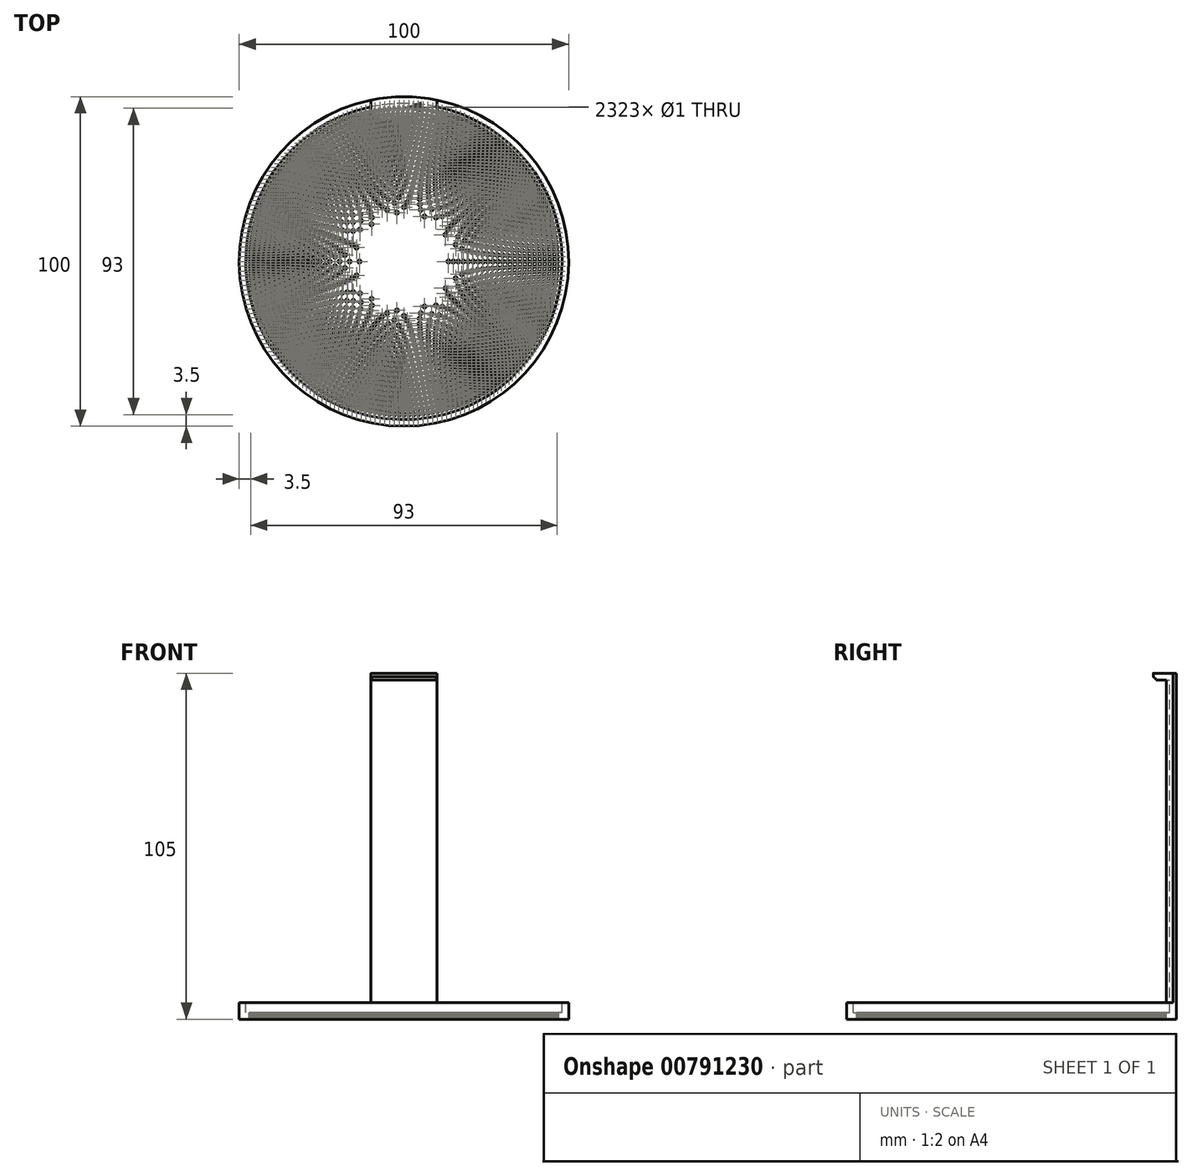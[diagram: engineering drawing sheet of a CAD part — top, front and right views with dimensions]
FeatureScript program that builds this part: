
annotation { "Feature Type Name" : "Feature", "Feature Type Description" : "" }
export const myFeature = defineFeature(function(context is Context, id is Id, definition is map)
    precondition{}
    {
        {
            var Q0;
            Q0=qCreatedBy(makeId("Top.planeOp"),FACE);
            var sketch = newSketch(context, id + "F0", { "sketchPlane" : qUnion([Q0])});
            skCircle(sketch, "E0", {"center": v(0, 0) * mm, "radius": 50 * mm});
            skSolve(sketch);
        }
        {
            var Q0;
            Q0 = qSketchRegion(id + "F0", true);
            extrude(context, id + "F1", {"entities" : qUnion([Q0]), "depth" : 5 * mm, "offsetDistance" : 25 * mm});
        }
        {
            var Q0;
            Q0=makeQuery(id+"F1.opExtrude","CAP_FACE",FACE,{"disambiguationData":[OSD([sQuery(id+"F0.wireOp",EDGE,"E0")])],"isStart":false});
            var sketch = newSketch(context, id + "F2", { "sketchPlane" : qUnion([Q0])});
            skCircle(sketch, "E1", {"center": v(0, 0) * mm, "radius": 48 * mm});
            skSolve(sketch);
        }
        {
            var Q0;
            Q0 = qSketchRegion(id + "F2", true);
            extrude(context, id + "F3", {"entities" : qUnion([Q0]), "operationType" : NewBodyOperationType.REMOVE, "oppositeDirection" : true, "depth" : 3 * mm, "offsetDistance" : 25 * mm});
        }
        {
            var Q0;
            Q0=makeQuery(id+"F3.boolean.opBoolean","COPY",FACE,{"derivedFrom":makeQuery(id+"F3.opExtrude","CAP_FACE",FACE,{"disambiguationData":[OSD([sQuery(id+"F2.wireOp",EDGE,"E1")])],"isStart":false})});
            var sketch = newSketch(context, id + "F4", { "sketchPlane" : qUnion([Q0])});
            skLineSegment(sketch, "E2", {"start": v(0, 0) * mm, "end": v(52.93, 0) * mm, "construction": true});
            skCircle(sketch, "E3", {"center": v(0, 0) * mm, "radius": 0.5 * mm, "construction": true});
            skCircle(sketch, "E4.1.0.0", {"center": v(1.5, 0) * mm, "radius": 0.5 * mm, "construction": true});
            skCircle(sketch, "E4.2.0.0", {"center": v(3, 0) * mm, "radius": 0.5 * mm, "construction": true});
            skCircle(sketch, "E4.3.0.0", {"center": v(4.5, 0) * mm, "radius": 0.5 * mm, "construction": true});
            skCircle(sketch, "E4.4.0.0", {"center": v(6, 0) * mm, "radius": 0.5 * mm, "construction": true});
            skCircle(sketch, "E4.5.0.0", {"center": v(7.5, 0) * mm, "radius": 0.5 * mm, "construction": true});
            skCircle(sketch, "E4.6.0.0", {"center": v(9, 0) * mm, "radius": 0.5 * mm, "construction": true});
            skCircle(sketch, "E4.7.0.0", {"center": v(10.5, 0) * mm, "radius": 0.5 * mm, "construction": true});
            skCircle(sketch, "E4.8.0.0", {"center": v(12, 0) * mm, "radius": 0.5 * mm, "construction": true});
            skCircle(sketch, "E4.9.0.0", {"center": v(13.5, 0) * mm, "radius": 0.5 * mm});
            skCircle(sketch, "E4.10.0.0", {"center": v(15, 0) * mm, "radius": 0.5 * mm});
            skCircle(sketch, "E4.11.0.0", {"center": v(16.5, 0) * mm, "radius": 0.5 * mm});
            skCircle(sketch, "E4.12.0.0", {"center": v(18, 0) * mm, "radius": 0.5 * mm});
            skCircle(sketch, "E4.13.0.0", {"center": v(19.5, 0) * mm, "radius": 0.5 * mm});
            skCircle(sketch, "E4.14.0.0", {"center": v(21, 0) * mm, "radius": 0.5 * mm});
            skCircle(sketch, "E4.15.0.0", {"center": v(22.5, 0) * mm, "radius": 0.5 * mm});
            skCircle(sketch, "E4.16.0.0", {"center": v(24, 0) * mm, "radius": 0.5 * mm});
            skCircle(sketch, "E4.17.0.0", {"center": v(25.5, 0) * mm, "radius": 0.5 * mm});
            skCircle(sketch, "E4.18.0.0", {"center": v(27, 0) * mm, "radius": 0.5 * mm});
            skCircle(sketch, "E4.19.0.0", {"center": v(28.5, 0) * mm, "radius": 0.5 * mm});
            skCircle(sketch, "E4.20.0.0", {"center": v(30, 0) * mm, "radius": 0.5 * mm});
            skCircle(sketch, "E4.21.0.0", {"center": v(31.5, 0) * mm, "radius": 0.5 * mm});
            skCircle(sketch, "E4.22.0.0", {"center": v(33, 0) * mm, "radius": 0.5 * mm});
            skCircle(sketch, "E4.23.0.0", {"center": v(34.5, 0) * mm, "radius": 0.5 * mm});
            skCircle(sketch, "E4.24.0.0", {"center": v(36, 0) * mm, "radius": 0.5 * mm});
            skCircle(sketch, "E4.25.0.0", {"center": v(37.5, 0) * mm, "radius": 0.5 * mm});
            skCircle(sketch, "E4.26.0.0", {"center": v(39, 0) * mm, "radius": 0.5 * mm});
            skCircle(sketch, "E4.27.0.0", {"center": v(40.5, 0) * mm, "radius": 0.5 * mm});
            skCircle(sketch, "E4.28.0.0", {"center": v(42, 0) * mm, "radius": 0.5 * mm});
            skCircle(sketch, "E4.29.0.0", {"center": v(43.5, 0) * mm, "radius": 0.5 * mm});
            skCircle(sketch, "E4.30.0.0", {"center": v(45, 0) * mm, "radius": 0.5 * mm});
            skCircle(sketch, "E4.31.0.0", {"center": v(46.5, 0) * mm, "radius": 0.5 * mm});
            skLineSegment(sketch, "E4.direction1", {"start": v(0, 0) * mm, "end": v(1.5, 0) * mm, "construction": true});
            skCircle(sketch, "E5.1.0", {"center": v(46.48, 1.46) * mm, "radius": 0.5 * mm});
            skCircle(sketch, "E5.2.0", {"center": v(46.4, 2.92) * mm, "radius": 0.5 * mm});
            skCircle(sketch, "E5.3.0", {"center": v(46.3, 4.38) * mm, "radius": 0.5 * mm});
            skCircle(sketch, "E5.4.0", {"center": v(46.13, 5.83) * mm, "radius": 0.5 * mm});
            skCircle(sketch, "E5.5.0", {"center": v(45.93, 7.27) * mm, "radius": 0.5 * mm});
            skCircle(sketch, "E5.6.0", {"center": v(45.68, 8.71) * mm, "radius": 0.5 * mm});
            skCircle(sketch, "E5.7.0", {"center": v(45.38, 10.14) * mm, "radius": 0.5 * mm});
            skCircle(sketch, "E5.8.0", {"center": v(45.04, 11.56) * mm, "radius": 0.5 * mm});
            skCircle(sketch, "E5.9.0", {"center": v(44.65, 12.97) * mm, "radius": 0.5 * mm});
            skCircle(sketch, "E5.10.0", {"center": v(44.22, 14.37) * mm, "radius": 0.5 * mm});
            skCircle(sketch, "E5.11.0", {"center": v(43.75, 15.75) * mm, "radius": 0.5 * mm});
            skCircle(sketch, "E5.12.0", {"center": v(43.23, 17.12) * mm, "radius": 0.5 * mm});
            skCircle(sketch, "E5.13.0", {"center": v(42.68, 18.47) * mm, "radius": 0.5 * mm});
            skCircle(sketch, "E5.14.0", {"center": v(42.07, 19.8) * mm, "radius": 0.5 * mm});
            skCircle(sketch, "E5.15.0", {"center": v(41.43, 21.11) * mm, "radius": 0.5 * mm});
            skCircle(sketch, "E5.16.0", {"center": v(40.75, 22.4) * mm, "radius": 0.5 * mm});
            skCircle(sketch, "E5.17.0", {"center": v(40.02, 23.67) * mm, "radius": 0.5 * mm});
            skCircle(sketch, "E5.18.0", {"center": v(39.26, 24.92) * mm, "radius": 0.5 * mm});
            skCircle(sketch, "E5.19.0", {"center": v(38.46, 26.14) * mm, "radius": 0.5 * mm});
            skCircle(sketch, "E5.20.0", {"center": v(37.62, 27.33) * mm, "radius": 0.5 * mm});
            skCircle(sketch, "E5.21.0", {"center": v(36.74, 28.5) * mm, "radius": 0.5 * mm});
            skCircle(sketch, "E5.22.0", {"center": v(35.83, 29.64) * mm, "radius": 0.5 * mm});
            skCircle(sketch, "E5.23.0", {"center": v(34.88, 30.75) * mm, "radius": 0.5 * mm});
            skCircle(sketch, "E5.24.0", {"center": v(33.9, 31.83) * mm, "radius": 0.5 * mm});
            skCircle(sketch, "E5.25.0", {"center": v(32.88, 32.88) * mm, "radius": 0.5 * mm});
            skCircle(sketch, "E5.26.0", {"center": v(31.83, 33.9) * mm, "radius": 0.5 * mm});
            skCircle(sketch, "E5.27.0", {"center": v(30.75, 34.88) * mm, "radius": 0.5 * mm});
            skCircle(sketch, "E5.28.0", {"center": v(29.64, 35.83) * mm, "radius": 0.5 * mm});
            skCircle(sketch, "E5.29.0", {"center": v(28.5, 36.74) * mm, "radius": 0.5 * mm});
            skCircle(sketch, "E5.30.0", {"center": v(27.33, 37.62) * mm, "radius": 0.5 * mm});
            skCircle(sketch, "E5.31.0", {"center": v(26.14, 38.46) * mm, "radius": 0.5 * mm});
            skCircle(sketch, "E5.32.0", {"center": v(24.92, 39.26) * mm, "radius": 0.5 * mm});
            skCircle(sketch, "E5.33.0", {"center": v(23.67, 40.02) * mm, "radius": 0.5 * mm});
            skCircle(sketch, "E5.34.0", {"center": v(22.4, 40.75) * mm, "radius": 0.5 * mm});
            skCircle(sketch, "E5.35.0", {"center": v(21.11, 41.43) * mm, "radius": 0.5 * mm});
            skCircle(sketch, "E5.36.0", {"center": v(19.8, 42.07) * mm, "radius": 0.5 * mm});
            skCircle(sketch, "E5.37.0", {"center": v(18.47, 42.68) * mm, "radius": 0.5 * mm});
            skCircle(sketch, "E5.38.0", {"center": v(17.12, 43.23) * mm, "radius": 0.5 * mm});
            skCircle(sketch, "E5.39.0", {"center": v(15.75, 43.75) * mm, "radius": 0.5 * mm});
            skCircle(sketch, "E5.40.0", {"center": v(14.37, 44.22) * mm, "radius": 0.5 * mm});
            skCircle(sketch, "E5.41.0", {"center": v(12.97, 44.65) * mm, "radius": 0.5 * mm});
            skCircle(sketch, "E5.42.0", {"center": v(11.56, 45.04) * mm, "radius": 0.5 * mm});
            skCircle(sketch, "E5.43.0", {"center": v(10.14, 45.38) * mm, "radius": 0.5 * mm});
            skCircle(sketch, "E5.44.0", {"center": v(8.71, 45.68) * mm, "radius": 0.5 * mm});
            skCircle(sketch, "E5.45.0", {"center": v(7.27, 45.93) * mm, "radius": 0.5 * mm});
            skCircle(sketch, "E5.46.0", {"center": v(5.83, 46.13) * mm, "radius": 0.5 * mm});
            skCircle(sketch, "E5.47.0", {"center": v(4.38, 46.3) * mm, "radius": 0.5 * mm});
            skCircle(sketch, "E5.48.0", {"center": v(2.92, 46.4) * mm, "radius": 0.5 * mm});
            skCircle(sketch, "E5.49.0", {"center": v(1.46, 46.48) * mm, "radius": 0.5 * mm});
            skCircle(sketch, "E5.50.0", {"center": v(0, 46.5) * mm, "radius": 0.5 * mm});
            skCircle(sketch, "E5.51.0", {"center": v(-1.46, 46.48) * mm, "radius": 0.5 * mm});
            skCircle(sketch, "E5.52.0", {"center": v(-2.92, 46.4) * mm, "radius": 0.5 * mm});
            skCircle(sketch, "E5.53.0", {"center": v(-4.38, 46.3) * mm, "radius": 0.5 * mm});
            skCircle(sketch, "E5.54.0", {"center": v(-5.83, 46.13) * mm, "radius": 0.5 * mm});
            skCircle(sketch, "E5.55.0", {"center": v(-7.27, 45.93) * mm, "radius": 0.5 * mm});
            skCircle(sketch, "E5.56.0", {"center": v(-8.71, 45.68) * mm, "radius": 0.5 * mm});
            skCircle(sketch, "E5.57.0", {"center": v(-10.14, 45.38) * mm, "radius": 0.5 * mm});
            skCircle(sketch, "E5.58.0", {"center": v(-11.56, 45.04) * mm, "radius": 0.5 * mm});
            skCircle(sketch, "E5.59.0", {"center": v(-12.97, 44.65) * mm, "radius": 0.5 * mm});
            skCircle(sketch, "E5.60.0", {"center": v(-14.37, 44.22) * mm, "radius": 0.5 * mm});
            skCircle(sketch, "E5.61.0", {"center": v(-15.75, 43.75) * mm, "radius": 0.5 * mm});
            skCircle(sketch, "E5.62.0", {"center": v(-17.12, 43.23) * mm, "radius": 0.5 * mm});
            skCircle(sketch, "E5.63.0", {"center": v(-18.47, 42.68) * mm, "radius": 0.5 * mm});
            skCircle(sketch, "E5.64.0", {"center": v(-19.8, 42.07) * mm, "radius": 0.5 * mm});
            skCircle(sketch, "E5.65.0", {"center": v(-21.11, 41.43) * mm, "radius": 0.5 * mm});
            skCircle(sketch, "E5.66.0", {"center": v(-22.4, 40.75) * mm, "radius": 0.5 * mm});
            skCircle(sketch, "E5.67.0", {"center": v(-23.67, 40.02) * mm, "radius": 0.5 * mm});
            skCircle(sketch, "E5.68.0", {"center": v(-24.92, 39.26) * mm, "radius": 0.5 * mm});
            skCircle(sketch, "E5.69.0", {"center": v(-26.14, 38.46) * mm, "radius": 0.5 * mm});
            skCircle(sketch, "E5.70.0", {"center": v(-27.33, 37.62) * mm, "radius": 0.5 * mm});
            skCircle(sketch, "E5.71.0", {"center": v(-28.5, 36.74) * mm, "radius": 0.5 * mm});
            skCircle(sketch, "E5.72.0", {"center": v(-29.64, 35.83) * mm, "radius": 0.5 * mm});
            skCircle(sketch, "E5.73.0", {"center": v(-30.75, 34.88) * mm, "radius": 0.5 * mm});
            skCircle(sketch, "E5.74.0", {"center": v(-31.83, 33.9) * mm, "radius": 0.5 * mm});
            skCircle(sketch, "E5.75.0", {"center": v(-32.88, 32.88) * mm, "radius": 0.5 * mm});
            skCircle(sketch, "E5.76.0", {"center": v(-33.9, 31.83) * mm, "radius": 0.5 * mm});
            skCircle(sketch, "E5.77.0", {"center": v(-34.88, 30.75) * mm, "radius": 0.5 * mm});
            skCircle(sketch, "E5.78.0", {"center": v(-35.83, 29.64) * mm, "radius": 0.5 * mm});
            skCircle(sketch, "E5.79.0", {"center": v(-36.74, 28.5) * mm, "radius": 0.5 * mm});
            skCircle(sketch, "E5.80.0", {"center": v(-37.62, 27.33) * mm, "radius": 0.5 * mm});
            skCircle(sketch, "E5.81.0", {"center": v(-38.46, 26.14) * mm, "radius": 0.5 * mm});
            skCircle(sketch, "E5.82.0", {"center": v(-39.26, 24.92) * mm, "radius": 0.5 * mm});
            skCircle(sketch, "E5.83.0", {"center": v(-40.02, 23.67) * mm, "radius": 0.5 * mm});
            skCircle(sketch, "E5.84.0", {"center": v(-40.75, 22.4) * mm, "radius": 0.5 * mm});
            skCircle(sketch, "E5.85.0", {"center": v(-41.43, 21.11) * mm, "radius": 0.5 * mm});
            skCircle(sketch, "E5.86.0", {"center": v(-42.07, 19.8) * mm, "radius": 0.5 * mm});
            skCircle(sketch, "E5.87.0", {"center": v(-42.68, 18.47) * mm, "radius": 0.5 * mm});
            skCircle(sketch, "E5.88.0", {"center": v(-43.23, 17.12) * mm, "radius": 0.5 * mm});
            skCircle(sketch, "E5.89.0", {"center": v(-43.75, 15.75) * mm, "radius": 0.5 * mm});
            skCircle(sketch, "E5.90.0", {"center": v(-44.22, 14.37) * mm, "radius": 0.5 * mm});
            skCircle(sketch, "E5.91.0", {"center": v(-44.65, 12.97) * mm, "radius": 0.5 * mm});
            skCircle(sketch, "E5.92.0", {"center": v(-45.04, 11.56) * mm, "radius": 0.5 * mm});
            skCircle(sketch, "E5.93.0", {"center": v(-45.38, 10.14) * mm, "radius": 0.5 * mm});
            skCircle(sketch, "E5.94.0", {"center": v(-45.68, 8.71) * mm, "radius": 0.5 * mm});
            skCircle(sketch, "E5.95.0", {"center": v(-45.93, 7.27) * mm, "radius": 0.5 * mm});
            skCircle(sketch, "E5.96.0", {"center": v(-46.13, 5.83) * mm, "radius": 0.5 * mm});
            skCircle(sketch, "E5.97.0", {"center": v(-46.3, 4.38) * mm, "radius": 0.5 * mm});
            skCircle(sketch, "E5.98.0", {"center": v(-46.4, 2.92) * mm, "radius": 0.5 * mm});
            skCircle(sketch, "E5.99.0", {"center": v(-46.48, 1.46) * mm, "radius": 0.5 * mm});
            skCircle(sketch, "E5.100.0", {"center": v(-46.5, 0) * mm, "radius": 0.5 * mm});
            skCircle(sketch, "E5.101.0", {"center": v(-46.48, -1.46) * mm, "radius": 0.5 * mm});
            skCircle(sketch, "E5.102.0", {"center": v(-46.4, -2.92) * mm, "radius": 0.5 * mm});
            skCircle(sketch, "E5.103.0", {"center": v(-46.3, -4.38) * mm, "radius": 0.5 * mm});
            skCircle(sketch, "E5.104.0", {"center": v(-46.13, -5.83) * mm, "radius": 0.5 * mm});
            skCircle(sketch, "E5.105.0", {"center": v(-45.93, -7.27) * mm, "radius": 0.5 * mm});
            skCircle(sketch, "E5.106.0", {"center": v(-45.68, -8.71) * mm, "radius": 0.5 * mm});
            skCircle(sketch, "E5.107.0", {"center": v(-45.38, -10.14) * mm, "radius": 0.5 * mm});
            skCircle(sketch, "E5.108.0", {"center": v(-45.04, -11.56) * mm, "radius": 0.5 * mm});
            skCircle(sketch, "E5.109.0", {"center": v(-44.65, -12.97) * mm, "radius": 0.5 * mm});
            skCircle(sketch, "E5.110.0", {"center": v(-44.22, -14.37) * mm, "radius": 0.5 * mm});
            skCircle(sketch, "E5.111.0", {"center": v(-43.75, -15.75) * mm, "radius": 0.5 * mm});
            skCircle(sketch, "E5.112.0", {"center": v(-43.23, -17.12) * mm, "radius": 0.5 * mm});
            skCircle(sketch, "E5.113.0", {"center": v(-42.68, -18.47) * mm, "radius": 0.5 * mm});
            skCircle(sketch, "E5.114.0", {"center": v(-42.07, -19.8) * mm, "radius": 0.5 * mm});
            skCircle(sketch, "E5.115.0", {"center": v(-41.43, -21.11) * mm, "radius": 0.5 * mm});
            skCircle(sketch, "E5.116.0", {"center": v(-40.75, -22.4) * mm, "radius": 0.5 * mm});
            skCircle(sketch, "E5.117.0", {"center": v(-40.02, -23.67) * mm, "radius": 0.5 * mm});
            skCircle(sketch, "E5.118.0", {"center": v(-39.26, -24.92) * mm, "radius": 0.5 * mm});
            skCircle(sketch, "E5.119.0", {"center": v(-38.46, -26.14) * mm, "radius": 0.5 * mm});
            skCircle(sketch, "E5.120.0", {"center": v(-37.62, -27.33) * mm, "radius": 0.5 * mm});
            skCircle(sketch, "E5.121.0", {"center": v(-36.74, -28.5) * mm, "radius": 0.5 * mm});
            skCircle(sketch, "E5.122.0", {"center": v(-35.83, -29.64) * mm, "radius": 0.5 * mm});
            skCircle(sketch, "E5.123.0", {"center": v(-34.88, -30.75) * mm, "radius": 0.5 * mm});
            skCircle(sketch, "E5.124.0", {"center": v(-33.9, -31.83) * mm, "radius": 0.5 * mm});
            skCircle(sketch, "E5.125.0", {"center": v(-32.88, -32.88) * mm, "radius": 0.5 * mm});
            skCircle(sketch, "E5.126.0", {"center": v(-31.83, -33.9) * mm, "radius": 0.5 * mm});
            skCircle(sketch, "E5.127.0", {"center": v(-30.75, -34.88) * mm, "radius": 0.5 * mm});
            skCircle(sketch, "E5.128.0", {"center": v(-29.64, -35.83) * mm, "radius": 0.5 * mm});
            skCircle(sketch, "E5.129.0", {"center": v(-28.5, -36.74) * mm, "radius": 0.5 * mm});
            skCircle(sketch, "E5.130.0", {"center": v(-27.33, -37.62) * mm, "radius": 0.5 * mm});
            skCircle(sketch, "E5.131.0", {"center": v(-26.14, -38.46) * mm, "radius": 0.5 * mm});
            skCircle(sketch, "E5.132.0", {"center": v(-24.92, -39.26) * mm, "radius": 0.5 * mm});
            skCircle(sketch, "E5.133.0", {"center": v(-23.67, -40.02) * mm, "radius": 0.5 * mm});
            skCircle(sketch, "E5.134.0", {"center": v(-22.4, -40.75) * mm, "radius": 0.5 * mm});
            skCircle(sketch, "E5.135.0", {"center": v(-21.11, -41.43) * mm, "radius": 0.5 * mm});
            skCircle(sketch, "E5.136.0", {"center": v(-19.8, -42.07) * mm, "radius": 0.5 * mm});
            skCircle(sketch, "E5.137.0", {"center": v(-18.47, -42.68) * mm, "radius": 0.5 * mm});
            skCircle(sketch, "E5.138.0", {"center": v(-17.12, -43.23) * mm, "radius": 0.5 * mm});
            skCircle(sketch, "E5.139.0", {"center": v(-15.75, -43.75) * mm, "radius": 0.5 * mm});
            skCircle(sketch, "E5.140.0", {"center": v(-14.37, -44.22) * mm, "radius": 0.5 * mm});
            skCircle(sketch, "E5.141.0", {"center": v(-12.97, -44.65) * mm, "radius": 0.5 * mm});
            skCircle(sketch, "E5.142.0", {"center": v(-11.56, -45.04) * mm, "radius": 0.5 * mm});
            skCircle(sketch, "E5.143.0", {"center": v(-10.14, -45.38) * mm, "radius": 0.5 * mm});
            skCircle(sketch, "E5.144.0", {"center": v(-8.71, -45.68) * mm, "radius": 0.5 * mm});
            skCircle(sketch, "E5.145.0", {"center": v(-7.27, -45.93) * mm, "radius": 0.5 * mm});
            skCircle(sketch, "E5.146.0", {"center": v(-5.83, -46.13) * mm, "radius": 0.5 * mm});
            skCircle(sketch, "E5.147.0", {"center": v(-4.38, -46.3) * mm, "radius": 0.5 * mm});
            skCircle(sketch, "E5.148.0", {"center": v(-2.92, -46.4) * mm, "radius": 0.5 * mm});
            skCircle(sketch, "E5.149.0", {"center": v(-1.46, -46.48) * mm, "radius": 0.5 * mm});
            skCircle(sketch, "E5.150.0", {"center": v(0, -46.5) * mm, "radius": 0.5 * mm});
            skCircle(sketch, "E5.151.0", {"center": v(1.46, -46.48) * mm, "radius": 0.5 * mm});
            skCircle(sketch, "E5.152.0", {"center": v(2.92, -46.4) * mm, "radius": 0.5 * mm});
            skCircle(sketch, "E5.153.0", {"center": v(4.38, -46.3) * mm, "radius": 0.5 * mm});
            skCircle(sketch, "E5.154.0", {"center": v(5.83, -46.13) * mm, "radius": 0.5 * mm});
            skCircle(sketch, "E5.155.0", {"center": v(7.27, -45.93) * mm, "radius": 0.5 * mm});
            skCircle(sketch, "E5.156.0", {"center": v(8.71, -45.68) * mm, "radius": 0.5 * mm});
            skCircle(sketch, "E5.157.0", {"center": v(10.14, -45.38) * mm, "radius": 0.5 * mm});
            skCircle(sketch, "E5.158.0", {"center": v(11.56, -45.04) * mm, "radius": 0.5 * mm});
            skCircle(sketch, "E5.159.0", {"center": v(12.97, -44.65) * mm, "radius": 0.5 * mm});
            skCircle(sketch, "E5.160.0", {"center": v(14.37, -44.22) * mm, "radius": 0.5 * mm});
            skCircle(sketch, "E5.161.0", {"center": v(15.75, -43.75) * mm, "radius": 0.5 * mm});
            skCircle(sketch, "E5.162.0", {"center": v(17.12, -43.23) * mm, "radius": 0.5 * mm});
            skCircle(sketch, "E5.163.0", {"center": v(18.47, -42.68) * mm, "radius": 0.5 * mm});
            skCircle(sketch, "E5.164.0", {"center": v(19.8, -42.07) * mm, "radius": 0.5 * mm});
            skCircle(sketch, "E5.165.0", {"center": v(21.11, -41.43) * mm, "radius": 0.5 * mm});
            skCircle(sketch, "E5.166.0", {"center": v(22.4, -40.75) * mm, "radius": 0.5 * mm});
            skCircle(sketch, "E5.167.0", {"center": v(23.67, -40.02) * mm, "radius": 0.5 * mm});
            skCircle(sketch, "E5.168.0", {"center": v(24.92, -39.26) * mm, "radius": 0.5 * mm});
            skCircle(sketch, "E5.169.0", {"center": v(26.14, -38.46) * mm, "radius": 0.5 * mm});
            skCircle(sketch, "E5.170.0", {"center": v(27.33, -37.62) * mm, "radius": 0.5 * mm});
            skCircle(sketch, "E5.171.0", {"center": v(28.5, -36.74) * mm, "radius": 0.5 * mm});
            skCircle(sketch, "E5.172.0", {"center": v(29.64, -35.83) * mm, "radius": 0.5 * mm});
            skCircle(sketch, "E5.173.0", {"center": v(30.75, -34.88) * mm, "radius": 0.5 * mm});
            skCircle(sketch, "E5.174.0", {"center": v(31.83, -33.9) * mm, "radius": 0.5 * mm});
            skCircle(sketch, "E5.175.0", {"center": v(32.88, -32.88) * mm, "radius": 0.5 * mm});
            skCircle(sketch, "E5.176.0", {"center": v(33.9, -31.83) * mm, "radius": 0.5 * mm});
            skCircle(sketch, "E5.177.0", {"center": v(34.88, -30.75) * mm, "radius": 0.5 * mm});
            skCircle(sketch, "E5.178.0", {"center": v(35.83, -29.64) * mm, "radius": 0.5 * mm});
            skCircle(sketch, "E5.179.0", {"center": v(36.74, -28.5) * mm, "radius": 0.5 * mm});
            skCircle(sketch, "E5.180.0", {"center": v(37.62, -27.33) * mm, "radius": 0.5 * mm});
            skCircle(sketch, "E5.181.0", {"center": v(38.46, -26.14) * mm, "radius": 0.5 * mm});
            skCircle(sketch, "E5.182.0", {"center": v(39.26, -24.92) * mm, "radius": 0.5 * mm});
            skCircle(sketch, "E5.183.0", {"center": v(40.02, -23.67) * mm, "radius": 0.5 * mm});
            skCircle(sketch, "E5.184.0", {"center": v(40.75, -22.4) * mm, "radius": 0.5 * mm});
            skCircle(sketch, "E5.185.0", {"center": v(41.43, -21.11) * mm, "radius": 0.5 * mm});
            skCircle(sketch, "E5.186.0", {"center": v(42.07, -19.8) * mm, "radius": 0.5 * mm});
            skCircle(sketch, "E5.187.0", {"center": v(42.68, -18.47) * mm, "radius": 0.5 * mm});
            skCircle(sketch, "E5.188.0", {"center": v(43.23, -17.12) * mm, "radius": 0.5 * mm});
            skCircle(sketch, "E5.189.0", {"center": v(43.75, -15.75) * mm, "radius": 0.5 * mm});
            skCircle(sketch, "E5.190.0", {"center": v(44.22, -14.37) * mm, "radius": 0.5 * mm});
            skCircle(sketch, "E5.191.0", {"center": v(44.65, -12.97) * mm, "radius": 0.5 * mm});
            skCircle(sketch, "E5.192.0", {"center": v(45.04, -11.56) * mm, "radius": 0.5 * mm});
            skCircle(sketch, "E5.193.0", {"center": v(45.38, -10.14) * mm, "radius": 0.5 * mm});
            skCircle(sketch, "E5.194.0", {"center": v(45.68, -8.71) * mm, "radius": 0.5 * mm});
            skCircle(sketch, "E5.195.0", {"center": v(45.93, -7.27) * mm, "radius": 0.5 * mm});
            skCircle(sketch, "E5.196.0", {"center": v(46.13, -5.83) * mm, "radius": 0.5 * mm});
            skCircle(sketch, "E5.197.0", {"center": v(46.3, -4.38) * mm, "radius": 0.5 * mm});
            skCircle(sketch, "E5.198.0", {"center": v(46.4, -2.92) * mm, "radius": 0.5 * mm});
            skCircle(sketch, "E5.199.0", {"center": v(46.48, -1.46) * mm, "radius": 0.5 * mm});
            skCircle(sketch, "E6.1.0", {"center": v(44.98, 1.48) * mm, "radius": 0.5 * mm});
            skCircle(sketch, "E6.2.0", {"center": v(44.9, 2.96) * mm, "radius": 0.5 * mm});
            skCircle(sketch, "E6.3.0", {"center": v(44.78, 4.43) * mm, "radius": 0.5 * mm});
            skCircle(sketch, "E6.4.0", {"center": v(44.61, 5.9) * mm, "radius": 0.5 * mm});
            skCircle(sketch, "E6.5.0", {"center": v(44.4, 7.37) * mm, "radius": 0.5 * mm});
            skCircle(sketch, "E6.6.0", {"center": v(44.13, 8.82) * mm, "radius": 0.5 * mm});
            skCircle(sketch, "E6.7.0", {"center": v(43.81, 10.27) * mm, "radius": 0.5 * mm});
            skCircle(sketch, "E6.8.0", {"center": v(43.45, 11.7) * mm, "radius": 0.5 * mm});
            skCircle(sketch, "E6.9.0", {"center": v(43.04, 13.13) * mm, "radius": 0.5 * mm});
            skCircle(sketch, "E6.10.0", {"center": v(42.59, 14.54) * mm, "radius": 0.5 * mm});
            skCircle(sketch, "E6.11.0", {"center": v(42.09, 15.93) * mm, "radius": 0.5 * mm});
            skCircle(sketch, "E6.12.0", {"center": v(41.54, 17.3) * mm, "radius": 0.5 * mm});
            skCircle(sketch, "E6.13.0", {"center": v(40.95, 18.66) * mm, "radius": 0.5 * mm});
            skCircle(sketch, "E6.14.0", {"center": v(40.31, 20) * mm, "radius": 0.5 * mm});
            skCircle(sketch, "E6.15.0", {"center": v(39.63, 21.31) * mm, "radius": 0.5 * mm});
            skCircle(sketch, "E6.16.0", {"center": v(38.9, 22.6) * mm, "radius": 0.5 * mm});
            skCircle(sketch, "E6.17.0", {"center": v(38.14, 23.87) * mm, "radius": 0.5 * mm});
            skCircle(sketch, "E6.18.0", {"center": v(37.34, 25.12) * mm, "radius": 0.5 * mm});
            skCircle(sketch, "E6.19.0", {"center": v(36.5, 26.33) * mm, "radius": 0.5 * mm});
            skCircle(sketch, "E6.20.0", {"center": v(35.6, 27.52) * mm, "radius": 0.5 * mm});
            skCircle(sketch, "E6.21.0", {"center": v(34.68, 28.67) * mm, "radius": 0.5 * mm});
            skCircle(sketch, "E6.22.0", {"center": v(33.72, 29.8) * mm, "radius": 0.5 * mm});
            skCircle(sketch, "E6.23.0", {"center": v(32.72, 30.9) * mm, "radius": 0.5 * mm});
            skCircle(sketch, "E6.24.0", {"center": v(31.69, 31.95) * mm, "radius": 0.5 * mm});
            skCircle(sketch, "E6.25.0", {"center": v(30.62, 32.98) * mm, "radius": 0.5 * mm});
            skCircle(sketch, "E6.26.0", {"center": v(29.52, 33.96) * mm, "radius": 0.5 * mm});
            skCircle(sketch, "E6.27.0", {"center": v(28.39, 34.92) * mm, "radius": 0.5 * mm});
            skCircle(sketch, "E6.28.0", {"center": v(27.22, 35.83) * mm, "radius": 0.5 * mm});
            skCircle(sketch, "E6.29.0", {"center": v(26.03, 36.7) * mm, "radius": 0.5 * mm});
            skCircle(sketch, "E6.30.0", {"center": v(24.8, 37.54) * mm, "radius": 0.5 * mm});
            skCircle(sketch, "E6.31.0", {"center": v(23.56, 38.34) * mm, "radius": 0.5 * mm});
            skCircle(sketch, "E6.32.0", {"center": v(22.29, 39.1) * mm, "radius": 0.5 * mm});
            skCircle(sketch, "E6.33.0", {"center": v(20.99, 39.8) * mm, "radius": 0.5 * mm});
            skCircle(sketch, "E6.34.0", {"center": v(19.67, 40.47) * mm, "radius": 0.5 * mm});
            skCircle(sketch, "E6.35.0", {"center": v(18.33, 41.1) * mm, "radius": 0.5 * mm});
            skCircle(sketch, "E6.36.0", {"center": v(16.96, 41.68) * mm, "radius": 0.5 * mm});
            skCircle(sketch, "E6.37.0", {"center": v(15.58, 42.22) * mm, "radius": 0.5 * mm});
            skCircle(sketch, "E6.38.0", {"center": v(14.19, 42.7) * mm, "radius": 0.5 * mm});
            skCircle(sketch, "E6.39.0", {"center": v(12.77, 43.15) * mm, "radius": 0.5 * mm});
            skCircle(sketch, "E6.40.0", {"center": v(11.35, 43.55) * mm, "radius": 0.5 * mm});
            skCircle(sketch, "E6.41.0", {"center": v(9.91, 43.9) * mm, "radius": 0.5 * mm});
            skCircle(sketch, "E6.42.0", {"center": v(8.46, 44.2) * mm, "radius": 0.5 * mm});
            skCircle(sketch, "E6.43.0", {"center": v(7, 44.45) * mm, "radius": 0.5 * mm});
            skCircle(sketch, "E6.44.0", {"center": v(5.54, 44.66) * mm, "radius": 0.5 * mm});
            skCircle(sketch, "E6.45.0", {"center": v(4.07, 44.82) * mm, "radius": 0.5 * mm});
            skCircle(sketch, "E6.46.0", {"center": v(2.59, 44.93) * mm, "radius": 0.5 * mm});
            skCircle(sketch, "E6.47.0", {"center": v(1.11, 44.99) * mm, "radius": 0.5 * mm});
            skCircle(sketch, "E6.48.0", {"center": v(-0.37, 45) * mm, "radius": 0.5 * mm});
            skCircle(sketch, "E6.49.0", {"center": v(-1.85, 44.96) * mm, "radius": 0.5 * mm});
            skCircle(sketch, "E6.50.0", {"center": v(-3.33, 44.88) * mm, "radius": 0.5 * mm});
            skCircle(sketch, "E6.51.0", {"center": v(-4.8, 44.74) * mm, "radius": 0.5 * mm});
            skCircle(sketch, "E6.52.0", {"center": v(-6.27, 44.56) * mm, "radius": 0.5 * mm});
            skCircle(sketch, "E6.53.0", {"center": v(-7.73, 44.33) * mm, "radius": 0.5 * mm});
            skCircle(sketch, "E6.54.0", {"center": v(-9.19, 44.05) * mm, "radius": 0.5 * mm});
            skCircle(sketch, "E6.55.0", {"center": v(-10.63, 43.73) * mm, "radius": 0.5 * mm});
            skCircle(sketch, "E6.56.0", {"center": v(-12.06, 43.35) * mm, "radius": 0.5 * mm});
            skCircle(sketch, "E6.57.0", {"center": v(-13.48, 42.93) * mm, "radius": 0.5 * mm});
            skCircle(sketch, "E6.58.0", {"center": v(-14.89, 42.47) * mm, "radius": 0.5 * mm});
            skCircle(sketch, "E6.59.0", {"center": v(-16.28, 41.95) * mm, "radius": 0.5 * mm});
            skCircle(sketch, "E6.60.0", {"center": v(-17.65, 41.4) * mm, "radius": 0.5 * mm});
            skCircle(sketch, "E6.61.0", {"center": v(-19, 40.8) * mm, "radius": 0.5 * mm});
            skCircle(sketch, "E6.62.0", {"center": v(-20.33, 40.15) * mm, "radius": 0.5 * mm});
            skCircle(sketch, "E6.63.0", {"center": v(-21.64, 39.46) * mm, "radius": 0.5 * mm});
            skCircle(sketch, "E6.64.0", {"center": v(-22.93, 38.72) * mm, "radius": 0.5 * mm});
            skCircle(sketch, "E6.65.0", {"center": v(-24.19, 37.95) * mm, "radius": 0.5 * mm});
            skCircle(sketch, "E6.66.0", {"center": v(-25.42, 37.13) * mm, "radius": 0.5 * mm});
            skCircle(sketch, "E6.67.0", {"center": v(-26.63, 36.27) * mm, "radius": 0.5 * mm});
            skCircle(sketch, "E6.68.0", {"center": v(-27.8, 35.38) * mm, "radius": 0.5 * mm});
            skCircle(sketch, "E6.69.0", {"center": v(-28.96, 34.45) * mm, "radius": 0.5 * mm});
            skCircle(sketch, "E6.70.0", {"center": v(-30.07, 33.47) * mm, "radius": 0.5 * mm});
            skCircle(sketch, "E6.71.0", {"center": v(-31.16, 32.47) * mm, "radius": 0.5 * mm});
            skCircle(sketch, "E6.72.0", {"center": v(-32.2, 31.42) * mm, "radius": 0.5 * mm});
            skCircle(sketch, "E6.73.0", {"center": v(-33.23, 30.35) * mm, "radius": 0.5 * mm});
            skCircle(sketch, "E6.74.0", {"center": v(-34.2, 29.24) * mm, "radius": 0.5 * mm});
            skCircle(sketch, "E6.75.0", {"center": v(-35.15, 28.1) * mm, "radius": 0.5 * mm});
            skCircle(sketch, "E6.76.0", {"center": v(-36.05, 26.93) * mm, "radius": 0.5 * mm});
            skCircle(sketch, "E6.77.0", {"center": v(-36.92, 25.73) * mm, "radius": 0.5 * mm});
            skCircle(sketch, "E6.78.0", {"center": v(-37.75, 24.5) * mm, "radius": 0.5 * mm});
            skCircle(sketch, "E6.79.0", {"center": v(-38.53, 23.24) * mm, "radius": 0.5 * mm});
            skCircle(sketch, "E6.80.0", {"center": v(-39.28, 21.96) * mm, "radius": 0.5 * mm});
            skCircle(sketch, "E6.81.0", {"center": v(-39.98, 20.66) * mm, "radius": 0.5 * mm});
            skCircle(sketch, "E6.82.0", {"center": v(-40.63, 19.33) * mm, "radius": 0.5 * mm});
            skCircle(sketch, "E6.83.0", {"center": v(-41.25, 17.99) * mm, "radius": 0.5 * mm});
            skCircle(sketch, "E6.84.0", {"center": v(-41.82, 16.62) * mm, "radius": 0.5 * mm});
            skCircle(sketch, "E6.85.0", {"center": v(-42.34, 15.24) * mm, "radius": 0.5 * mm});
            skCircle(sketch, "E6.86.0", {"center": v(-42.82, 13.84) * mm, "radius": 0.5 * mm});
            skCircle(sketch, "E6.87.0", {"center": v(-43.25, 12.42) * mm, "radius": 0.5 * mm});
            skCircle(sketch, "E6.88.0", {"center": v(-43.64, 11) * mm, "radius": 0.5 * mm});
            skCircle(sketch, "E6.89.0", {"center": v(-43.98, 9.55) * mm, "radius": 0.5 * mm});
            skCircle(sketch, "E6.90.0", {"center": v(-44.27, 8.1) * mm, "radius": 0.5 * mm});
            skCircle(sketch, "E6.91.0", {"center": v(-44.5, 6.64) * mm, "radius": 0.5 * mm});
            skCircle(sketch, "E6.92.0", {"center": v(-44.7, 5.17) * mm, "radius": 0.5 * mm});
            skCircle(sketch, "E6.93.0", {"center": v(-44.85, 3.7) * mm, "radius": 0.5 * mm});
            skCircle(sketch, "E6.94.0", {"center": v(-44.95, 2.22) * mm, "radius": 0.5 * mm});
            skCircle(sketch, "E6.95.0", {"center": v(-45, 0.74) * mm, "radius": 0.5 * mm});
            skCircle(sketch, "E6.96.0", {"center": v(-45, -0.74) * mm, "radius": 0.5 * mm});
            skCircle(sketch, "E6.97.0", {"center": v(-44.95, -2.22) * mm, "radius": 0.5 * mm});
            skCircle(sketch, "E6.98.0", {"center": v(-44.85, -3.7) * mm, "radius": 0.5 * mm});
            skCircle(sketch, "E6.99.0", {"center": v(-44.7, -5.17) * mm, "radius": 0.5 * mm});
            skCircle(sketch, "E6.100.0", {"center": v(-44.5, -6.64) * mm, "radius": 0.5 * mm});
            skCircle(sketch, "E6.101.0", {"center": v(-44.27, -8.1) * mm, "radius": 0.5 * mm});
            skCircle(sketch, "E6.102.0", {"center": v(-43.98, -9.55) * mm, "radius": 0.5 * mm});
            skCircle(sketch, "E6.103.0", {"center": v(-43.64, -11) * mm, "radius": 0.5 * mm});
            skCircle(sketch, "E6.104.0", {"center": v(-43.25, -12.42) * mm, "radius": 0.5 * mm});
            skCircle(sketch, "E6.105.0", {"center": v(-42.82, -13.84) * mm, "radius": 0.5 * mm});
            skCircle(sketch, "E6.106.0", {"center": v(-42.34, -15.24) * mm, "radius": 0.5 * mm});
            skCircle(sketch, "E6.107.0", {"center": v(-41.82, -16.62) * mm, "radius": 0.5 * mm});
            skCircle(sketch, "E6.108.0", {"center": v(-41.25, -17.99) * mm, "radius": 0.5 * mm});
            skCircle(sketch, "E6.109.0", {"center": v(-40.63, -19.33) * mm, "radius": 0.5 * mm});
            skCircle(sketch, "E6.110.0", {"center": v(-39.98, -20.66) * mm, "radius": 0.5 * mm});
            skCircle(sketch, "E6.111.0", {"center": v(-39.28, -21.96) * mm, "radius": 0.5 * mm});
            skCircle(sketch, "E6.112.0", {"center": v(-38.53, -23.24) * mm, "radius": 0.5 * mm});
            skCircle(sketch, "E6.113.0", {"center": v(-37.75, -24.5) * mm, "radius": 0.5 * mm});
            skCircle(sketch, "E6.114.0", {"center": v(-36.92, -25.73) * mm, "radius": 0.5 * mm});
            skCircle(sketch, "E6.115.0", {"center": v(-36.05, -26.93) * mm, "radius": 0.5 * mm});
            skCircle(sketch, "E6.116.0", {"center": v(-35.15, -28.1) * mm, "radius": 0.5 * mm});
            skCircle(sketch, "E6.117.0", {"center": v(-34.2, -29.24) * mm, "radius": 0.5 * mm});
            skCircle(sketch, "E6.118.0", {"center": v(-33.23, -30.35) * mm, "radius": 0.5 * mm});
            skCircle(sketch, "E6.119.0", {"center": v(-32.2, -31.42) * mm, "radius": 0.5 * mm});
            skCircle(sketch, "E6.120.0", {"center": v(-31.16, -32.47) * mm, "radius": 0.5 * mm});
            skCircle(sketch, "E6.121.0", {"center": v(-30.07, -33.47) * mm, "radius": 0.5 * mm});
            skCircle(sketch, "E6.122.0", {"center": v(-28.96, -34.45) * mm, "radius": 0.5 * mm});
            skCircle(sketch, "E6.123.0", {"center": v(-27.8, -35.38) * mm, "radius": 0.5 * mm});
            skCircle(sketch, "E6.124.0", {"center": v(-26.63, -36.27) * mm, "radius": 0.5 * mm});
            skCircle(sketch, "E6.125.0", {"center": v(-25.42, -37.13) * mm, "radius": 0.5 * mm});
            skCircle(sketch, "E6.126.0", {"center": v(-24.19, -37.95) * mm, "radius": 0.5 * mm});
            skCircle(sketch, "E6.127.0", {"center": v(-22.93, -38.72) * mm, "radius": 0.5 * mm});
            skCircle(sketch, "E6.128.0", {"center": v(-21.64, -39.46) * mm, "radius": 0.5 * mm});
            skCircle(sketch, "E6.129.0", {"center": v(-20.33, -40.15) * mm, "radius": 0.5 * mm});
            skCircle(sketch, "E6.130.0", {"center": v(-19, -40.8) * mm, "radius": 0.5 * mm});
            skCircle(sketch, "E6.131.0", {"center": v(-17.65, -41.4) * mm, "radius": 0.5 * mm});
            skCircle(sketch, "E6.132.0", {"center": v(-16.28, -41.95) * mm, "radius": 0.5 * mm});
            skCircle(sketch, "E6.133.0", {"center": v(-14.89, -42.47) * mm, "radius": 0.5 * mm});
            skCircle(sketch, "E6.134.0", {"center": v(-13.48, -42.93) * mm, "radius": 0.5 * mm});
            skCircle(sketch, "E6.135.0", {"center": v(-12.06, -43.35) * mm, "radius": 0.5 * mm});
            skCircle(sketch, "E6.136.0", {"center": v(-10.63, -43.73) * mm, "radius": 0.5 * mm});
            skCircle(sketch, "E6.137.0", {"center": v(-9.19, -44.05) * mm, "radius": 0.5 * mm});
            skCircle(sketch, "E6.138.0", {"center": v(-7.73, -44.33) * mm, "radius": 0.5 * mm});
            skCircle(sketch, "E6.139.0", {"center": v(-6.27, -44.56) * mm, "radius": 0.5 * mm});
            skCircle(sketch, "E6.140.0", {"center": v(-4.8, -44.74) * mm, "radius": 0.5 * mm});
            skCircle(sketch, "E6.141.0", {"center": v(-3.33, -44.88) * mm, "radius": 0.5 * mm});
            skCircle(sketch, "E6.142.0", {"center": v(-1.85, -44.96) * mm, "radius": 0.5 * mm});
            skCircle(sketch, "E6.143.0", {"center": v(-0.37, -45) * mm, "radius": 0.5 * mm});
            skCircle(sketch, "E6.144.0", {"center": v(1.11, -44.99) * mm, "radius": 0.5 * mm});
            skCircle(sketch, "E6.145.0", {"center": v(2.59, -44.93) * mm, "radius": 0.5 * mm});
            skCircle(sketch, "E6.146.0", {"center": v(4.07, -44.82) * mm, "radius": 0.5 * mm});
            skCircle(sketch, "E6.147.0", {"center": v(5.54, -44.66) * mm, "radius": 0.5 * mm});
            skCircle(sketch, "E6.148.0", {"center": v(7, -44.45) * mm, "radius": 0.5 * mm});
            skCircle(sketch, "E6.149.0", {"center": v(8.46, -44.2) * mm, "radius": 0.5 * mm});
            skCircle(sketch, "E6.150.0", {"center": v(9.91, -43.9) * mm, "radius": 0.5 * mm});
            skCircle(sketch, "E6.151.0", {"center": v(11.35, -43.55) * mm, "radius": 0.5 * mm});
            skCircle(sketch, "E6.152.0", {"center": v(12.77, -43.15) * mm, "radius": 0.5 * mm});
            skCircle(sketch, "E6.153.0", {"center": v(14.19, -42.7) * mm, "radius": 0.5 * mm});
            skCircle(sketch, "E6.154.0", {"center": v(15.58, -42.22) * mm, "radius": 0.5 * mm});
            skCircle(sketch, "E6.155.0", {"center": v(16.96, -41.68) * mm, "radius": 0.5 * mm});
            skCircle(sketch, "E6.156.0", {"center": v(18.33, -41.1) * mm, "radius": 0.5 * mm});
            skCircle(sketch, "E6.157.0", {"center": v(19.67, -40.47) * mm, "radius": 0.5 * mm});
            skCircle(sketch, "E6.158.0", {"center": v(20.99, -39.8) * mm, "radius": 0.5 * mm});
            skCircle(sketch, "E6.159.0", {"center": v(22.29, -39.1) * mm, "radius": 0.5 * mm});
            skCircle(sketch, "E6.160.0", {"center": v(23.56, -38.34) * mm, "radius": 0.5 * mm});
            skCircle(sketch, "E6.161.0", {"center": v(24.8, -37.54) * mm, "radius": 0.5 * mm});
            skCircle(sketch, "E6.162.0", {"center": v(26.03, -36.7) * mm, "radius": 0.5 * mm});
            skCircle(sketch, "E6.163.0", {"center": v(27.22, -35.83) * mm, "radius": 0.5 * mm});
            skCircle(sketch, "E6.164.0", {"center": v(28.39, -34.92) * mm, "radius": 0.5 * mm});
            skCircle(sketch, "E6.165.0", {"center": v(29.52, -33.96) * mm, "radius": 0.5 * mm});
            skCircle(sketch, "E6.166.0", {"center": v(30.62, -32.98) * mm, "radius": 0.5 * mm});
            skCircle(sketch, "E6.167.0", {"center": v(31.69, -31.95) * mm, "radius": 0.5 * mm});
            skCircle(sketch, "E6.168.0", {"center": v(32.72, -30.9) * mm, "radius": 0.5 * mm});
            skCircle(sketch, "E6.169.0", {"center": v(33.72, -29.8) * mm, "radius": 0.5 * mm});
            skCircle(sketch, "E6.170.0", {"center": v(34.68, -28.67) * mm, "radius": 0.5 * mm});
            skCircle(sketch, "E6.171.0", {"center": v(35.6, -27.52) * mm, "radius": 0.5 * mm});
            skCircle(sketch, "E6.172.0", {"center": v(36.5, -26.33) * mm, "radius": 0.5 * mm});
            skCircle(sketch, "E6.173.0", {"center": v(37.34, -25.12) * mm, "radius": 0.5 * mm});
            skCircle(sketch, "E6.174.0", {"center": v(38.14, -23.87) * mm, "radius": 0.5 * mm});
            skCircle(sketch, "E6.175.0", {"center": v(38.9, -22.6) * mm, "radius": 0.5 * mm});
            skCircle(sketch, "E6.176.0", {"center": v(39.63, -21.31) * mm, "radius": 0.5 * mm});
            skCircle(sketch, "E6.177.0", {"center": v(40.31, -20) * mm, "radius": 0.5 * mm});
            skCircle(sketch, "E6.178.0", {"center": v(40.95, -18.66) * mm, "radius": 0.5 * mm});
            skCircle(sketch, "E6.179.0", {"center": v(41.54, -17.3) * mm, "radius": 0.5 * mm});
            skCircle(sketch, "E6.180.0", {"center": v(42.09, -15.93) * mm, "radius": 0.5 * mm});
            skCircle(sketch, "E6.181.0", {"center": v(42.59, -14.54) * mm, "radius": 0.5 * mm});
            skCircle(sketch, "E6.182.0", {"center": v(43.04, -13.13) * mm, "radius": 0.5 * mm});
            skCircle(sketch, "E6.183.0", {"center": v(43.45, -11.7) * mm, "radius": 0.5 * mm});
            skCircle(sketch, "E6.184.0", {"center": v(43.81, -10.27) * mm, "radius": 0.5 * mm});
            skCircle(sketch, "E6.185.0", {"center": v(44.13, -8.82) * mm, "radius": 0.5 * mm});
            skCircle(sketch, "E6.186.0", {"center": v(44.4, -7.37) * mm, "radius": 0.5 * mm});
            skCircle(sketch, "E6.187.0", {"center": v(44.61, -5.9) * mm, "radius": 0.5 * mm});
            skCircle(sketch, "E6.188.0", {"center": v(44.78, -4.43) * mm, "radius": 0.5 * mm});
            skCircle(sketch, "E6.189.0", {"center": v(44.9, -2.96) * mm, "radius": 0.5 * mm});
            skCircle(sketch, "E6.190.0", {"center": v(44.98, -1.48) * mm, "radius": 0.5 * mm});
            skCircle(sketch, "E7.1.0", {"center": v(43.47, 1.5) * mm, "radius": 0.5 * mm});
            skCircle(sketch, "E7.2.0", {"center": v(43.4, 3) * mm, "radius": 0.5 * mm});
            skCircle(sketch, "E7.3.0", {"center": v(43.27, 4.5) * mm, "radius": 0.5 * mm});
            skCircle(sketch, "E7.4.0", {"center": v(43.09, 5.99) * mm, "radius": 0.5 * mm});
            skCircle(sketch, "E7.5.0", {"center": v(42.85, 7.47) * mm, "radius": 0.5 * mm});
            skCircle(sketch, "E7.6.0", {"center": v(42.57, 8.95) * mm, "radius": 0.5 * mm});
            skCircle(sketch, "E7.7.0", {"center": v(42.24, 10.41) * mm, "radius": 0.5 * mm});
            skCircle(sketch, "E7.8.0", {"center": v(41.85, 11.86) * mm, "radius": 0.5 * mm});
            skCircle(sketch, "E7.9.0", {"center": v(41.42, 13.3) * mm, "radius": 0.5 * mm});
            skCircle(sketch, "E7.10.0", {"center": v(40.93, 14.72) * mm, "radius": 0.5 * mm});
            skCircle(sketch, "E7.11.0", {"center": v(40.4, 16.13) * mm, "radius": 0.5 * mm});
            skCircle(sketch, "E7.12.0", {"center": v(39.82, 17.5) * mm, "radius": 0.5 * mm});
            skCircle(sketch, "E7.13.0", {"center": v(39.2, 18.87) * mm, "radius": 0.5 * mm});
            skCircle(sketch, "E7.14.0", {"center": v(38.52, 20.22) * mm, "radius": 0.5 * mm});
            skCircle(sketch, "E7.15.0", {"center": v(37.8, 21.53) * mm, "radius": 0.5 * mm});
            skCircle(sketch, "E7.16.0", {"center": v(37.03, 22.82) * mm, "radius": 0.5 * mm});
            skCircle(sketch, "E7.17.0", {"center": v(36.22, 24.09) * mm, "radius": 0.5 * mm});
            skCircle(sketch, "E7.18.0", {"center": v(35.37, 25.33) * mm, "radius": 0.5 * mm});
            skCircle(sketch, "E7.19.0", {"center": v(34.47, 26.53) * mm, "radius": 0.5 * mm});
            skCircle(sketch, "E7.20.0", {"center": v(33.54, 27.7) * mm, "radius": 0.5 * mm});
            skCircle(sketch, "E7.21.0", {"center": v(32.56, 28.85) * mm, "radius": 0.5 * mm});
            skCircle(sketch, "E7.22.0", {"center": v(31.55, 29.95) * mm, "radius": 0.5 * mm});
            skCircle(sketch, "E7.23.0", {"center": v(30.5, 31.02) * mm, "radius": 0.5 * mm});
            skCircle(sketch, "E7.24.0", {"center": v(29.4, 32.06) * mm, "radius": 0.5 * mm});
            skCircle(sketch, "E7.25.0", {"center": v(28.28, 33.05) * mm, "radius": 0.5 * mm});
            skCircle(sketch, "E7.26.0", {"center": v(27.12, 34) * mm, "radius": 0.5 * mm});
            skCircle(sketch, "E7.27.0", {"center": v(25.93, 34.93) * mm, "radius": 0.5 * mm});
            skCircle(sketch, "E7.28.0", {"center": v(24.71, 35.8) * mm, "radius": 0.5 * mm});
            skCircle(sketch, "E7.29.0", {"center": v(23.46, 36.63) * mm, "radius": 0.5 * mm});
            skCircle(sketch, "E7.30.0", {"center": v(22.18, 37.42) * mm, "radius": 0.5 * mm});
            skCircle(sketch, "E7.31.0", {"center": v(20.88, 38.16) * mm, "radius": 0.5 * mm});
            skCircle(sketch, "E7.32.0", {"center": v(19.55, 38.86) * mm, "radius": 0.5 * mm});
            skCircle(sketch, "E7.33.0", {"center": v(18.2, 39.51) * mm, "radius": 0.5 * mm});
            skCircle(sketch, "E7.34.0", {"center": v(16.82, 40.12) * mm, "radius": 0.5 * mm});
            skCircle(sketch, "E7.35.0", {"center": v(15.43, 40.67) * mm, "radius": 0.5 * mm});
            skCircle(sketch, "E7.36.0", {"center": v(14.01, 41.18) * mm, "radius": 0.5 * mm});
            skCircle(sketch, "E7.37.0", {"center": v(12.58, 41.64) * mm, "radius": 0.5 * mm});
            skCircle(sketch, "E7.38.0", {"center": v(11.14, 42.05) * mm, "radius": 0.5 * mm});
            skCircle(sketch, "E7.39.0", {"center": v(9.68, 42.4) * mm, "radius": 0.5 * mm});
            skCircle(sketch, "E7.40.0", {"center": v(8.21, 42.72) * mm, "radius": 0.5 * mm});
            skCircle(sketch, "E7.41.0", {"center": v(6.73, 42.98) * mm, "radius": 0.5 * mm});
            skCircle(sketch, "E7.42.0", {"center": v(5.24, 43.18) * mm, "radius": 0.5 * mm});
            skCircle(sketch, "E7.43.0", {"center": v(3.75, 43.34) * mm, "radius": 0.5 * mm});
            skCircle(sketch, "E7.44.0", {"center": v(2.25, 43.44) * mm, "radius": 0.5 * mm});
            skCircle(sketch, "E7.45.0", {"center": v(0.75, 43.5) * mm, "radius": 0.5 * mm});
            skCircle(sketch, "E7.46.0", {"center": v(-0.75, 43.5) * mm, "radius": 0.5 * mm});
            skCircle(sketch, "E7.47.0", {"center": v(-2.25, 43.44) * mm, "radius": 0.5 * mm});
            skCircle(sketch, "E7.48.0", {"center": v(-3.75, 43.34) * mm, "radius": 0.5 * mm});
            skCircle(sketch, "E7.49.0", {"center": v(-5.24, 43.18) * mm, "radius": 0.5 * mm});
            skCircle(sketch, "E7.50.0", {"center": v(-6.73, 42.98) * mm, "radius": 0.5 * mm});
            skCircle(sketch, "E7.51.0", {"center": v(-8.21, 42.72) * mm, "radius": 0.5 * mm});
            skCircle(sketch, "E7.52.0", {"center": v(-9.68, 42.4) * mm, "radius": 0.5 * mm});
            skCircle(sketch, "E7.53.0", {"center": v(-11.14, 42.05) * mm, "radius": 0.5 * mm});
            skCircle(sketch, "E7.54.0", {"center": v(-12.58, 41.64) * mm, "radius": 0.5 * mm});
            skCircle(sketch, "E7.55.0", {"center": v(-14.01, 41.18) * mm, "radius": 0.5 * mm});
            skCircle(sketch, "E7.56.0", {"center": v(-15.43, 40.67) * mm, "radius": 0.5 * mm});
            skCircle(sketch, "E7.57.0", {"center": v(-16.82, 40.12) * mm, "radius": 0.5 * mm});
            skCircle(sketch, "E7.58.0", {"center": v(-18.2, 39.51) * mm, "radius": 0.5 * mm});
            skCircle(sketch, "E7.59.0", {"center": v(-19.55, 38.86) * mm, "radius": 0.5 * mm});
            skCircle(sketch, "E7.60.0", {"center": v(-20.88, 38.16) * mm, "radius": 0.5 * mm});
            skCircle(sketch, "E7.61.0", {"center": v(-22.18, 37.42) * mm, "radius": 0.5 * mm});
            skCircle(sketch, "E7.62.0", {"center": v(-23.46, 36.63) * mm, "radius": 0.5 * mm});
            skCircle(sketch, "E7.63.0", {"center": v(-24.71, 35.8) * mm, "radius": 0.5 * mm});
            skCircle(sketch, "E7.64.0", {"center": v(-25.93, 34.93) * mm, "radius": 0.5 * mm});
            skCircle(sketch, "E7.65.0", {"center": v(-27.12, 34) * mm, "radius": 0.5 * mm});
            skCircle(sketch, "E7.66.0", {"center": v(-28.28, 33.05) * mm, "radius": 0.5 * mm});
            skCircle(sketch, "E7.67.0", {"center": v(-29.4, 32.06) * mm, "radius": 0.5 * mm});
            skCircle(sketch, "E7.68.0", {"center": v(-30.5, 31.02) * mm, "radius": 0.5 * mm});
            skCircle(sketch, "E7.69.0", {"center": v(-31.55, 29.95) * mm, "radius": 0.5 * mm});
            skCircle(sketch, "E7.70.0", {"center": v(-32.56, 28.85) * mm, "radius": 0.5 * mm});
            skCircle(sketch, "E7.71.0", {"center": v(-33.54, 27.7) * mm, "radius": 0.5 * mm});
            skCircle(sketch, "E7.72.0", {"center": v(-34.47, 26.53) * mm, "radius": 0.5 * mm});
            skCircle(sketch, "E7.73.0", {"center": v(-35.37, 25.33) * mm, "radius": 0.5 * mm});
            skCircle(sketch, "E7.74.0", {"center": v(-36.22, 24.09) * mm, "radius": 0.5 * mm});
            skCircle(sketch, "E7.75.0", {"center": v(-37.03, 22.82) * mm, "radius": 0.5 * mm});
            skCircle(sketch, "E7.76.0", {"center": v(-37.8, 21.53) * mm, "radius": 0.5 * mm});
            skCircle(sketch, "E7.77.0", {"center": v(-38.52, 20.22) * mm, "radius": 0.5 * mm});
            skCircle(sketch, "E7.78.0", {"center": v(-39.2, 18.87) * mm, "radius": 0.5 * mm});
            skCircle(sketch, "E7.79.0", {"center": v(-39.82, 17.5) * mm, "radius": 0.5 * mm});
            skCircle(sketch, "E7.80.0", {"center": v(-40.4, 16.13) * mm, "radius": 0.5 * mm});
            skCircle(sketch, "E7.81.0", {"center": v(-40.93, 14.72) * mm, "radius": 0.5 * mm});
            skCircle(sketch, "E7.82.0", {"center": v(-41.42, 13.3) * mm, "radius": 0.5 * mm});
            skCircle(sketch, "E7.83.0", {"center": v(-41.85, 11.86) * mm, "radius": 0.5 * mm});
            skCircle(sketch, "E7.84.0", {"center": v(-42.24, 10.41) * mm, "radius": 0.5 * mm});
            skCircle(sketch, "E7.85.0", {"center": v(-42.57, 8.95) * mm, "radius": 0.5 * mm});
            skCircle(sketch, "E7.86.0", {"center": v(-42.85, 7.47) * mm, "radius": 0.5 * mm});
            skCircle(sketch, "E7.87.0", {"center": v(-43.09, 5.99) * mm, "radius": 0.5 * mm});
            skCircle(sketch, "E7.88.0", {"center": v(-43.27, 4.5) * mm, "radius": 0.5 * mm});
            skCircle(sketch, "E7.89.0", {"center": v(-43.4, 3) * mm, "radius": 0.5 * mm});
            skCircle(sketch, "E7.90.0", {"center": v(-43.47, 1.5) * mm, "radius": 0.5 * mm});
            skCircle(sketch, "E7.91.0", {"center": v(-43.5, 0) * mm, "radius": 0.5 * mm});
            skCircle(sketch, "E7.92.0", {"center": v(-43.47, -1.5) * mm, "radius": 0.5 * mm});
            skCircle(sketch, "E7.93.0", {"center": v(-43.4, -3) * mm, "radius": 0.5 * mm});
            skCircle(sketch, "E7.94.0", {"center": v(-43.27, -4.5) * mm, "radius": 0.5 * mm});
            skCircle(sketch, "E7.95.0", {"center": v(-43.09, -5.99) * mm, "radius": 0.5 * mm});
            skCircle(sketch, "E7.96.0", {"center": v(-42.85, -7.47) * mm, "radius": 0.5 * mm});
            skCircle(sketch, "E7.97.0", {"center": v(-42.57, -8.95) * mm, "radius": 0.5 * mm});
            skCircle(sketch, "E7.98.0", {"center": v(-42.24, -10.41) * mm, "radius": 0.5 * mm});
            skCircle(sketch, "E7.99.0", {"center": v(-41.85, -11.86) * mm, "radius": 0.5 * mm});
            skCircle(sketch, "E7.100.0", {"center": v(-41.42, -13.3) * mm, "radius": 0.5 * mm});
            skCircle(sketch, "E7.101.0", {"center": v(-40.93, -14.72) * mm, "radius": 0.5 * mm});
            skCircle(sketch, "E7.102.0", {"center": v(-40.4, -16.13) * mm, "radius": 0.5 * mm});
            skCircle(sketch, "E7.103.0", {"center": v(-39.82, -17.5) * mm, "radius": 0.5 * mm});
            skCircle(sketch, "E7.104.0", {"center": v(-39.2, -18.87) * mm, "radius": 0.5 * mm});
            skCircle(sketch, "E7.105.0", {"center": v(-38.52, -20.22) * mm, "radius": 0.5 * mm});
            skCircle(sketch, "E7.106.0", {"center": v(-37.8, -21.53) * mm, "radius": 0.5 * mm});
            skCircle(sketch, "E7.107.0", {"center": v(-37.03, -22.82) * mm, "radius": 0.5 * mm});
            skCircle(sketch, "E7.108.0", {"center": v(-36.22, -24.09) * mm, "radius": 0.5 * mm});
            skCircle(sketch, "E7.109.0", {"center": v(-35.37, -25.33) * mm, "radius": 0.5 * mm});
            skCircle(sketch, "E7.110.0", {"center": v(-34.47, -26.53) * mm, "radius": 0.5 * mm});
            skCircle(sketch, "E7.111.0", {"center": v(-33.54, -27.7) * mm, "radius": 0.5 * mm});
            skCircle(sketch, "E7.112.0", {"center": v(-32.56, -28.85) * mm, "radius": 0.5 * mm});
            skCircle(sketch, "E7.113.0", {"center": v(-31.55, -29.95) * mm, "radius": 0.5 * mm});
            skCircle(sketch, "E7.114.0", {"center": v(-30.5, -31.02) * mm, "radius": 0.5 * mm});
            skCircle(sketch, "E7.115.0", {"center": v(-29.4, -32.06) * mm, "radius": 0.5 * mm});
            skCircle(sketch, "E7.116.0", {"center": v(-28.28, -33.05) * mm, "radius": 0.5 * mm});
            skCircle(sketch, "E7.117.0", {"center": v(-27.12, -34) * mm, "radius": 0.5 * mm});
            skCircle(sketch, "E7.118.0", {"center": v(-25.93, -34.93) * mm, "radius": 0.5 * mm});
            skCircle(sketch, "E7.119.0", {"center": v(-24.71, -35.8) * mm, "radius": 0.5 * mm});
            skCircle(sketch, "E7.120.0", {"center": v(-23.46, -36.63) * mm, "radius": 0.5 * mm});
            skCircle(sketch, "E7.121.0", {"center": v(-22.18, -37.42) * mm, "radius": 0.5 * mm});
            skCircle(sketch, "E7.122.0", {"center": v(-20.88, -38.16) * mm, "radius": 0.5 * mm});
            skCircle(sketch, "E7.123.0", {"center": v(-19.55, -38.86) * mm, "radius": 0.5 * mm});
            skCircle(sketch, "E7.124.0", {"center": v(-18.2, -39.51) * mm, "radius": 0.5 * mm});
            skCircle(sketch, "E7.125.0", {"center": v(-16.82, -40.12) * mm, "radius": 0.5 * mm});
            skCircle(sketch, "E7.126.0", {"center": v(-15.43, -40.67) * mm, "radius": 0.5 * mm});
            skCircle(sketch, "E7.127.0", {"center": v(-14.01, -41.18) * mm, "radius": 0.5 * mm});
            skCircle(sketch, "E7.128.0", {"center": v(-12.58, -41.64) * mm, "radius": 0.5 * mm});
            skCircle(sketch, "E7.129.0", {"center": v(-11.14, -42.05) * mm, "radius": 0.5 * mm});
            skCircle(sketch, "E7.130.0", {"center": v(-9.68, -42.4) * mm, "radius": 0.5 * mm});
            skCircle(sketch, "E7.131.0", {"center": v(-8.21, -42.72) * mm, "radius": 0.5 * mm});
            skCircle(sketch, "E7.132.0", {"center": v(-6.73, -42.98) * mm, "radius": 0.5 * mm});
            skCircle(sketch, "E7.133.0", {"center": v(-5.24, -43.18) * mm, "radius": 0.5 * mm});
            skCircle(sketch, "E7.134.0", {"center": v(-3.75, -43.34) * mm, "radius": 0.5 * mm});
            skCircle(sketch, "E7.135.0", {"center": v(-2.25, -43.44) * mm, "radius": 0.5 * mm});
            skCircle(sketch, "E7.136.0", {"center": v(-0.75, -43.5) * mm, "radius": 0.5 * mm});
            skCircle(sketch, "E7.137.0", {"center": v(0.75, -43.5) * mm, "radius": 0.5 * mm});
            skCircle(sketch, "E7.138.0", {"center": v(2.25, -43.44) * mm, "radius": 0.5 * mm});
            skCircle(sketch, "E7.139.0", {"center": v(3.75, -43.34) * mm, "radius": 0.5 * mm});
            skCircle(sketch, "E7.140.0", {"center": v(5.24, -43.18) * mm, "radius": 0.5 * mm});
            skCircle(sketch, "E7.141.0", {"center": v(6.73, -42.98) * mm, "radius": 0.5 * mm});
            skCircle(sketch, "E7.142.0", {"center": v(8.21, -42.72) * mm, "radius": 0.5 * mm});
            skCircle(sketch, "E7.143.0", {"center": v(9.68, -42.4) * mm, "radius": 0.5 * mm});
            skCircle(sketch, "E7.144.0", {"center": v(11.14, -42.05) * mm, "radius": 0.5 * mm});
            skCircle(sketch, "E7.145.0", {"center": v(12.58, -41.64) * mm, "radius": 0.5 * mm});
            skCircle(sketch, "E7.146.0", {"center": v(14.01, -41.18) * mm, "radius": 0.5 * mm});
            skCircle(sketch, "E7.147.0", {"center": v(15.43, -40.67) * mm, "radius": 0.5 * mm});
            skCircle(sketch, "E7.148.0", {"center": v(16.82, -40.12) * mm, "radius": 0.5 * mm});
            skCircle(sketch, "E7.149.0", {"center": v(18.2, -39.51) * mm, "radius": 0.5 * mm});
            skCircle(sketch, "E7.150.0", {"center": v(19.55, -38.86) * mm, "radius": 0.5 * mm});
            skCircle(sketch, "E7.151.0", {"center": v(20.88, -38.16) * mm, "radius": 0.5 * mm});
            skCircle(sketch, "E7.152.0", {"center": v(22.18, -37.42) * mm, "radius": 0.5 * mm});
            skCircle(sketch, "E7.153.0", {"center": v(23.46, -36.63) * mm, "radius": 0.5 * mm});
            skCircle(sketch, "E7.154.0", {"center": v(24.71, -35.8) * mm, "radius": 0.5 * mm});
            skCircle(sketch, "E7.155.0", {"center": v(25.93, -34.93) * mm, "radius": 0.5 * mm});
            skCircle(sketch, "E7.156.0", {"center": v(27.12, -34) * mm, "radius": 0.5 * mm});
            skCircle(sketch, "E7.157.0", {"center": v(28.28, -33.05) * mm, "radius": 0.5 * mm});
            skCircle(sketch, "E7.158.0", {"center": v(29.4, -32.06) * mm, "radius": 0.5 * mm});
            skCircle(sketch, "E7.159.0", {"center": v(30.5, -31.02) * mm, "radius": 0.5 * mm});
            skCircle(sketch, "E7.160.0", {"center": v(31.55, -29.95) * mm, "radius": 0.5 * mm});
            skCircle(sketch, "E7.161.0", {"center": v(32.56, -28.85) * mm, "radius": 0.5 * mm});
            skCircle(sketch, "E7.162.0", {"center": v(33.54, -27.7) * mm, "radius": 0.5 * mm});
            skCircle(sketch, "E7.163.0", {"center": v(34.47, -26.53) * mm, "radius": 0.5 * mm});
            skCircle(sketch, "E7.164.0", {"center": v(35.37, -25.33) * mm, "radius": 0.5 * mm});
            skCircle(sketch, "E7.165.0", {"center": v(36.22, -24.09) * mm, "radius": 0.5 * mm});
            skCircle(sketch, "E7.166.0", {"center": v(37.03, -22.82) * mm, "radius": 0.5 * mm});
            skCircle(sketch, "E7.167.0", {"center": v(37.8, -21.53) * mm, "radius": 0.5 * mm});
            skCircle(sketch, "E7.168.0", {"center": v(38.52, -20.22) * mm, "radius": 0.5 * mm});
            skCircle(sketch, "E7.169.0", {"center": v(39.2, -18.87) * mm, "radius": 0.5 * mm});
            skCircle(sketch, "E7.170.0", {"center": v(39.82, -17.5) * mm, "radius": 0.5 * mm});
            skCircle(sketch, "E7.171.0", {"center": v(40.4, -16.13) * mm, "radius": 0.5 * mm});
            skCircle(sketch, "E7.172.0", {"center": v(40.93, -14.72) * mm, "radius": 0.5 * mm});
            skCircle(sketch, "E7.173.0", {"center": v(41.42, -13.3) * mm, "radius": 0.5 * mm});
            skCircle(sketch, "E7.174.0", {"center": v(41.85, -11.86) * mm, "radius": 0.5 * mm});
            skCircle(sketch, "E7.175.0", {"center": v(42.24, -10.41) * mm, "radius": 0.5 * mm});
            skCircle(sketch, "E7.176.0", {"center": v(42.57, -8.95) * mm, "radius": 0.5 * mm});
            skCircle(sketch, "E7.177.0", {"center": v(42.85, -7.47) * mm, "radius": 0.5 * mm});
            skCircle(sketch, "E7.178.0", {"center": v(43.09, -5.99) * mm, "radius": 0.5 * mm});
            skCircle(sketch, "E7.179.0", {"center": v(43.27, -4.5) * mm, "radius": 0.5 * mm});
            skCircle(sketch, "E7.180.0", {"center": v(43.4, -3) * mm, "radius": 0.5 * mm});
            skCircle(sketch, "E7.181.0", {"center": v(43.47, -1.5) * mm, "radius": 0.5 * mm});
            skCircle(sketch, "E8.1.0", {"center": v(41.97, 1.53) * mm, "radius": 0.5 * mm});
            skCircle(sketch, "E8.2.0", {"center": v(41.89, 3.05) * mm, "radius": 0.5 * mm});
            skCircle(sketch, "E8.3.0", {"center": v(41.75, 4.57) * mm, "radius": 0.5 * mm});
            skCircle(sketch, "E8.4.0", {"center": v(41.56, 6.08) * mm, "radius": 0.5 * mm});
            skCircle(sketch, "E8.5.0", {"center": v(41.3, 7.59) * mm, "radius": 0.5 * mm});
            skCircle(sketch, "E8.6.0", {"center": v(41, 9.08) * mm, "radius": 0.5 * mm});
            skCircle(sketch, "E8.7.0", {"center": v(40.65, 10.56) * mm, "radius": 0.5 * mm});
            skCircle(sketch, "E8.8.0", {"center": v(40.24, 12.03) * mm, "radius": 0.5 * mm});
            skCircle(sketch, "E8.9.0", {"center": v(39.78, 13.49) * mm, "radius": 0.5 * mm});
            skCircle(sketch, "E8.10.0", {"center": v(39.26, 14.92) * mm, "radius": 0.5 * mm});
            skCircle(sketch, "E8.11.0", {"center": v(38.7, 16.34) * mm, "radius": 0.5 * mm});
            skCircle(sketch, "E8.12.0", {"center": v(38.07, 17.73) * mm, "radius": 0.5 * mm});
            skCircle(sketch, "E8.13.0", {"center": v(37.4, 19.1) * mm, "radius": 0.5 * mm});
            skCircle(sketch, "E8.14.0", {"center": v(36.69, 20.45) * mm, "radius": 0.5 * mm});
            skCircle(sketch, "E8.15.0", {"center": v(35.92, 21.77) * mm, "radius": 0.5 * mm});
            skCircle(sketch, "E8.16.0", {"center": v(35.1, 23.06) * mm, "radius": 0.5 * mm});
            skCircle(sketch, "E8.17.0", {"center": v(34.25, 24.32) * mm, "radius": 0.5 * mm});
            skCircle(sketch, "E8.18.0", {"center": v(33.34, 25.54) * mm, "radius": 0.5 * mm});
            skCircle(sketch, "E8.19.0", {"center": v(32.4, 26.74) * mm, "radius": 0.5 * mm});
            skCircle(sketch, "E8.20.0", {"center": v(31.4, 27.9) * mm, "radius": 0.5 * mm});
            skCircle(sketch, "E8.21.0", {"center": v(30.36, 29.02) * mm, "radius": 0.5 * mm});
            skCircle(sketch, "E8.22.0", {"center": v(29.3, 30.1) * mm, "radius": 0.5 * mm});
            skCircle(sketch, "E8.23.0", {"center": v(28.18, 31.14) * mm, "radius": 0.5 * mm});
            skCircle(sketch, "E8.24.0", {"center": v(27.03, 32.15) * mm, "radius": 0.5 * mm});
            skCircle(sketch, "E8.25.0", {"center": v(25.84, 33.1) * mm, "radius": 0.5 * mm});
            skCircle(sketch, "E8.26.0", {"center": v(24.63, 34.02) * mm, "radius": 0.5 * mm});
            skCircle(sketch, "E8.27.0", {"center": v(23.37, 34.9) * mm, "radius": 0.5 * mm});
            skCircle(sketch, "E8.28.0", {"center": v(22.1, 35.72) * mm, "radius": 0.5 * mm});
            skCircle(sketch, "E8.29.0", {"center": v(20.78, 36.5) * mm, "radius": 0.5 * mm});
            skCircle(sketch, "E8.30.0", {"center": v(19.44, 37.23) * mm, "radius": 0.5 * mm});
            skCircle(sketch, "E8.31.0", {"center": v(18.08, 37.91) * mm, "radius": 0.5 * mm});
            skCircle(sketch, "E8.32.0", {"center": v(16.69, 38.54) * mm, "radius": 0.5 * mm});
            skCircle(sketch, "E8.33.0", {"center": v(15.28, 39.12) * mm, "radius": 0.5 * mm});
            skCircle(sketch, "E8.34.0", {"center": v(13.85, 39.65) * mm, "radius": 0.5 * mm});
            skCircle(sketch, "E8.35.0", {"center": v(12.4, 40.13) * mm, "radius": 0.5 * mm});
            skCircle(sketch, "E8.36.0", {"center": v(10.93, 40.55) * mm, "radius": 0.5 * mm});
            skCircle(sketch, "E8.37.0", {"center": v(9.45, 40.92) * mm, "radius": 0.5 * mm});
            skCircle(sketch, "E8.38.0", {"center": v(7.96, 41.24) * mm, "radius": 0.5 * mm});
            skCircle(sketch, "E8.39.0", {"center": v(6.46, 41.5) * mm, "radius": 0.5 * mm});
            skCircle(sketch, "E8.40.0", {"center": v(4.95, 41.7) * mm, "radius": 0.5 * mm});
            skCircle(sketch, "E8.41.0", {"center": v(3.43, 41.86) * mm, "radius": 0.5 * mm});
            skCircle(sketch, "E8.42.0", {"center": v(1.9, 41.96) * mm, "radius": 0.5 * mm});
            skCircle(sketch, "E8.43.0", {"center": v(0.38, 42) * mm, "radius": 0.5 * mm});
            skCircle(sketch, "E8.44.0", {"center": v(-1.14, 41.98) * mm, "radius": 0.5 * mm});
            skCircle(sketch, "E8.45.0", {"center": v(-2.67, 41.92) * mm, "radius": 0.5 * mm});
            skCircle(sketch, "E8.46.0", {"center": v(-4.19, 41.8) * mm, "radius": 0.5 * mm});
            skCircle(sketch, "E8.47.0", {"center": v(-5.7, 41.61) * mm, "radius": 0.5 * mm});
            skCircle(sketch, "E8.48.0", {"center": v(-7.2, 41.38) * mm, "radius": 0.5 * mm});
            skCircle(sketch, "E8.49.0", {"center": v(-8.7, 41.09) * mm, "radius": 0.5 * mm});
            skCircle(sketch, "E8.50.0", {"center": v(-10.2, 40.74) * mm, "radius": 0.5 * mm});
            skCircle(sketch, "E8.51.0", {"center": v(-11.67, 40.35) * mm, "radius": 0.5 * mm});
            skCircle(sketch, "E8.52.0", {"center": v(-13.12, 39.9) * mm, "radius": 0.5 * mm});
            skCircle(sketch, "E8.53.0", {"center": v(-14.56, 39.4) * mm, "radius": 0.5 * mm});
            skCircle(sketch, "E8.54.0", {"center": v(-15.98, 38.84) * mm, "radius": 0.5 * mm});
            skCircle(sketch, "E8.55.0", {"center": v(-17.38, 38.23) * mm, "radius": 0.5 * mm});
            skCircle(sketch, "E8.56.0", {"center": v(-18.76, 37.58) * mm, "radius": 0.5 * mm});
            skCircle(sketch, "E8.57.0", {"center": v(-20.11, 36.87) * mm, "radius": 0.5 * mm});
            skCircle(sketch, "E8.58.0", {"center": v(-21.44, 36.12) * mm, "radius": 0.5 * mm});
            skCircle(sketch, "E8.59.0", {"center": v(-22.74, 35.31) * mm, "radius": 0.5 * mm});
            skCircle(sketch, "E8.60.0", {"center": v(-24, 34.47) * mm, "radius": 0.5 * mm});
            skCircle(sketch, "E8.61.0", {"center": v(-25.24, 33.57) * mm, "radius": 0.5 * mm});
            skCircle(sketch, "E8.62.0", {"center": v(-26.44, 32.63) * mm, "radius": 0.5 * mm});
            skCircle(sketch, "E8.63.0", {"center": v(-27.6, 31.65) * mm, "radius": 0.5 * mm});
            skCircle(sketch, "E8.64.0", {"center": v(-28.74, 30.63) * mm, "radius": 0.5 * mm});
            skCircle(sketch, "E8.65.0", {"center": v(-29.83, 29.56) * mm, "radius": 0.5 * mm});
            skCircle(sketch, "E8.66.0", {"center": v(-30.89, 28.46) * mm, "radius": 0.5 * mm});
            skCircle(sketch, "E8.67.0", {"center": v(-31.9, 27.32) * mm, "radius": 0.5 * mm});
            skCircle(sketch, "E8.68.0", {"center": v(-32.87, 26.14) * mm, "radius": 0.5 * mm});
            skCircle(sketch, "E8.69.0", {"center": v(-33.8, 24.93) * mm, "radius": 0.5 * mm});
            skCircle(sketch, "E8.70.0", {"center": v(-34.68, 23.69) * mm, "radius": 0.5 * mm});
            skCircle(sketch, "E8.71.0", {"center": v(-35.52, 22.41) * mm, "radius": 0.5 * mm});
            skCircle(sketch, "E8.72.0", {"center": v(-36.3, 21.1) * mm, "radius": 0.5 * mm});
            skCircle(sketch, "E8.73.0", {"center": v(-37.05, 19.78) * mm, "radius": 0.5 * mm});
            skCircle(sketch, "E8.74.0", {"center": v(-37.75, 18.42) * mm, "radius": 0.5 * mm});
            skCircle(sketch, "E8.75.0", {"center": v(-38.39, 17.04) * mm, "radius": 0.5 * mm});
            skCircle(sketch, "E8.76.0", {"center": v(-38.98, 15.63) * mm, "radius": 0.5 * mm});
            skCircle(sketch, "E8.77.0", {"center": v(-39.52, 14.2) * mm, "radius": 0.5 * mm});
            skCircle(sketch, "E8.78.0", {"center": v(-40.01, 12.76) * mm, "radius": 0.5 * mm});
            skCircle(sketch, "E8.79.0", {"center": v(-40.45, 11.3) * mm, "radius": 0.5 * mm});
            skCircle(sketch, "E8.80.0", {"center": v(-40.84, 9.82) * mm, "radius": 0.5 * mm});
            skCircle(sketch, "E8.81.0", {"center": v(-41.16, 8.33) * mm, "radius": 0.5 * mm});
            skCircle(sketch, "E8.82.0", {"center": v(-41.44, 6.83) * mm, "radius": 0.5 * mm});
            skCircle(sketch, "E8.83.0", {"center": v(-41.66, 5.32) * mm, "radius": 0.5 * mm});
            skCircle(sketch, "E8.84.0", {"center": v(-41.83, 3.8) * mm, "radius": 0.5 * mm});
            skCircle(sketch, "E8.85.0", {"center": v(-41.94, 2.29) * mm, "radius": 0.5 * mm});
            skCircle(sketch, "E8.86.0", {"center": v(-42, 0.76) * mm, "radius": 0.5 * mm});
            skCircle(sketch, "E8.87.0", {"center": v(-42, -0.76) * mm, "radius": 0.5 * mm});
            skCircle(sketch, "E8.88.0", {"center": v(-41.94, -2.29) * mm, "radius": 0.5 * mm});
            skCircle(sketch, "E8.89.0", {"center": v(-41.83, -3.8) * mm, "radius": 0.5 * mm});
            skCircle(sketch, "E8.90.0", {"center": v(-41.66, -5.32) * mm, "radius": 0.5 * mm});
            skCircle(sketch, "E8.91.0", {"center": v(-41.44, -6.83) * mm, "radius": 0.5 * mm});
            skCircle(sketch, "E8.92.0", {"center": v(-41.16, -8.33) * mm, "radius": 0.5 * mm});
            skCircle(sketch, "E8.93.0", {"center": v(-40.84, -9.82) * mm, "radius": 0.5 * mm});
            skCircle(sketch, "E8.94.0", {"center": v(-40.45, -11.3) * mm, "radius": 0.5 * mm});
            skCircle(sketch, "E8.95.0", {"center": v(-40.01, -12.76) * mm, "radius": 0.5 * mm});
            skCircle(sketch, "E8.96.0", {"center": v(-39.52, -14.2) * mm, "radius": 0.5 * mm});
            skCircle(sketch, "E8.97.0", {"center": v(-38.98, -15.63) * mm, "radius": 0.5 * mm});
            skCircle(sketch, "E8.98.0", {"center": v(-38.39, -17.04) * mm, "radius": 0.5 * mm});
            skCircle(sketch, "E8.99.0", {"center": v(-37.75, -18.42) * mm, "radius": 0.5 * mm});
            skCircle(sketch, "E8.100.0", {"center": v(-37.05, -19.78) * mm, "radius": 0.5 * mm});
            skCircle(sketch, "E8.101.0", {"center": v(-36.3, -21.1) * mm, "radius": 0.5 * mm});
            skCircle(sketch, "E8.102.0", {"center": v(-35.52, -22.41) * mm, "radius": 0.5 * mm});
            skCircle(sketch, "E8.103.0", {"center": v(-34.68, -23.69) * mm, "radius": 0.5 * mm});
            skCircle(sketch, "E8.104.0", {"center": v(-33.8, -24.93) * mm, "radius": 0.5 * mm});
            skCircle(sketch, "E8.105.0", {"center": v(-32.87, -26.14) * mm, "radius": 0.5 * mm});
            skCircle(sketch, "E8.106.0", {"center": v(-31.9, -27.32) * mm, "radius": 0.5 * mm});
            skCircle(sketch, "E8.107.0", {"center": v(-30.89, -28.46) * mm, "radius": 0.5 * mm});
            skCircle(sketch, "E8.108.0", {"center": v(-29.83, -29.56) * mm, "radius": 0.5 * mm});
            skCircle(sketch, "E8.109.0", {"center": v(-28.74, -30.63) * mm, "radius": 0.5 * mm});
            skCircle(sketch, "E8.110.0", {"center": v(-27.6, -31.65) * mm, "radius": 0.5 * mm});
            skCircle(sketch, "E8.111.0", {"center": v(-26.44, -32.63) * mm, "radius": 0.5 * mm});
            skCircle(sketch, "E8.112.0", {"center": v(-25.24, -33.57) * mm, "radius": 0.5 * mm});
            skCircle(sketch, "E8.113.0", {"center": v(-24, -34.47) * mm, "radius": 0.5 * mm});
            skCircle(sketch, "E8.114.0", {"center": v(-22.74, -35.31) * mm, "radius": 0.5 * mm});
            skCircle(sketch, "E8.115.0", {"center": v(-21.44, -36.12) * mm, "radius": 0.5 * mm});
            skCircle(sketch, "E8.116.0", {"center": v(-20.11, -36.87) * mm, "radius": 0.5 * mm});
            skCircle(sketch, "E8.117.0", {"center": v(-18.76, -37.58) * mm, "radius": 0.5 * mm});
            skCircle(sketch, "E8.118.0", {"center": v(-17.38, -38.23) * mm, "radius": 0.5 * mm});
            skCircle(sketch, "E8.119.0", {"center": v(-15.98, -38.84) * mm, "radius": 0.5 * mm});
            skCircle(sketch, "E8.120.0", {"center": v(-14.56, -39.4) * mm, "radius": 0.5 * mm});
            skCircle(sketch, "E8.121.0", {"center": v(-13.12, -39.9) * mm, "radius": 0.5 * mm});
            skCircle(sketch, "E8.122.0", {"center": v(-11.67, -40.35) * mm, "radius": 0.5 * mm});
            skCircle(sketch, "E8.123.0", {"center": v(-10.2, -40.74) * mm, "radius": 0.5 * mm});
            skCircle(sketch, "E8.124.0", {"center": v(-8.7, -41.09) * mm, "radius": 0.5 * mm});
            skCircle(sketch, "E8.125.0", {"center": v(-7.2, -41.38) * mm, "radius": 0.5 * mm});
            skCircle(sketch, "E8.126.0", {"center": v(-5.7, -41.61) * mm, "radius": 0.5 * mm});
            skCircle(sketch, "E8.127.0", {"center": v(-4.19, -41.8) * mm, "radius": 0.5 * mm});
            skCircle(sketch, "E8.128.0", {"center": v(-2.67, -41.92) * mm, "radius": 0.5 * mm});
            skCircle(sketch, "E8.129.0", {"center": v(-1.14, -41.98) * mm, "radius": 0.5 * mm});
            skCircle(sketch, "E8.130.0", {"center": v(0.38, -42) * mm, "radius": 0.5 * mm});
            skCircle(sketch, "E8.131.0", {"center": v(1.9, -41.96) * mm, "radius": 0.5 * mm});
            skCircle(sketch, "E8.132.0", {"center": v(3.43, -41.86) * mm, "radius": 0.5 * mm});
            skCircle(sketch, "E8.133.0", {"center": v(4.95, -41.7) * mm, "radius": 0.5 * mm});
            skCircle(sketch, "E8.134.0", {"center": v(6.46, -41.5) * mm, "radius": 0.5 * mm});
            skCircle(sketch, "E8.135.0", {"center": v(7.96, -41.24) * mm, "radius": 0.5 * mm});
            skCircle(sketch, "E8.136.0", {"center": v(9.45, -40.92) * mm, "radius": 0.5 * mm});
            skCircle(sketch, "E8.137.0", {"center": v(10.93, -40.55) * mm, "radius": 0.5 * mm});
            skCircle(sketch, "E8.138.0", {"center": v(12.4, -40.13) * mm, "radius": 0.5 * mm});
            skCircle(sketch, "E8.139.0", {"center": v(13.85, -39.65) * mm, "radius": 0.5 * mm});
            skCircle(sketch, "E8.140.0", {"center": v(15.28, -39.12) * mm, "radius": 0.5 * mm});
            skCircle(sketch, "E8.141.0", {"center": v(16.69, -38.54) * mm, "radius": 0.5 * mm});
            skCircle(sketch, "E8.142.0", {"center": v(18.08, -37.91) * mm, "radius": 0.5 * mm});
            skCircle(sketch, "E8.143.0", {"center": v(19.44, -37.23) * mm, "radius": 0.5 * mm});
            skCircle(sketch, "E8.144.0", {"center": v(20.78, -36.5) * mm, "radius": 0.5 * mm});
            skCircle(sketch, "E8.145.0", {"center": v(22.1, -35.72) * mm, "radius": 0.5 * mm});
            skCircle(sketch, "E8.146.0", {"center": v(23.37, -34.9) * mm, "radius": 0.5 * mm});
            skCircle(sketch, "E8.147.0", {"center": v(24.63, -34.02) * mm, "radius": 0.5 * mm});
            skCircle(sketch, "E8.148.0", {"center": v(25.84, -33.1) * mm, "radius": 0.5 * mm});
            skCircle(sketch, "E8.149.0", {"center": v(27.03, -32.15) * mm, "radius": 0.5 * mm});
            skCircle(sketch, "E8.150.0", {"center": v(28.18, -31.14) * mm, "radius": 0.5 * mm});
            skCircle(sketch, "E8.151.0", {"center": v(29.3, -30.1) * mm, "radius": 0.5 * mm});
            skCircle(sketch, "E8.152.0", {"center": v(30.36, -29.02) * mm, "radius": 0.5 * mm});
            skCircle(sketch, "E8.153.0", {"center": v(31.4, -27.9) * mm, "radius": 0.5 * mm});
            skCircle(sketch, "E8.154.0", {"center": v(32.4, -26.74) * mm, "radius": 0.5 * mm});
            skCircle(sketch, "E8.155.0", {"center": v(33.34, -25.54) * mm, "radius": 0.5 * mm});
            skCircle(sketch, "E8.156.0", {"center": v(34.25, -24.32) * mm, "radius": 0.5 * mm});
            skCircle(sketch, "E8.157.0", {"center": v(35.1, -23.06) * mm, "radius": 0.5 * mm});
            skCircle(sketch, "E8.158.0", {"center": v(35.92, -21.77) * mm, "radius": 0.5 * mm});
            skCircle(sketch, "E8.159.0", {"center": v(36.69, -20.45) * mm, "radius": 0.5 * mm});
            skCircle(sketch, "E8.160.0", {"center": v(37.4, -19.1) * mm, "radius": 0.5 * mm});
            skCircle(sketch, "E8.161.0", {"center": v(38.07, -17.73) * mm, "radius": 0.5 * mm});
            skCircle(sketch, "E8.162.0", {"center": v(38.7, -16.34) * mm, "radius": 0.5 * mm});
            skCircle(sketch, "E8.163.0", {"center": v(39.26, -14.92) * mm, "radius": 0.5 * mm});
            skCircle(sketch, "E8.164.0", {"center": v(39.78, -13.49) * mm, "radius": 0.5 * mm});
            skCircle(sketch, "E8.165.0", {"center": v(40.24, -12.03) * mm, "radius": 0.5 * mm});
            skCircle(sketch, "E8.166.0", {"center": v(40.65, -10.56) * mm, "radius": 0.5 * mm});
            skCircle(sketch, "E8.167.0", {"center": v(41, -9.08) * mm, "radius": 0.5 * mm});
            skCircle(sketch, "E8.168.0", {"center": v(41.3, -7.59) * mm, "radius": 0.5 * mm});
            skCircle(sketch, "E8.169.0", {"center": v(41.56, -6.08) * mm, "radius": 0.5 * mm});
            skCircle(sketch, "E8.170.0", {"center": v(41.75, -4.57) * mm, "radius": 0.5 * mm});
            skCircle(sketch, "E8.171.0", {"center": v(41.89, -3.05) * mm, "radius": 0.5 * mm});
            skCircle(sketch, "E8.172.0", {"center": v(41.97, -1.53) * mm, "radius": 0.5 * mm});
            skCircle(sketch, "E9.1.0", {"center": v(40.47, 1.55) * mm, "radius": 0.5 * mm});
            skCircle(sketch, "E9.2.0", {"center": v(40.38, 3.1) * mm, "radius": 0.5 * mm});
            skCircle(sketch, "E9.3.0", {"center": v(40.23, 4.64) * mm, "radius": 0.5 * mm});
            skCircle(sketch, "E9.4.0", {"center": v(40.03, 6.18) * mm, "radius": 0.5 * mm});
            skCircle(sketch, "E9.5.0", {"center": v(39.76, 7.71) * mm, "radius": 0.5 * mm});
            skCircle(sketch, "E9.6.0", {"center": v(39.43, 9.23) * mm, "radius": 0.5 * mm});
            skCircle(sketch, "E9.7.0", {"center": v(39.05, 10.73) * mm, "radius": 0.5 * mm});
            skCircle(sketch, "E9.8.0", {"center": v(38.61, 12.22) * mm, "radius": 0.5 * mm});
            skCircle(sketch, "E9.9.0", {"center": v(38.12, 13.69) * mm, "radius": 0.5 * mm});
            skCircle(sketch, "E9.10.0", {"center": v(37.56, 15.14) * mm, "radius": 0.5 * mm});
            skCircle(sketch, "E9.11.0", {"center": v(36.96, 16.57) * mm, "radius": 0.5 * mm});
            skCircle(sketch, "E9.12.0", {"center": v(36.3, 17.97) * mm, "radius": 0.5 * mm});
            skCircle(sketch, "E9.13.0", {"center": v(35.58, 19.35) * mm, "radius": 0.5 * mm});
            skCircle(sketch, "E9.14.0", {"center": v(34.81, 20.7) * mm, "radius": 0.5 * mm});
            skCircle(sketch, "E9.15.0", {"center": v(34, 22.01) * mm, "radius": 0.5 * mm});
            skCircle(sketch, "E9.16.0", {"center": v(33.13, 23.3) * mm, "radius": 0.5 * mm});
            skCircle(sketch, "E9.17.0", {"center": v(32.2, 24.55) * mm, "radius": 0.5 * mm});
            skCircle(sketch, "E9.18.0", {"center": v(31.25, 25.77) * mm, "radius": 0.5 * mm});
            skCircle(sketch, "E9.19.0", {"center": v(30.24, 26.95) * mm, "radius": 0.5 * mm});
            skCircle(sketch, "E9.20.0", {"center": v(29.18, 28.08) * mm, "radius": 0.5 * mm});
            skCircle(sketch, "E9.21.0", {"center": v(28.08, 29.18) * mm, "radius": 0.5 * mm});
            skCircle(sketch, "E9.22.0", {"center": v(26.95, 30.24) * mm, "radius": 0.5 * mm});
            skCircle(sketch, "E9.23.0", {"center": v(25.77, 31.25) * mm, "radius": 0.5 * mm});
            skCircle(sketch, "E9.24.0", {"center": v(24.55, 32.2) * mm, "radius": 0.5 * mm});
            skCircle(sketch, "E9.25.0", {"center": v(23.3, 33.13) * mm, "radius": 0.5 * mm});
            skCircle(sketch, "E9.26.0", {"center": v(22.01, 34) * mm, "radius": 0.5 * mm});
            skCircle(sketch, "E9.27.0", {"center": v(20.7, 34.81) * mm, "radius": 0.5 * mm});
            skCircle(sketch, "E9.28.0", {"center": v(19.35, 35.58) * mm, "radius": 0.5 * mm});
            skCircle(sketch, "E9.29.0", {"center": v(17.97, 36.3) * mm, "radius": 0.5 * mm});
            skCircle(sketch, "E9.30.0", {"center": v(16.57, 36.96) * mm, "radius": 0.5 * mm});
            skCircle(sketch, "E9.31.0", {"center": v(15.14, 37.56) * mm, "radius": 0.5 * mm});
            skCircle(sketch, "E9.32.0", {"center": v(13.69, 38.12) * mm, "radius": 0.5 * mm});
            skCircle(sketch, "E9.33.0", {"center": v(12.22, 38.61) * mm, "radius": 0.5 * mm});
            skCircle(sketch, "E9.34.0", {"center": v(10.73, 39.05) * mm, "radius": 0.5 * mm});
            skCircle(sketch, "E9.35.0", {"center": v(9.23, 39.43) * mm, "radius": 0.5 * mm});
            skCircle(sketch, "E9.36.0", {"center": v(7.71, 39.76) * mm, "radius": 0.5 * mm});
            skCircle(sketch, "E9.37.0", {"center": v(6.18, 40.03) * mm, "radius": 0.5 * mm});
            skCircle(sketch, "E9.38.0", {"center": v(4.64, 40.23) * mm, "radius": 0.5 * mm});
            skCircle(sketch, "E9.39.0", {"center": v(3.1, 40.38) * mm, "radius": 0.5 * mm});
            skCircle(sketch, "E9.40.0", {"center": v(1.55, 40.47) * mm, "radius": 0.5 * mm});
            skCircle(sketch, "E9.41.0", {"center": v(0, 40.5) * mm, "radius": 0.5 * mm});
            skCircle(sketch, "E9.42.0", {"center": v(-1.55, 40.47) * mm, "radius": 0.5 * mm});
            skCircle(sketch, "E9.43.0", {"center": v(-3.1, 40.38) * mm, "radius": 0.5 * mm});
            skCircle(sketch, "E9.44.0", {"center": v(-4.64, 40.23) * mm, "radius": 0.5 * mm});
            skCircle(sketch, "E9.45.0", {"center": v(-6.18, 40.03) * mm, "radius": 0.5 * mm});
            skCircle(sketch, "E9.46.0", {"center": v(-7.71, 39.76) * mm, "radius": 0.5 * mm});
            skCircle(sketch, "E9.47.0", {"center": v(-9.23, 39.43) * mm, "radius": 0.5 * mm});
            skCircle(sketch, "E9.48.0", {"center": v(-10.73, 39.05) * mm, "radius": 0.5 * mm});
            skCircle(sketch, "E9.49.0", {"center": v(-12.22, 38.61) * mm, "radius": 0.5 * mm});
            skCircle(sketch, "E9.50.0", {"center": v(-13.69, 38.12) * mm, "radius": 0.5 * mm});
            skCircle(sketch, "E9.51.0", {"center": v(-15.14, 37.56) * mm, "radius": 0.5 * mm});
            skCircle(sketch, "E9.52.0", {"center": v(-16.57, 36.96) * mm, "radius": 0.5 * mm});
            skCircle(sketch, "E9.53.0", {"center": v(-17.97, 36.3) * mm, "radius": 0.5 * mm});
            skCircle(sketch, "E9.54.0", {"center": v(-19.35, 35.58) * mm, "radius": 0.5 * mm});
            skCircle(sketch, "E9.55.0", {"center": v(-20.7, 34.81) * mm, "radius": 0.5 * mm});
            skCircle(sketch, "E9.56.0", {"center": v(-22.01, 34) * mm, "radius": 0.5 * mm});
            skCircle(sketch, "E9.57.0", {"center": v(-23.3, 33.13) * mm, "radius": 0.5 * mm});
            skCircle(sketch, "E9.58.0", {"center": v(-24.55, 32.2) * mm, "radius": 0.5 * mm});
            skCircle(sketch, "E9.59.0", {"center": v(-25.77, 31.25) * mm, "radius": 0.5 * mm});
            skCircle(sketch, "E9.60.0", {"center": v(-26.95, 30.24) * mm, "radius": 0.5 * mm});
            skCircle(sketch, "E9.61.0", {"center": v(-28.08, 29.18) * mm, "radius": 0.5 * mm});
            skCircle(sketch, "E9.62.0", {"center": v(-29.18, 28.08) * mm, "radius": 0.5 * mm});
            skCircle(sketch, "E9.63.0", {"center": v(-30.24, 26.95) * mm, "radius": 0.5 * mm});
            skCircle(sketch, "E9.64.0", {"center": v(-31.25, 25.77) * mm, "radius": 0.5 * mm});
            skCircle(sketch, "E9.65.0", {"center": v(-32.2, 24.55) * mm, "radius": 0.5 * mm});
            skCircle(sketch, "E9.66.0", {"center": v(-33.13, 23.3) * mm, "radius": 0.5 * mm});
            skCircle(sketch, "E9.67.0", {"center": v(-34, 22.01) * mm, "radius": 0.5 * mm});
            skCircle(sketch, "E9.68.0", {"center": v(-34.81, 20.7) * mm, "radius": 0.5 * mm});
            skCircle(sketch, "E9.69.0", {"center": v(-35.58, 19.35) * mm, "radius": 0.5 * mm});
            skCircle(sketch, "E9.70.0", {"center": v(-36.3, 17.97) * mm, "radius": 0.5 * mm});
            skCircle(sketch, "E9.71.0", {"center": v(-36.96, 16.57) * mm, "radius": 0.5 * mm});
            skCircle(sketch, "E9.72.0", {"center": v(-37.56, 15.14) * mm, "radius": 0.5 * mm});
            skCircle(sketch, "E9.73.0", {"center": v(-38.12, 13.69) * mm, "radius": 0.5 * mm});
            skCircle(sketch, "E9.74.0", {"center": v(-38.61, 12.22) * mm, "radius": 0.5 * mm});
            skCircle(sketch, "E9.75.0", {"center": v(-39.05, 10.73) * mm, "radius": 0.5 * mm});
            skCircle(sketch, "E9.76.0", {"center": v(-39.43, 9.23) * mm, "radius": 0.5 * mm});
            skCircle(sketch, "E9.77.0", {"center": v(-39.76, 7.71) * mm, "radius": 0.5 * mm});
            skCircle(sketch, "E9.78.0", {"center": v(-40.03, 6.18) * mm, "radius": 0.5 * mm});
            skCircle(sketch, "E9.79.0", {"center": v(-40.23, 4.64) * mm, "radius": 0.5 * mm});
            skCircle(sketch, "E9.80.0", {"center": v(-40.38, 3.1) * mm, "radius": 0.5 * mm});
            skCircle(sketch, "E9.81.0", {"center": v(-40.47, 1.55) * mm, "radius": 0.5 * mm});
            skCircle(sketch, "E9.82.0", {"center": v(-40.5, 0) * mm, "radius": 0.5 * mm});
            skCircle(sketch, "E9.83.0", {"center": v(-40.47, -1.55) * mm, "radius": 0.5 * mm});
            skCircle(sketch, "E9.84.0", {"center": v(-40.38, -3.1) * mm, "radius": 0.5 * mm});
            skCircle(sketch, "E9.85.0", {"center": v(-40.23, -4.64) * mm, "radius": 0.5 * mm});
            skCircle(sketch, "E9.86.0", {"center": v(-40.03, -6.18) * mm, "radius": 0.5 * mm});
            skCircle(sketch, "E9.87.0", {"center": v(-39.76, -7.71) * mm, "radius": 0.5 * mm});
            skCircle(sketch, "E9.88.0", {"center": v(-39.43, -9.23) * mm, "radius": 0.5 * mm});
            skCircle(sketch, "E9.89.0", {"center": v(-39.05, -10.73) * mm, "radius": 0.5 * mm});
            skCircle(sketch, "E9.90.0", {"center": v(-38.61, -12.22) * mm, "radius": 0.5 * mm});
            skCircle(sketch, "E9.91.0", {"center": v(-38.12, -13.69) * mm, "radius": 0.5 * mm});
            skCircle(sketch, "E9.92.0", {"center": v(-37.56, -15.14) * mm, "radius": 0.5 * mm});
            skCircle(sketch, "E9.93.0", {"center": v(-36.96, -16.57) * mm, "radius": 0.5 * mm});
            skCircle(sketch, "E9.94.0", {"center": v(-36.3, -17.97) * mm, "radius": 0.5 * mm});
            skCircle(sketch, "E9.95.0", {"center": v(-35.58, -19.35) * mm, "radius": 0.5 * mm});
            skCircle(sketch, "E9.96.0", {"center": v(-34.81, -20.7) * mm, "radius": 0.5 * mm});
            skCircle(sketch, "E9.97.0", {"center": v(-34, -22.01) * mm, "radius": 0.5 * mm});
            skCircle(sketch, "E9.98.0", {"center": v(-33.13, -23.3) * mm, "radius": 0.5 * mm});
            skCircle(sketch, "E9.99.0", {"center": v(-32.2, -24.55) * mm, "radius": 0.5 * mm});
            skCircle(sketch, "E9.100.0", {"center": v(-31.25, -25.77) * mm, "radius": 0.5 * mm});
            skCircle(sketch, "E9.101.0", {"center": v(-30.24, -26.95) * mm, "radius": 0.5 * mm});
            skCircle(sketch, "E9.102.0", {"center": v(-29.18, -28.08) * mm, "radius": 0.5 * mm});
            skCircle(sketch, "E9.103.0", {"center": v(-28.08, -29.18) * mm, "radius": 0.5 * mm});
            skCircle(sketch, "E9.104.0", {"center": v(-26.95, -30.24) * mm, "radius": 0.5 * mm});
            skCircle(sketch, "E9.105.0", {"center": v(-25.77, -31.25) * mm, "radius": 0.5 * mm});
            skCircle(sketch, "E9.106.0", {"center": v(-24.55, -32.2) * mm, "radius": 0.5 * mm});
            skCircle(sketch, "E9.107.0", {"center": v(-23.3, -33.13) * mm, "radius": 0.5 * mm});
            skCircle(sketch, "E9.108.0", {"center": v(-22.01, -34) * mm, "radius": 0.5 * mm});
            skCircle(sketch, "E9.109.0", {"center": v(-20.7, -34.81) * mm, "radius": 0.5 * mm});
            skCircle(sketch, "E9.110.0", {"center": v(-19.35, -35.58) * mm, "radius": 0.5 * mm});
            skCircle(sketch, "E9.111.0", {"center": v(-17.97, -36.3) * mm, "radius": 0.5 * mm});
            skCircle(sketch, "E9.112.0", {"center": v(-16.57, -36.96) * mm, "radius": 0.5 * mm});
            skCircle(sketch, "E9.113.0", {"center": v(-15.14, -37.56) * mm, "radius": 0.5 * mm});
            skCircle(sketch, "E9.114.0", {"center": v(-13.69, -38.12) * mm, "radius": 0.5 * mm});
            skCircle(sketch, "E9.115.0", {"center": v(-12.22, -38.61) * mm, "radius": 0.5 * mm});
            skCircle(sketch, "E9.116.0", {"center": v(-10.73, -39.05) * mm, "radius": 0.5 * mm});
            skCircle(sketch, "E9.117.0", {"center": v(-9.23, -39.43) * mm, "radius": 0.5 * mm});
            skCircle(sketch, "E9.118.0", {"center": v(-7.71, -39.76) * mm, "radius": 0.5 * mm});
            skCircle(sketch, "E9.119.0", {"center": v(-6.18, -40.03) * mm, "radius": 0.5 * mm});
            skCircle(sketch, "E9.120.0", {"center": v(-4.64, -40.23) * mm, "radius": 0.5 * mm});
            skCircle(sketch, "E9.121.0", {"center": v(-3.1, -40.38) * mm, "radius": 0.5 * mm});
            skCircle(sketch, "E9.122.0", {"center": v(-1.55, -40.47) * mm, "radius": 0.5 * mm});
            skCircle(sketch, "E9.123.0", {"center": v(0, -40.5) * mm, "radius": 0.5 * mm});
            skCircle(sketch, "E9.124.0", {"center": v(1.55, -40.47) * mm, "radius": 0.5 * mm});
            skCircle(sketch, "E9.125.0", {"center": v(3.1, -40.38) * mm, "radius": 0.5 * mm});
            skCircle(sketch, "E9.126.0", {"center": v(4.64, -40.23) * mm, "radius": 0.5 * mm});
            skCircle(sketch, "E9.127.0", {"center": v(6.18, -40.03) * mm, "radius": 0.5 * mm});
            skCircle(sketch, "E9.128.0", {"center": v(7.71, -39.76) * mm, "radius": 0.5 * mm});
            skCircle(sketch, "E9.129.0", {"center": v(9.23, -39.43) * mm, "radius": 0.5 * mm});
            skCircle(sketch, "E9.130.0", {"center": v(10.73, -39.05) * mm, "radius": 0.5 * mm});
            skCircle(sketch, "E9.131.0", {"center": v(12.22, -38.61) * mm, "radius": 0.5 * mm});
            skCircle(sketch, "E9.132.0", {"center": v(13.69, -38.12) * mm, "radius": 0.5 * mm});
            skCircle(sketch, "E9.133.0", {"center": v(15.14, -37.56) * mm, "radius": 0.5 * mm});
            skCircle(sketch, "E9.134.0", {"center": v(16.57, -36.96) * mm, "radius": 0.5 * mm});
            skCircle(sketch, "E9.135.0", {"center": v(17.97, -36.3) * mm, "radius": 0.5 * mm});
            skCircle(sketch, "E9.136.0", {"center": v(19.35, -35.58) * mm, "radius": 0.5 * mm});
            skCircle(sketch, "E9.137.0", {"center": v(20.7, -34.81) * mm, "radius": 0.5 * mm});
            skCircle(sketch, "E9.138.0", {"center": v(22.01, -34) * mm, "radius": 0.5 * mm});
            skCircle(sketch, "E9.139.0", {"center": v(23.3, -33.13) * mm, "radius": 0.5 * mm});
            skCircle(sketch, "E9.140.0", {"center": v(24.55, -32.2) * mm, "radius": 0.5 * mm});
            skCircle(sketch, "E9.141.0", {"center": v(25.77, -31.25) * mm, "radius": 0.5 * mm});
            skCircle(sketch, "E9.142.0", {"center": v(26.95, -30.24) * mm, "radius": 0.5 * mm});
            skCircle(sketch, "E9.143.0", {"center": v(28.08, -29.18) * mm, "radius": 0.5 * mm});
            skCircle(sketch, "E9.144.0", {"center": v(29.18, -28.08) * mm, "radius": 0.5 * mm});
            skCircle(sketch, "E9.145.0", {"center": v(30.24, -26.95) * mm, "radius": 0.5 * mm});
            skCircle(sketch, "E9.146.0", {"center": v(31.25, -25.77) * mm, "radius": 0.5 * mm});
            skCircle(sketch, "E9.147.0", {"center": v(32.2, -24.55) * mm, "radius": 0.5 * mm});
            skCircle(sketch, "E9.148.0", {"center": v(33.13, -23.3) * mm, "radius": 0.5 * mm});
            skCircle(sketch, "E9.149.0", {"center": v(34, -22.01) * mm, "radius": 0.5 * mm});
            skCircle(sketch, "E9.150.0", {"center": v(34.81, -20.7) * mm, "radius": 0.5 * mm});
            skCircle(sketch, "E9.151.0", {"center": v(35.58, -19.35) * mm, "radius": 0.5 * mm});
            skCircle(sketch, "E9.152.0", {"center": v(36.3, -17.97) * mm, "radius": 0.5 * mm});
            skCircle(sketch, "E9.153.0", {"center": v(36.96, -16.57) * mm, "radius": 0.5 * mm});
            skCircle(sketch, "E9.154.0", {"center": v(37.56, -15.14) * mm, "radius": 0.5 * mm});
            skCircle(sketch, "E9.155.0", {"center": v(38.12, -13.69) * mm, "radius": 0.5 * mm});
            skCircle(sketch, "E9.156.0", {"center": v(38.61, -12.22) * mm, "radius": 0.5 * mm});
            skCircle(sketch, "E9.157.0", {"center": v(39.05, -10.73) * mm, "radius": 0.5 * mm});
            skCircle(sketch, "E9.158.0", {"center": v(39.43, -9.23) * mm, "radius": 0.5 * mm});
            skCircle(sketch, "E9.159.0", {"center": v(39.76, -7.71) * mm, "radius": 0.5 * mm});
            skCircle(sketch, "E9.160.0", {"center": v(40.03, -6.18) * mm, "radius": 0.5 * mm});
            skCircle(sketch, "E9.161.0", {"center": v(40.23, -4.64) * mm, "radius": 0.5 * mm});
            skCircle(sketch, "E9.162.0", {"center": v(40.38, -3.1) * mm, "radius": 0.5 * mm});
            skCircle(sketch, "E9.163.0", {"center": v(40.47, -1.55) * mm, "radius": 0.5 * mm});
            skCircle(sketch, "E10.1.0", {"center": v(38.97, 1.58) * mm, "radius": 0.5 * mm});
            skCircle(sketch, "E10.2.0", {"center": v(38.87, 3.16) * mm, "radius": 0.5 * mm});
            skCircle(sketch, "E10.3.0", {"center": v(38.71, 4.73) * mm, "radius": 0.5 * mm});
            skCircle(sketch, "E10.4.0", {"center": v(38.49, 6.3) * mm, "radius": 0.5 * mm});
            skCircle(sketch, "E10.5.0", {"center": v(38.2, 7.85) * mm, "radius": 0.5 * mm});
            skCircle(sketch, "E10.6.0", {"center": v(37.85, 9.4) * mm, "radius": 0.5 * mm});
            skCircle(sketch, "E10.7.0", {"center": v(37.44, 10.92) * mm, "radius": 0.5 * mm});
            skCircle(sketch, "E10.8.0", {"center": v(36.97, 12.43) * mm, "radius": 0.5 * mm});
            skCircle(sketch, "E10.9.0", {"center": v(36.43, 13.91) * mm, "radius": 0.5 * mm});
            skCircle(sketch, "E10.10.0", {"center": v(35.84, 15.38) * mm, "radius": 0.5 * mm});
            skCircle(sketch, "E10.11.0", {"center": v(35.19, 16.82) * mm, "radius": 0.5 * mm});
            skCircle(sketch, "E10.12.0", {"center": v(34.48, 18.23) * mm, "radius": 0.5 * mm});
            skCircle(sketch, "E10.13.0", {"center": v(33.7, 19.61) * mm, "radius": 0.5 * mm});
            skCircle(sketch, "E10.14.0", {"center": v(32.89, 20.96) * mm, "radius": 0.5 * mm});
            skCircle(sketch, "E10.15.0", {"center": v(32, 22.28) * mm, "radius": 0.5 * mm});
            skCircle(sketch, "E10.16.0", {"center": v(31.08, 23.56) * mm, "radius": 0.5 * mm});
            skCircle(sketch, "E10.17.0", {"center": v(30.1, 24.8) * mm, "radius": 0.5 * mm});
            skCircle(sketch, "E10.18.0", {"center": v(29.07, 26) * mm, "radius": 0.5 * mm});
            skCircle(sketch, "E10.19.0", {"center": v(28, 27.15) * mm, "radius": 0.5 * mm});
            skCircle(sketch, "E10.20.0", {"center": v(26.87, 28.27) * mm, "radius": 0.5 * mm});
            skCircle(sketch, "E10.21.0", {"center": v(25.7, 29.33) * mm, "radius": 0.5 * mm});
            skCircle(sketch, "E10.22.0", {"center": v(24.5, 30.35) * mm, "radius": 0.5 * mm});
            skCircle(sketch, "E10.23.0", {"center": v(23.24, 31.32) * mm, "radius": 0.5 * mm});
            skCircle(sketch, "E10.24.0", {"center": v(21.95, 32.23) * mm, "radius": 0.5 * mm});
            skCircle(sketch, "E10.25.0", {"center": v(20.63, 33.1) * mm, "radius": 0.5 * mm});
            skCircle(sketch, "E10.26.0", {"center": v(19.27, 33.9) * mm, "radius": 0.5 * mm});
            skCircle(sketch, "E10.27.0", {"center": v(17.88, 34.66) * mm, "radius": 0.5 * mm});
            skCircle(sketch, "E10.28.0", {"center": v(16.46, 35.36) * mm, "radius": 0.5 * mm});
            skCircle(sketch, "E10.29.0", {"center": v(15.02, 36) * mm, "radius": 0.5 * mm});
            skCircle(sketch, "E10.30.0", {"center": v(13.54, 36.57) * mm, "radius": 0.5 * mm});
            skCircle(sketch, "E10.31.0", {"center": v(12.05, 37.1) * mm, "radius": 0.5 * mm});
            skCircle(sketch, "E10.32.0", {"center": v(10.54, 37.55) * mm, "radius": 0.5 * mm});
            skCircle(sketch, "E10.33.0", {"center": v(9, 37.95) * mm, "radius": 0.5 * mm});
            skCircle(sketch, "E10.34.0", {"center": v(7.46, 38.28) * mm, "radius": 0.5 * mm});
            skCircle(sketch, "E10.35.0", {"center": v(5.9, 38.55) * mm, "radius": 0.5 * mm});
            skCircle(sketch, "E10.36.0", {"center": v(4.34, 38.76) * mm, "radius": 0.5 * mm});
            skCircle(sketch, "E10.37.0", {"center": v(2.76, 38.9) * mm, "radius": 0.5 * mm});
            skCircle(sketch, "E10.38.0", {"center": v(1.19, 38.98) * mm, "radius": 0.5 * mm});
            skCircle(sketch, "E10.39.0", {"center": v(-0.4, 39) * mm, "radius": 0.5 * mm});
            skCircle(sketch, "E10.40.0", {"center": v(-1.98, 38.95) * mm, "radius": 0.5 * mm});
            skCircle(sketch, "E10.41.0", {"center": v(-3.55, 38.84) * mm, "radius": 0.5 * mm});
            skCircle(sketch, "E10.42.0", {"center": v(-5.12, 38.66) * mm, "radius": 0.5 * mm});
            skCircle(sketch, "E10.43.0", {"center": v(-6.69, 38.42) * mm, "radius": 0.5 * mm});
            skCircle(sketch, "E10.44.0", {"center": v(-8.24, 38.12) * mm, "radius": 0.5 * mm});
            skCircle(sketch, "E10.45.0", {"center": v(-9.78, 37.76) * mm, "radius": 0.5 * mm});
            skCircle(sketch, "E10.46.0", {"center": v(-11.3, 37.33) * mm, "radius": 0.5 * mm});
            skCircle(sketch, "E10.47.0", {"center": v(-12.8, 36.84) * mm, "radius": 0.5 * mm});
            skCircle(sketch, "E10.48.0", {"center": v(-14.28, 36.3) * mm, "radius": 0.5 * mm});
            skCircle(sketch, "E10.49.0", {"center": v(-15.74, 35.68) * mm, "radius": 0.5 * mm});
            skCircle(sketch, "E10.50.0", {"center": v(-17.18, 35.01) * mm, "radius": 0.5 * mm});
            skCircle(sketch, "E10.51.0", {"center": v(-18.58, 34.29) * mm, "radius": 0.5 * mm});
            skCircle(sketch, "E10.52.0", {"center": v(-19.95, 33.5) * mm, "radius": 0.5 * mm});
            skCircle(sketch, "E10.53.0", {"center": v(-21.3, 32.67) * mm, "radius": 0.5 * mm});
            skCircle(sketch, "E10.54.0", {"center": v(-22.6, 31.78) * mm, "radius": 0.5 * mm});
            skCircle(sketch, "E10.55.0", {"center": v(-23.87, 30.84) * mm, "radius": 0.5 * mm});
            skCircle(sketch, "E10.56.0", {"center": v(-25.1, 29.85) * mm, "radius": 0.5 * mm});
            skCircle(sketch, "E10.57.0", {"center": v(-26.3, 28.8) * mm, "radius": 0.5 * mm});
            skCircle(sketch, "E10.58.0", {"center": v(-27.44, 27.72) * mm, "radius": 0.5 * mm});
            skCircle(sketch, "E10.59.0", {"center": v(-28.54, 26.58) * mm, "radius": 0.5 * mm});
            skCircle(sketch, "E10.60.0", {"center": v(-29.6, 25.4) * mm, "radius": 0.5 * mm});
            skCircle(sketch, "E10.61.0", {"center": v(-30.6, 24.18) * mm, "radius": 0.5 * mm});
            skCircle(sketch, "E10.62.0", {"center": v(-31.55, 22.92) * mm, "radius": 0.5 * mm});
            skCircle(sketch, "E10.63.0", {"center": v(-32.45, 21.63) * mm, "radius": 0.5 * mm});
            skCircle(sketch, "E10.64.0", {"center": v(-33.3, 20.3) * mm, "radius": 0.5 * mm});
            skCircle(sketch, "E10.65.0", {"center": v(-34.1, 18.93) * mm, "radius": 0.5 * mm});
            skCircle(sketch, "E10.66.0", {"center": v(-34.84, 17.53) * mm, "radius": 0.5 * mm});
            skCircle(sketch, "E10.67.0", {"center": v(-35.52, 16.1) * mm, "radius": 0.5 * mm});
            skCircle(sketch, "E10.68.0", {"center": v(-36.14, 14.65) * mm, "radius": 0.5 * mm});
            skCircle(sketch, "E10.69.0", {"center": v(-36.7, 13.17) * mm, "radius": 0.5 * mm});
            skCircle(sketch, "E10.70.0", {"center": v(-37.21, 11.68) * mm, "radius": 0.5 * mm});
            skCircle(sketch, "E10.71.0", {"center": v(-37.65, 10.16) * mm, "radius": 0.5 * mm});
            skCircle(sketch, "E10.72.0", {"center": v(-38.03, 8.62) * mm, "radius": 0.5 * mm});
            skCircle(sketch, "E10.73.0", {"center": v(-38.35, 7.07) * mm, "radius": 0.5 * mm});
            skCircle(sketch, "E10.74.0", {"center": v(-38.6, 5.51) * mm, "radius": 0.5 * mm});
            skCircle(sketch, "E10.75.0", {"center": v(-38.8, 3.95) * mm, "radius": 0.5 * mm});
            skCircle(sketch, "E10.76.0", {"center": v(-38.93, 2.37) * mm, "radius": 0.5 * mm});
            skCircle(sketch, "E10.77.0", {"center": v(-39, 0.8) * mm, "radius": 0.5 * mm});
            skCircle(sketch, "E10.78.0", {"center": v(-39, -0.8) * mm, "radius": 0.5 * mm});
            skCircle(sketch, "E10.79.0", {"center": v(-38.93, -2.37) * mm, "radius": 0.5 * mm});
            skCircle(sketch, "E10.80.0", {"center": v(-38.8, -3.95) * mm, "radius": 0.5 * mm});
            skCircle(sketch, "E10.81.0", {"center": v(-38.6, -5.51) * mm, "radius": 0.5 * mm});
            skCircle(sketch, "E10.82.0", {"center": v(-38.35, -7.07) * mm, "radius": 0.5 * mm});
            skCircle(sketch, "E10.83.0", {"center": v(-38.03, -8.62) * mm, "radius": 0.5 * mm});
            skCircle(sketch, "E10.84.0", {"center": v(-37.65, -10.16) * mm, "radius": 0.5 * mm});
            skCircle(sketch, "E10.85.0", {"center": v(-37.21, -11.68) * mm, "radius": 0.5 * mm});
            skCircle(sketch, "E10.86.0", {"center": v(-36.7, -13.17) * mm, "radius": 0.5 * mm});
            skCircle(sketch, "E10.87.0", {"center": v(-36.14, -14.65) * mm, "radius": 0.5 * mm});
            skCircle(sketch, "E10.88.0", {"center": v(-35.52, -16.1) * mm, "radius": 0.5 * mm});
            skCircle(sketch, "E10.89.0", {"center": v(-34.84, -17.53) * mm, "radius": 0.5 * mm});
            skCircle(sketch, "E10.90.0", {"center": v(-34.1, -18.93) * mm, "radius": 0.5 * mm});
            skCircle(sketch, "E10.91.0", {"center": v(-33.3, -20.3) * mm, "radius": 0.5 * mm});
            skCircle(sketch, "E10.92.0", {"center": v(-32.45, -21.63) * mm, "radius": 0.5 * mm});
            skCircle(sketch, "E10.93.0", {"center": v(-31.55, -22.92) * mm, "radius": 0.5 * mm});
            skCircle(sketch, "E10.94.0", {"center": v(-30.6, -24.18) * mm, "radius": 0.5 * mm});
            skCircle(sketch, "E10.95.0", {"center": v(-29.6, -25.4) * mm, "radius": 0.5 * mm});
            skCircle(sketch, "E10.96.0", {"center": v(-28.54, -26.58) * mm, "radius": 0.5 * mm});
            skCircle(sketch, "E10.97.0", {"center": v(-27.44, -27.72) * mm, "radius": 0.5 * mm});
            skCircle(sketch, "E10.98.0", {"center": v(-26.3, -28.8) * mm, "radius": 0.5 * mm});
            skCircle(sketch, "E10.99.0", {"center": v(-25.1, -29.85) * mm, "radius": 0.5 * mm});
            skCircle(sketch, "E10.100.0", {"center": v(-23.87, -30.84) * mm, "radius": 0.5 * mm});
            skCircle(sketch, "E10.101.0", {"center": v(-22.6, -31.78) * mm, "radius": 0.5 * mm});
            skCircle(sketch, "E10.102.0", {"center": v(-21.3, -32.67) * mm, "radius": 0.5 * mm});
            skCircle(sketch, "E10.103.0", {"center": v(-19.95, -33.5) * mm, "radius": 0.5 * mm});
            skCircle(sketch, "E10.104.0", {"center": v(-18.58, -34.29) * mm, "radius": 0.5 * mm});
            skCircle(sketch, "E10.105.0", {"center": v(-17.18, -35.01) * mm, "radius": 0.5 * mm});
            skCircle(sketch, "E10.106.0", {"center": v(-15.74, -35.68) * mm, "radius": 0.5 * mm});
            skCircle(sketch, "E10.107.0", {"center": v(-14.28, -36.3) * mm, "radius": 0.5 * mm});
            skCircle(sketch, "E10.108.0", {"center": v(-12.8, -36.84) * mm, "radius": 0.5 * mm});
            skCircle(sketch, "E10.109.0", {"center": v(-11.3, -37.33) * mm, "radius": 0.5 * mm});
            skCircle(sketch, "E10.110.0", {"center": v(-9.78, -37.76) * mm, "radius": 0.5 * mm});
            skCircle(sketch, "E10.111.0", {"center": v(-8.24, -38.12) * mm, "radius": 0.5 * mm});
            skCircle(sketch, "E10.112.0", {"center": v(-6.69, -38.42) * mm, "radius": 0.5 * mm});
            skCircle(sketch, "E10.113.0", {"center": v(-5.12, -38.66) * mm, "radius": 0.5 * mm});
            skCircle(sketch, "E10.114.0", {"center": v(-3.55, -38.84) * mm, "radius": 0.5 * mm});
            skCircle(sketch, "E10.115.0", {"center": v(-1.98, -38.95) * mm, "radius": 0.5 * mm});
            skCircle(sketch, "E10.116.0", {"center": v(-0.4, -39) * mm, "radius": 0.5 * mm});
            skCircle(sketch, "E10.117.0", {"center": v(1.19, -38.98) * mm, "radius": 0.5 * mm});
            skCircle(sketch, "E10.118.0", {"center": v(2.76, -38.9) * mm, "radius": 0.5 * mm});
            skCircle(sketch, "E10.119.0", {"center": v(4.34, -38.76) * mm, "radius": 0.5 * mm});
            skCircle(sketch, "E10.120.0", {"center": v(5.9, -38.55) * mm, "radius": 0.5 * mm});
            skCircle(sketch, "E10.121.0", {"center": v(7.46, -38.28) * mm, "radius": 0.5 * mm});
            skCircle(sketch, "E10.122.0", {"center": v(9, -37.95) * mm, "radius": 0.5 * mm});
            skCircle(sketch, "E10.123.0", {"center": v(10.54, -37.55) * mm, "radius": 0.5 * mm});
            skCircle(sketch, "E10.124.0", {"center": v(12.05, -37.1) * mm, "radius": 0.5 * mm});
            skCircle(sketch, "E10.125.0", {"center": v(13.54, -36.57) * mm, "radius": 0.5 * mm});
            skCircle(sketch, "E10.126.0", {"center": v(15.02, -36) * mm, "radius": 0.5 * mm});
            skCircle(sketch, "E10.127.0", {"center": v(16.46, -35.36) * mm, "radius": 0.5 * mm});
            skCircle(sketch, "E10.128.0", {"center": v(17.88, -34.66) * mm, "radius": 0.5 * mm});
            skCircle(sketch, "E10.129.0", {"center": v(19.27, -33.9) * mm, "radius": 0.5 * mm});
            skCircle(sketch, "E10.130.0", {"center": v(20.63, -33.1) * mm, "radius": 0.5 * mm});
            skCircle(sketch, "E10.131.0", {"center": v(21.95, -32.23) * mm, "radius": 0.5 * mm});
            skCircle(sketch, "E10.132.0", {"center": v(23.24, -31.32) * mm, "radius": 0.5 * mm});
            skCircle(sketch, "E10.133.0", {"center": v(24.5, -30.35) * mm, "radius": 0.5 * mm});
            skCircle(sketch, "E10.134.0", {"center": v(25.7, -29.33) * mm, "radius": 0.5 * mm});
            skCircle(sketch, "E10.135.0", {"center": v(26.87, -28.27) * mm, "radius": 0.5 * mm});
            skCircle(sketch, "E10.136.0", {"center": v(28, -27.15) * mm, "radius": 0.5 * mm});
            skCircle(sketch, "E10.137.0", {"center": v(29.07, -26) * mm, "radius": 0.5 * mm});
            skCircle(sketch, "E10.138.0", {"center": v(30.1, -24.8) * mm, "radius": 0.5 * mm});
            skCircle(sketch, "E10.139.0", {"center": v(31.08, -23.56) * mm, "radius": 0.5 * mm});
            skCircle(sketch, "E10.140.0", {"center": v(32, -22.28) * mm, "radius": 0.5 * mm});
            skCircle(sketch, "E10.141.0", {"center": v(32.89, -20.96) * mm, "radius": 0.5 * mm});
            skCircle(sketch, "E10.142.0", {"center": v(33.7, -19.61) * mm, "radius": 0.5 * mm});
            skCircle(sketch, "E10.143.0", {"center": v(34.48, -18.23) * mm, "radius": 0.5 * mm});
            skCircle(sketch, "E10.144.0", {"center": v(35.19, -16.82) * mm, "radius": 0.5 * mm});
            skCircle(sketch, "E10.145.0", {"center": v(35.84, -15.38) * mm, "radius": 0.5 * mm});
            skCircle(sketch, "E10.146.0", {"center": v(36.43, -13.91) * mm, "radius": 0.5 * mm});
            skCircle(sketch, "E10.147.0", {"center": v(36.97, -12.43) * mm, "radius": 0.5 * mm});
            skCircle(sketch, "E10.148.0", {"center": v(37.44, -10.92) * mm, "radius": 0.5 * mm});
            skCircle(sketch, "E10.149.0", {"center": v(37.85, -9.4) * mm, "radius": 0.5 * mm});
            skCircle(sketch, "E10.150.0", {"center": v(38.2, -7.85) * mm, "radius": 0.5 * mm});
            skCircle(sketch, "E10.151.0", {"center": v(38.49, -6.3) * mm, "radius": 0.5 * mm});
            skCircle(sketch, "E10.152.0", {"center": v(38.71, -4.73) * mm, "radius": 0.5 * mm});
            skCircle(sketch, "E10.153.0", {"center": v(38.87, -3.16) * mm, "radius": 0.5 * mm});
            skCircle(sketch, "E10.154.0", {"center": v(38.97, -1.58) * mm, "radius": 0.5 * mm});
            skCircle(sketch, "E11.1.0", {"center": v(37.47, 1.61) * mm, "radius": 0.5 * mm});
            skCircle(sketch, "E11.2.0", {"center": v(37.36, 3.22) * mm, "radius": 0.5 * mm});
            skCircle(sketch, "E11.3.0", {"center": v(37.19, 4.83) * mm, "radius": 0.5 * mm});
            skCircle(sketch, "E11.4.0", {"center": v(36.95, 6.42) * mm, "radius": 0.5 * mm});
            skCircle(sketch, "E11.5.0", {"center": v(36.64, 8) * mm, "radius": 0.5 * mm});
            skCircle(sketch, "E11.6.0", {"center": v(36.26, 9.58) * mm, "radius": 0.5 * mm});
            skCircle(sketch, "E11.7.0", {"center": v(35.81, 11.13) * mm, "radius": 0.5 * mm});
            skCircle(sketch, "E11.8.0", {"center": v(35.3, 12.66) * mm, "radius": 0.5 * mm});
            skCircle(sketch, "E11.9.0", {"center": v(34.72, 14.16) * mm, "radius": 0.5 * mm});
            skCircle(sketch, "E11.10.0", {"center": v(34.08, 15.64) * mm, "radius": 0.5 * mm});
            skCircle(sketch, "E11.11.0", {"center": v(33.38, 17.1) * mm, "radius": 0.5 * mm});
            skCircle(sketch, "E11.12.0", {"center": v(32.6, 18.52) * mm, "radius": 0.5 * mm});
            skCircle(sketch, "E11.13.0", {"center": v(31.78, 19.9) * mm, "radius": 0.5 * mm});
            skCircle(sketch, "E11.14.0", {"center": v(30.9, 21.25) * mm, "radius": 0.5 * mm});
            skCircle(sketch, "E11.15.0", {"center": v(29.95, 22.56) * mm, "radius": 0.5 * mm});
            skCircle(sketch, "E11.16.0", {"center": v(28.96, 23.83) * mm, "radius": 0.5 * mm});
            skCircle(sketch, "E11.17.0", {"center": v(27.9, 25.05) * mm, "radius": 0.5 * mm});
            skCircle(sketch, "E11.18.0", {"center": v(26.8, 26.23) * mm, "radius": 0.5 * mm});
            skCircle(sketch, "E11.19.0", {"center": v(25.65, 27.36) * mm, "radius": 0.5 * mm});
            skCircle(sketch, "E11.20.0", {"center": v(24.45, 28.44) * mm, "radius": 0.5 * mm});
            skCircle(sketch, "E11.21.0", {"center": v(23.2, 29.46) * mm, "radius": 0.5 * mm});
            skCircle(sketch, "E11.22.0", {"center": v(21.91, 30.43) * mm, "radius": 0.5 * mm});
            skCircle(sketch, "E11.23.0", {"center": v(20.58, 31.35) * mm, "radius": 0.5 * mm});
            skCircle(sketch, "E11.24.0", {"center": v(19.21, 32.2) * mm, "radius": 0.5 * mm});
            skCircle(sketch, "E11.25.0", {"center": v(17.81, 33) * mm, "radius": 0.5 * mm});
            skCircle(sketch, "E11.26.0", {"center": v(16.37, 33.74) * mm, "radius": 0.5 * mm});
            skCircle(sketch, "E11.27.0", {"center": v(14.9, 34.4) * mm, "radius": 0.5 * mm});
            skCircle(sketch, "E11.28.0", {"center": v(13.41, 35.02) * mm, "radius": 0.5 * mm});
            skCircle(sketch, "E11.29.0", {"center": v(11.9, 35.56) * mm, "radius": 0.5 * mm});
            skCircle(sketch, "E11.30.0", {"center": v(10.35, 36.04) * mm, "radius": 0.5 * mm});
            skCircle(sketch, "E11.31.0", {"center": v(8.8, 36.45) * mm, "radius": 0.5 * mm});
            skCircle(sketch, "E11.32.0", {"center": v(7.22, 36.8) * mm, "radius": 0.5 * mm});
            skCircle(sketch, "E11.33.0", {"center": v(5.63, 37.08) * mm, "radius": 0.5 * mm});
            skCircle(sketch, "E11.34.0", {"center": v(4.03, 37.28) * mm, "radius": 0.5 * mm});
            skCircle(sketch, "E11.35.0", {"center": v(2.42, 37.42) * mm, "radius": 0.5 * mm});
            skCircle(sketch, "E11.36.0", {"center": v(0.8, 37.5) * mm, "radius": 0.5 * mm});
            skCircle(sketch, "E11.37.0", {"center": v(-0.8, 37.5) * mm, "radius": 0.5 * mm});
            skCircle(sketch, "E11.38.0", {"center": v(-2.42, 37.42) * mm, "radius": 0.5 * mm});
            skCircle(sketch, "E11.39.0", {"center": v(-4.03, 37.28) * mm, "radius": 0.5 * mm});
            skCircle(sketch, "E11.40.0", {"center": v(-5.63, 37.08) * mm, "radius": 0.5 * mm});
            skCircle(sketch, "E11.41.0", {"center": v(-7.22, 36.8) * mm, "radius": 0.5 * mm});
            skCircle(sketch, "E11.42.0", {"center": v(-8.8, 36.45) * mm, "radius": 0.5 * mm});
            skCircle(sketch, "E11.43.0", {"center": v(-10.35, 36.04) * mm, "radius": 0.5 * mm});
            skCircle(sketch, "E11.44.0", {"center": v(-11.9, 35.56) * mm, "radius": 0.5 * mm});
            skCircle(sketch, "E11.45.0", {"center": v(-13.41, 35.02) * mm, "radius": 0.5 * mm});
            skCircle(sketch, "E11.46.0", {"center": v(-14.9, 34.4) * mm, "radius": 0.5 * mm});
            skCircle(sketch, "E11.47.0", {"center": v(-16.37, 33.74) * mm, "radius": 0.5 * mm});
            skCircle(sketch, "E11.48.0", {"center": v(-17.81, 33) * mm, "radius": 0.5 * mm});
            skCircle(sketch, "E11.49.0", {"center": v(-19.21, 32.2) * mm, "radius": 0.5 * mm});
            skCircle(sketch, "E11.50.0", {"center": v(-20.58, 31.35) * mm, "radius": 0.5 * mm});
            skCircle(sketch, "E11.51.0", {"center": v(-21.91, 30.43) * mm, "radius": 0.5 * mm});
            skCircle(sketch, "E11.52.0", {"center": v(-23.2, 29.46) * mm, "radius": 0.5 * mm});
            skCircle(sketch, "E11.53.0", {"center": v(-24.45, 28.44) * mm, "radius": 0.5 * mm});
            skCircle(sketch, "E11.54.0", {"center": v(-25.65, 27.36) * mm, "radius": 0.5 * mm});
            skCircle(sketch, "E11.55.0", {"center": v(-26.8, 26.23) * mm, "radius": 0.5 * mm});
            skCircle(sketch, "E11.56.0", {"center": v(-27.9, 25.05) * mm, "radius": 0.5 * mm});
            skCircle(sketch, "E11.57.0", {"center": v(-28.96, 23.83) * mm, "radius": 0.5 * mm});
            skCircle(sketch, "E11.58.0", {"center": v(-29.95, 22.56) * mm, "radius": 0.5 * mm});
            skCircle(sketch, "E11.59.0", {"center": v(-30.9, 21.25) * mm, "radius": 0.5 * mm});
            skCircle(sketch, "E11.60.0", {"center": v(-31.78, 19.9) * mm, "radius": 0.5 * mm});
            skCircle(sketch, "E11.61.0", {"center": v(-32.6, 18.52) * mm, "radius": 0.5 * mm});
            skCircle(sketch, "E11.62.0", {"center": v(-33.38, 17.1) * mm, "radius": 0.5 * mm});
            skCircle(sketch, "E11.63.0", {"center": v(-34.08, 15.64) * mm, "radius": 0.5 * mm});
            skCircle(sketch, "E11.64.0", {"center": v(-34.72, 14.16) * mm, "radius": 0.5 * mm});
            skCircle(sketch, "E11.65.0", {"center": v(-35.3, 12.66) * mm, "radius": 0.5 * mm});
            skCircle(sketch, "E11.66.0", {"center": v(-35.81, 11.13) * mm, "radius": 0.5 * mm});
            skCircle(sketch, "E11.67.0", {"center": v(-36.26, 9.58) * mm, "radius": 0.5 * mm});
            skCircle(sketch, "E11.68.0", {"center": v(-36.64, 8) * mm, "radius": 0.5 * mm});
            skCircle(sketch, "E11.69.0", {"center": v(-36.95, 6.42) * mm, "radius": 0.5 * mm});
            skCircle(sketch, "E11.70.0", {"center": v(-37.19, 4.83) * mm, "radius": 0.5 * mm});
            skCircle(sketch, "E11.71.0", {"center": v(-37.36, 3.22) * mm, "radius": 0.5 * mm});
            skCircle(sketch, "E11.72.0", {"center": v(-37.47, 1.61) * mm, "radius": 0.5 * mm});
            skCircle(sketch, "E11.73.0", {"center": v(-37.5, 0) * mm, "radius": 0.5 * mm});
            skCircle(sketch, "E11.74.0", {"center": v(-37.47, -1.61) * mm, "radius": 0.5 * mm});
            skCircle(sketch, "E11.75.0", {"center": v(-37.36, -3.22) * mm, "radius": 0.5 * mm});
            skCircle(sketch, "E11.76.0", {"center": v(-37.19, -4.83) * mm, "radius": 0.5 * mm});
            skCircle(sketch, "E11.77.0", {"center": v(-36.95, -6.42) * mm, "radius": 0.5 * mm});
            skCircle(sketch, "E11.78.0", {"center": v(-36.64, -8) * mm, "radius": 0.5 * mm});
            skCircle(sketch, "E11.79.0", {"center": v(-36.26, -9.58) * mm, "radius": 0.5 * mm});
            skCircle(sketch, "E11.80.0", {"center": v(-35.81, -11.13) * mm, "radius": 0.5 * mm});
            skCircle(sketch, "E11.81.0", {"center": v(-35.3, -12.66) * mm, "radius": 0.5 * mm});
            skCircle(sketch, "E11.82.0", {"center": v(-34.72, -14.16) * mm, "radius": 0.5 * mm});
            skCircle(sketch, "E11.83.0", {"center": v(-34.08, -15.64) * mm, "radius": 0.5 * mm});
            skCircle(sketch, "E11.84.0", {"center": v(-33.38, -17.1) * mm, "radius": 0.5 * mm});
            skCircle(sketch, "E11.85.0", {"center": v(-32.6, -18.52) * mm, "radius": 0.5 * mm});
            skCircle(sketch, "E11.86.0", {"center": v(-31.78, -19.9) * mm, "radius": 0.5 * mm});
            skCircle(sketch, "E11.87.0", {"center": v(-30.9, -21.25) * mm, "radius": 0.5 * mm});
            skCircle(sketch, "E11.88.0", {"center": v(-29.95, -22.56) * mm, "radius": 0.5 * mm});
            skCircle(sketch, "E11.89.0", {"center": v(-28.96, -23.83) * mm, "radius": 0.5 * mm});
            skCircle(sketch, "E11.90.0", {"center": v(-27.9, -25.05) * mm, "radius": 0.5 * mm});
            skCircle(sketch, "E11.91.0", {"center": v(-26.8, -26.23) * mm, "radius": 0.5 * mm});
            skCircle(sketch, "E11.92.0", {"center": v(-25.65, -27.36) * mm, "radius": 0.5 * mm});
            skCircle(sketch, "E11.93.0", {"center": v(-24.45, -28.44) * mm, "radius": 0.5 * mm});
            skCircle(sketch, "E11.94.0", {"center": v(-23.2, -29.46) * mm, "radius": 0.5 * mm});
            skCircle(sketch, "E11.95.0", {"center": v(-21.91, -30.43) * mm, "radius": 0.5 * mm});
            skCircle(sketch, "E11.96.0", {"center": v(-20.58, -31.35) * mm, "radius": 0.5 * mm});
            skCircle(sketch, "E11.97.0", {"center": v(-19.21, -32.2) * mm, "radius": 0.5 * mm});
            skCircle(sketch, "E11.98.0", {"center": v(-17.81, -33) * mm, "radius": 0.5 * mm});
            skCircle(sketch, "E11.99.0", {"center": v(-16.37, -33.74) * mm, "radius": 0.5 * mm});
            skCircle(sketch, "E11.100.0", {"center": v(-14.9, -34.4) * mm, "radius": 0.5 * mm});
            skCircle(sketch, "E11.101.0", {"center": v(-13.41, -35.02) * mm, "radius": 0.5 * mm});
            skCircle(sketch, "E11.102.0", {"center": v(-11.9, -35.56) * mm, "radius": 0.5 * mm});
            skCircle(sketch, "E11.103.0", {"center": v(-10.35, -36.04) * mm, "radius": 0.5 * mm});
            skCircle(sketch, "E11.104.0", {"center": v(-8.8, -36.45) * mm, "radius": 0.5 * mm});
            skCircle(sketch, "E11.105.0", {"center": v(-7.22, -36.8) * mm, "radius": 0.5 * mm});
            skCircle(sketch, "E11.106.0", {"center": v(-5.63, -37.08) * mm, "radius": 0.5 * mm});
            skCircle(sketch, "E11.107.0", {"center": v(-4.03, -37.28) * mm, "radius": 0.5 * mm});
            skCircle(sketch, "E11.108.0", {"center": v(-2.42, -37.42) * mm, "radius": 0.5 * mm});
            skCircle(sketch, "E11.109.0", {"center": v(-0.8, -37.5) * mm, "radius": 0.5 * mm});
            skCircle(sketch, "E11.110.0", {"center": v(0.8, -37.5) * mm, "radius": 0.5 * mm});
            skCircle(sketch, "E11.111.0", {"center": v(2.42, -37.42) * mm, "radius": 0.5 * mm});
            skCircle(sketch, "E11.112.0", {"center": v(4.03, -37.28) * mm, "radius": 0.5 * mm});
            skCircle(sketch, "E11.113.0", {"center": v(5.63, -37.08) * mm, "radius": 0.5 * mm});
            skCircle(sketch, "E11.114.0", {"center": v(7.22, -36.8) * mm, "radius": 0.5 * mm});
            skCircle(sketch, "E11.115.0", {"center": v(8.8, -36.45) * mm, "radius": 0.5 * mm});
            skCircle(sketch, "E11.116.0", {"center": v(10.35, -36.04) * mm, "radius": 0.5 * mm});
            skCircle(sketch, "E11.117.0", {"center": v(11.9, -35.56) * mm, "radius": 0.5 * mm});
            skCircle(sketch, "E11.118.0", {"center": v(13.41, -35.02) * mm, "radius": 0.5 * mm});
            skCircle(sketch, "E11.119.0", {"center": v(14.9, -34.4) * mm, "radius": 0.5 * mm});
            skCircle(sketch, "E11.120.0", {"center": v(16.37, -33.74) * mm, "radius": 0.5 * mm});
            skCircle(sketch, "E11.121.0", {"center": v(17.81, -33) * mm, "radius": 0.5 * mm});
            skCircle(sketch, "E11.122.0", {"center": v(19.21, -32.2) * mm, "radius": 0.5 * mm});
            skCircle(sketch, "E11.123.0", {"center": v(20.58, -31.35) * mm, "radius": 0.5 * mm});
            skCircle(sketch, "E11.124.0", {"center": v(21.91, -30.43) * mm, "radius": 0.5 * mm});
            skCircle(sketch, "E11.125.0", {"center": v(23.2, -29.46) * mm, "radius": 0.5 * mm});
            skCircle(sketch, "E11.126.0", {"center": v(24.45, -28.44) * mm, "radius": 0.5 * mm});
            skCircle(sketch, "E11.127.0", {"center": v(25.65, -27.36) * mm, "radius": 0.5 * mm});
            skCircle(sketch, "E11.128.0", {"center": v(26.8, -26.23) * mm, "radius": 0.5 * mm});
            skCircle(sketch, "E11.129.0", {"center": v(27.9, -25.05) * mm, "radius": 0.5 * mm});
            skCircle(sketch, "E11.130.0", {"center": v(28.96, -23.83) * mm, "radius": 0.5 * mm});
            skCircle(sketch, "E11.131.0", {"center": v(29.95, -22.56) * mm, "radius": 0.5 * mm});
            skCircle(sketch, "E11.132.0", {"center": v(30.9, -21.25) * mm, "radius": 0.5 * mm});
            skCircle(sketch, "E11.133.0", {"center": v(31.78, -19.9) * mm, "radius": 0.5 * mm});
            skCircle(sketch, "E11.134.0", {"center": v(32.6, -18.52) * mm, "radius": 0.5 * mm});
            skCircle(sketch, "E11.135.0", {"center": v(33.38, -17.1) * mm, "radius": 0.5 * mm});
            skCircle(sketch, "E11.136.0", {"center": v(34.08, -15.64) * mm, "radius": 0.5 * mm});
            skCircle(sketch, "E11.137.0", {"center": v(34.72, -14.16) * mm, "radius": 0.5 * mm});
            skCircle(sketch, "E11.138.0", {"center": v(35.3, -12.66) * mm, "radius": 0.5 * mm});
            skCircle(sketch, "E11.139.0", {"center": v(35.81, -11.13) * mm, "radius": 0.5 * mm});
            skCircle(sketch, "E11.140.0", {"center": v(36.26, -9.58) * mm, "radius": 0.5 * mm});
            skCircle(sketch, "E11.141.0", {"center": v(36.64, -8) * mm, "radius": 0.5 * mm});
            skCircle(sketch, "E11.142.0", {"center": v(36.95, -6.42) * mm, "radius": 0.5 * mm});
            skCircle(sketch, "E11.143.0", {"center": v(37.19, -4.83) * mm, "radius": 0.5 * mm});
            skCircle(sketch, "E11.144.0", {"center": v(37.36, -3.22) * mm, "radius": 0.5 * mm});
            skCircle(sketch, "E11.145.0", {"center": v(37.47, -1.61) * mm, "radius": 0.5 * mm});
            skCircle(sketch, "E12.1.0", {"center": v(35.96, 1.65) * mm, "radius": 0.5 * mm});
            skCircle(sketch, "E12.2.0", {"center": v(35.85, 3.3) * mm, "radius": 0.5 * mm});
            skCircle(sketch, "E12.3.0", {"center": v(35.66, 4.94) * mm, "radius": 0.5 * mm});
            skCircle(sketch, "E12.4.0", {"center": v(35.4, 6.57) * mm, "radius": 0.5 * mm});
            skCircle(sketch, "E12.5.0", {"center": v(35.06, 8.18) * mm, "radius": 0.5 * mm});
            skCircle(sketch, "E12.6.0", {"center": v(34.65, 9.78) * mm, "radius": 0.5 * mm});
            skCircle(sketch, "E12.7.0", {"center": v(34.16, 11.36) * mm, "radius": 0.5 * mm});
            skCircle(sketch, "E12.8.0", {"center": v(33.6, 12.91) * mm, "radius": 0.5 * mm});
            skCircle(sketch, "E12.9.0", {"center": v(32.98, 14.44) * mm, "radius": 0.5 * mm});
            skCircle(sketch, "E12.10.0", {"center": v(32.28, 15.94) * mm, "radius": 0.5 * mm});
            skCircle(sketch, "E12.11.0", {"center": v(31.52, 17.4) * mm, "radius": 0.5 * mm});
            skCircle(sketch, "E12.12.0", {"center": v(30.68, 18.83) * mm, "radius": 0.5 * mm});
            skCircle(sketch, "E12.13.0", {"center": v(29.79, 20.21) * mm, "radius": 0.5 * mm});
            skCircle(sketch, "E12.14.0", {"center": v(28.83, 21.56) * mm, "radius": 0.5 * mm});
            skCircle(sketch, "E12.15.0", {"center": v(27.81, 22.86) * mm, "radius": 0.5 * mm});
            skCircle(sketch, "E12.16.0", {"center": v(26.73, 24.1) * mm, "radius": 0.5 * mm});
            skCircle(sketch, "E12.17.0", {"center": v(25.6, 25.3) * mm, "radius": 0.5 * mm});
            skCircle(sketch, "E12.18.0", {"center": v(24.41, 26.46) * mm, "radius": 0.5 * mm});
            skCircle(sketch, "E12.19.0", {"center": v(23.18, 27.55) * mm, "radius": 0.5 * mm});
            skCircle(sketch, "E12.20.0", {"center": v(21.89, 28.58) * mm, "radius": 0.5 * mm});
            skCircle(sketch, "E12.21.0", {"center": v(20.55, 29.56) * mm, "radius": 0.5 * mm});
            skCircle(sketch, "E12.22.0", {"center": v(19.18, 30.47) * mm, "radius": 0.5 * mm});
            skCircle(sketch, "E12.23.0", {"center": v(17.76, 31.31) * mm, "radius": 0.5 * mm});
            skCircle(sketch, "E12.24.0", {"center": v(16.3, 32.1) * mm, "radius": 0.5 * mm});
            skCircle(sketch, "E12.25.0", {"center": v(14.82, 32.8) * mm, "radius": 0.5 * mm});
            skCircle(sketch, "E12.26.0", {"center": v(13.3, 33.45) * mm, "radius": 0.5 * mm});
            skCircle(sketch, "E12.27.0", {"center": v(11.75, 34.03) * mm, "radius": 0.5 * mm});
            skCircle(sketch, "E12.28.0", {"center": v(10.18, 34.53) * mm, "radius": 0.5 * mm});
            skCircle(sketch, "E12.29.0", {"center": v(8.58, 34.96) * mm, "radius": 0.5 * mm});
            skCircle(sketch, "E12.30.0", {"center": v(6.97, 35.32) * mm, "radius": 0.5 * mm});
            skCircle(sketch, "E12.31.0", {"center": v(5.35, 35.6) * mm, "radius": 0.5 * mm});
            skCircle(sketch, "E12.32.0", {"center": v(3.7, 35.8) * mm, "radius": 0.5 * mm});
            skCircle(sketch, "E12.33.0", {"center": v(2.06, 35.94) * mm, "radius": 0.5 * mm});
            skCircle(sketch, "E12.34.0", {"center": v(0.41, 36) * mm, "radius": 0.5 * mm});
            skCircle(sketch, "E12.35.0", {"center": v(-1.24, 35.98) * mm, "radius": 0.5 * mm});
            skCircle(sketch, "E12.36.0", {"center": v(-2.89, 35.88) * mm, "radius": 0.5 * mm});
            skCircle(sketch, "E12.37.0", {"center": v(-4.53, 35.71) * mm, "radius": 0.5 * mm});
            skCircle(sketch, "E12.38.0", {"center": v(-6.16, 35.47) * mm, "radius": 0.5 * mm});
            skCircle(sketch, "E12.39.0", {"center": v(-7.78, 35.15) * mm, "radius": 0.5 * mm});
            skCircle(sketch, "E12.40.0", {"center": v(-9.38, 34.76) * mm, "radius": 0.5 * mm});
            skCircle(sketch, "E12.41.0", {"center": v(-10.97, 34.29) * mm, "radius": 0.5 * mm});
            skCircle(sketch, "E12.42.0", {"center": v(-12.53, 33.75) * mm, "radius": 0.5 * mm});
            skCircle(sketch, "E12.43.0", {"center": v(-14.06, 33.14) * mm, "radius": 0.5 * mm});
            skCircle(sketch, "E12.44.0", {"center": v(-15.57, 32.46) * mm, "radius": 0.5 * mm});
            skCircle(sketch, "E12.45.0", {"center": v(-17.04, 31.71) * mm, "radius": 0.5 * mm});
            skCircle(sketch, "E12.46.0", {"center": v(-18.47, 30.9) * mm, "radius": 0.5 * mm});
            skCircle(sketch, "E12.47.0", {"center": v(-19.87, 30.02) * mm, "radius": 0.5 * mm});
            skCircle(sketch, "E12.48.0", {"center": v(-21.23, 29.08) * mm, "radius": 0.5 * mm});
            skCircle(sketch, "E12.49.0", {"center": v(-22.54, 28.07) * mm, "radius": 0.5 * mm});
            skCircle(sketch, "E12.50.0", {"center": v(-23.8, 27) * mm, "radius": 0.5 * mm});
            skCircle(sketch, "E12.51.0", {"center": v(-25.01, 25.89) * mm, "radius": 0.5 * mm});
            skCircle(sketch, "E12.52.0", {"center": v(-26.17, 24.72) * mm, "radius": 0.5 * mm});
            skCircle(sketch, "E12.53.0", {"center": v(-27.28, 23.49) * mm, "radius": 0.5 * mm});
            skCircle(sketch, "E12.54.0", {"center": v(-28.33, 22.21) * mm, "radius": 0.5 * mm});
            skCircle(sketch, "E12.55.0", {"center": v(-29.32, 20.9) * mm, "radius": 0.5 * mm});
            skCircle(sketch, "E12.56.0", {"center": v(-30.24, 19.53) * mm, "radius": 0.5 * mm});
            skCircle(sketch, "E12.57.0", {"center": v(-31.1, 18.12) * mm, "radius": 0.5 * mm});
            skCircle(sketch, "E12.58.0", {"center": v(-31.9, 16.67) * mm, "radius": 0.5 * mm});
            skCircle(sketch, "E12.59.0", {"center": v(-32.64, 15.2) * mm, "radius": 0.5 * mm});
            skCircle(sketch, "E12.60.0", {"center": v(-33.3, 13.68) * mm, "radius": 0.5 * mm});
            skCircle(sketch, "E12.61.0", {"center": v(-33.9, 12.14) * mm, "radius": 0.5 * mm});
            skCircle(sketch, "E12.62.0", {"center": v(-34.41, 10.57) * mm, "radius": 0.5 * mm});
            skCircle(sketch, "E12.63.0", {"center": v(-34.86, 8.98) * mm, "radius": 0.5 * mm});
            skCircle(sketch, "E12.64.0", {"center": v(-35.24, 7.38) * mm, "radius": 0.5 * mm});
            skCircle(sketch, "E12.65.0", {"center": v(-35.54, 5.75) * mm, "radius": 0.5 * mm});
            skCircle(sketch, "E12.66.0", {"center": v(-35.76, 4.12) * mm, "radius": 0.5 * mm});
            skCircle(sketch, "E12.67.0", {"center": v(-35.91, 2.47) * mm, "radius": 0.5 * mm});
            skCircle(sketch, "E12.68.0", {"center": v(-36, 0.83) * mm, "radius": 0.5 * mm});
            skCircle(sketch, "E12.69.0", {"center": v(-36, -0.83) * mm, "radius": 0.5 * mm});
            skCircle(sketch, "E12.70.0", {"center": v(-35.91, -2.47) * mm, "radius": 0.5 * mm});
            skCircle(sketch, "E12.71.0", {"center": v(-35.76, -4.12) * mm, "radius": 0.5 * mm});
            skCircle(sketch, "E12.72.0", {"center": v(-35.54, -5.75) * mm, "radius": 0.5 * mm});
            skCircle(sketch, "E12.73.0", {"center": v(-35.24, -7.38) * mm, "radius": 0.5 * mm});
            skCircle(sketch, "E12.74.0", {"center": v(-34.86, -8.98) * mm, "radius": 0.5 * mm});
            skCircle(sketch, "E12.75.0", {"center": v(-34.41, -10.57) * mm, "radius": 0.5 * mm});
            skCircle(sketch, "E12.76.0", {"center": v(-33.9, -12.14) * mm, "radius": 0.5 * mm});
            skCircle(sketch, "E12.77.0", {"center": v(-33.3, -13.68) * mm, "radius": 0.5 * mm});
            skCircle(sketch, "E12.78.0", {"center": v(-32.64, -15.2) * mm, "radius": 0.5 * mm});
            skCircle(sketch, "E12.79.0", {"center": v(-31.9, -16.67) * mm, "radius": 0.5 * mm});
            skCircle(sketch, "E12.80.0", {"center": v(-31.1, -18.12) * mm, "radius": 0.5 * mm});
            skCircle(sketch, "E12.81.0", {"center": v(-30.24, -19.53) * mm, "radius": 0.5 * mm});
            skCircle(sketch, "E12.82.0", {"center": v(-29.32, -20.9) * mm, "radius": 0.5 * mm});
            skCircle(sketch, "E12.83.0", {"center": v(-28.33, -22.21) * mm, "radius": 0.5 * mm});
            skCircle(sketch, "E12.84.0", {"center": v(-27.28, -23.49) * mm, "radius": 0.5 * mm});
            skCircle(sketch, "E12.85.0", {"center": v(-26.17, -24.72) * mm, "radius": 0.5 * mm});
            skCircle(sketch, "E12.86.0", {"center": v(-25.01, -25.89) * mm, "radius": 0.5 * mm});
            skCircle(sketch, "E12.87.0", {"center": v(-23.8, -27) * mm, "radius": 0.5 * mm});
            skCircle(sketch, "E12.88.0", {"center": v(-22.54, -28.07) * mm, "radius": 0.5 * mm});
            skCircle(sketch, "E12.89.0", {"center": v(-21.23, -29.08) * mm, "radius": 0.5 * mm});
            skCircle(sketch, "E12.90.0", {"center": v(-19.87, -30.02) * mm, "radius": 0.5 * mm});
            skCircle(sketch, "E12.91.0", {"center": v(-18.47, -30.9) * mm, "radius": 0.5 * mm});
            skCircle(sketch, "E12.92.0", {"center": v(-17.04, -31.71) * mm, "radius": 0.5 * mm});
            skCircle(sketch, "E12.93.0", {"center": v(-15.57, -32.46) * mm, "radius": 0.5 * mm});
            skCircle(sketch, "E12.94.0", {"center": v(-14.06, -33.14) * mm, "radius": 0.5 * mm});
            skCircle(sketch, "E12.95.0", {"center": v(-12.53, -33.75) * mm, "radius": 0.5 * mm});
            skCircle(sketch, "E12.96.0", {"center": v(-10.97, -34.29) * mm, "radius": 0.5 * mm});
            skCircle(sketch, "E12.97.0", {"center": v(-9.38, -34.76) * mm, "radius": 0.5 * mm});
            skCircle(sketch, "E12.98.0", {"center": v(-7.78, -35.15) * mm, "radius": 0.5 * mm});
            skCircle(sketch, "E12.99.0", {"center": v(-6.16, -35.47) * mm, "radius": 0.5 * mm});
            skCircle(sketch, "E12.100.0", {"center": v(-4.53, -35.71) * mm, "radius": 0.5 * mm});
            skCircle(sketch, "E12.101.0", {"center": v(-2.89, -35.88) * mm, "radius": 0.5 * mm});
            skCircle(sketch, "E12.102.0", {"center": v(-1.24, -35.98) * mm, "radius": 0.5 * mm});
            skCircle(sketch, "E12.103.0", {"center": v(0.41, -36) * mm, "radius": 0.5 * mm});
            skCircle(sketch, "E12.104.0", {"center": v(2.06, -35.94) * mm, "radius": 0.5 * mm});
            skCircle(sketch, "E12.105.0", {"center": v(3.7, -35.8) * mm, "radius": 0.5 * mm});
            skCircle(sketch, "E12.106.0", {"center": v(5.35, -35.6) * mm, "radius": 0.5 * mm});
            skCircle(sketch, "E12.107.0", {"center": v(6.97, -35.32) * mm, "radius": 0.5 * mm});
            skCircle(sketch, "E12.108.0", {"center": v(8.58, -34.96) * mm, "radius": 0.5 * mm});
            skCircle(sketch, "E12.109.0", {"center": v(10.18, -34.53) * mm, "radius": 0.5 * mm});
            skCircle(sketch, "E12.110.0", {"center": v(11.75, -34.03) * mm, "radius": 0.5 * mm});
            skCircle(sketch, "E12.111.0", {"center": v(13.3, -33.45) * mm, "radius": 0.5 * mm});
            skCircle(sketch, "E12.112.0", {"center": v(14.82, -32.8) * mm, "radius": 0.5 * mm});
            skCircle(sketch, "E12.113.0", {"center": v(16.3, -32.1) * mm, "radius": 0.5 * mm});
            skCircle(sketch, "E12.114.0", {"center": v(17.76, -31.31) * mm, "radius": 0.5 * mm});
            skCircle(sketch, "E12.115.0", {"center": v(19.18, -30.47) * mm, "radius": 0.5 * mm});
            skCircle(sketch, "E12.116.0", {"center": v(20.55, -29.56) * mm, "radius": 0.5 * mm});
            skCircle(sketch, "E12.117.0", {"center": v(21.89, -28.58) * mm, "radius": 0.5 * mm});
            skCircle(sketch, "E12.118.0", {"center": v(23.18, -27.55) * mm, "radius": 0.5 * mm});
            skCircle(sketch, "E12.119.0", {"center": v(24.41, -26.46) * mm, "radius": 0.5 * mm});
            skCircle(sketch, "E12.120.0", {"center": v(25.6, -25.3) * mm, "radius": 0.5 * mm});
            skCircle(sketch, "E12.121.0", {"center": v(26.73, -24.1) * mm, "radius": 0.5 * mm});
            skCircle(sketch, "E12.122.0", {"center": v(27.81, -22.86) * mm, "radius": 0.5 * mm});
            skCircle(sketch, "E12.123.0", {"center": v(28.83, -21.56) * mm, "radius": 0.5 * mm});
            skCircle(sketch, "E12.124.0", {"center": v(29.79, -20.21) * mm, "radius": 0.5 * mm});
            skCircle(sketch, "E12.125.0", {"center": v(30.68, -18.83) * mm, "radius": 0.5 * mm});
            skCircle(sketch, "E12.126.0", {"center": v(31.52, -17.4) * mm, "radius": 0.5 * mm});
            skCircle(sketch, "E12.127.0", {"center": v(32.28, -15.94) * mm, "radius": 0.5 * mm});
            skCircle(sketch, "E12.128.0", {"center": v(32.98, -14.44) * mm, "radius": 0.5 * mm});
            skCircle(sketch, "E12.129.0", {"center": v(33.6, -12.91) * mm, "radius": 0.5 * mm});
            skCircle(sketch, "E12.130.0", {"center": v(34.16, -11.36) * mm, "radius": 0.5 * mm});
            skCircle(sketch, "E12.131.0", {"center": v(34.65, -9.78) * mm, "radius": 0.5 * mm});
            skCircle(sketch, "E12.132.0", {"center": v(35.06, -8.18) * mm, "radius": 0.5 * mm});
            skCircle(sketch, "E12.133.0", {"center": v(35.4, -6.57) * mm, "radius": 0.5 * mm});
            skCircle(sketch, "E12.134.0", {"center": v(35.66, -4.94) * mm, "radius": 0.5 * mm});
            skCircle(sketch, "E12.135.0", {"center": v(35.85, -3.3) * mm, "radius": 0.5 * mm});
            skCircle(sketch, "E12.136.0", {"center": v(35.96, -1.65) * mm, "radius": 0.5 * mm});
            skCircle(sketch, "E13.1.0", {"center": v(34.46, 1.7) * mm, "radius": 0.5 * mm});
            skCircle(sketch, "E13.2.0", {"center": v(34.33, 3.38) * mm, "radius": 0.5 * mm});
            skCircle(sketch, "E13.3.0", {"center": v(34.13, 5.06) * mm, "radius": 0.5 * mm});
            skCircle(sketch, "E13.4.0", {"center": v(33.84, 6.73) * mm, "radius": 0.5 * mm});
            skCircle(sketch, "E13.5.0", {"center": v(33.47, 8.38) * mm, "radius": 0.5 * mm});
            skCircle(sketch, "E13.6.0", {"center": v(33.01, 10.01) * mm, "radius": 0.5 * mm});
            skCircle(sketch, "E13.7.0", {"center": v(32.48, 11.62) * mm, "radius": 0.5 * mm});
            skCircle(sketch, "E13.8.0", {"center": v(31.87, 13.2) * mm, "radius": 0.5 * mm});
            skCircle(sketch, "E13.9.0", {"center": v(31.19, 14.75) * mm, "radius": 0.5 * mm});
            skCircle(sketch, "E13.10.0", {"center": v(30.43, 16.26) * mm, "radius": 0.5 * mm});
            skCircle(sketch, "E13.11.0", {"center": v(29.6, 17.74) * mm, "radius": 0.5 * mm});
            skCircle(sketch, "E13.12.0", {"center": v(28.69, 19.17) * mm, "radius": 0.5 * mm});
            skCircle(sketch, "E13.13.0", {"center": v(27.71, 20.55) * mm, "radius": 0.5 * mm});
            skCircle(sketch, "E13.14.0", {"center": v(26.67, 21.89) * mm, "radius": 0.5 * mm});
            skCircle(sketch, "E13.15.0", {"center": v(25.56, 23.17) * mm, "radius": 0.5 * mm});
            skCircle(sketch, "E13.16.0", {"center": v(24.4, 24.4) * mm, "radius": 0.5 * mm});
            skCircle(sketch, "E13.17.0", {"center": v(23.17, 25.56) * mm, "radius": 0.5 * mm});
            skCircle(sketch, "E13.18.0", {"center": v(21.89, 26.67) * mm, "radius": 0.5 * mm});
            skCircle(sketch, "E13.19.0", {"center": v(20.55, 27.71) * mm, "radius": 0.5 * mm});
            skCircle(sketch, "E13.20.0", {"center": v(19.17, 28.69) * mm, "radius": 0.5 * mm});
            skCircle(sketch, "E13.21.0", {"center": v(17.74, 29.6) * mm, "radius": 0.5 * mm});
            skCircle(sketch, "E13.22.0", {"center": v(16.26, 30.43) * mm, "radius": 0.5 * mm});
            skCircle(sketch, "E13.23.0", {"center": v(14.75, 31.19) * mm, "radius": 0.5 * mm});
            skCircle(sketch, "E13.24.0", {"center": v(13.2, 31.87) * mm, "radius": 0.5 * mm});
            skCircle(sketch, "E13.25.0", {"center": v(11.62, 32.48) * mm, "radius": 0.5 * mm});
            skCircle(sketch, "E13.26.0", {"center": v(10.01, 33.01) * mm, "radius": 0.5 * mm});
            skCircle(sketch, "E13.27.0", {"center": v(8.38, 33.47) * mm, "radius": 0.5 * mm});
            skCircle(sketch, "E13.28.0", {"center": v(6.73, 33.84) * mm, "radius": 0.5 * mm});
            skCircle(sketch, "E13.29.0", {"center": v(5.06, 34.13) * mm, "radius": 0.5 * mm});
            skCircle(sketch, "E13.30.0", {"center": v(3.38, 34.33) * mm, "radius": 0.5 * mm});
            skCircle(sketch, "E13.31.0", {"center": v(1.7, 34.46) * mm, "radius": 0.5 * mm});
            skCircle(sketch, "E13.32.0", {"center": v(0, 34.5) * mm, "radius": 0.5 * mm});
            skCircle(sketch, "E13.33.0", {"center": v(-1.7, 34.46) * mm, "radius": 0.5 * mm});
            skCircle(sketch, "E13.34.0", {"center": v(-3.38, 34.33) * mm, "radius": 0.5 * mm});
            skCircle(sketch, "E13.35.0", {"center": v(-5.06, 34.13) * mm, "radius": 0.5 * mm});
            skCircle(sketch, "E13.36.0", {"center": v(-6.73, 33.84) * mm, "radius": 0.5 * mm});
            skCircle(sketch, "E13.37.0", {"center": v(-8.38, 33.47) * mm, "radius": 0.5 * mm});
            skCircle(sketch, "E13.38.0", {"center": v(-10.01, 33.01) * mm, "radius": 0.5 * mm});
            skCircle(sketch, "E13.39.0", {"center": v(-11.62, 32.48) * mm, "radius": 0.5 * mm});
            skCircle(sketch, "E13.40.0", {"center": v(-13.2, 31.87) * mm, "radius": 0.5 * mm});
            skCircle(sketch, "E13.41.0", {"center": v(-14.75, 31.19) * mm, "radius": 0.5 * mm});
            skCircle(sketch, "E13.42.0", {"center": v(-16.26, 30.43) * mm, "radius": 0.5 * mm});
            skCircle(sketch, "E13.43.0", {"center": v(-17.74, 29.6) * mm, "radius": 0.5 * mm});
            skCircle(sketch, "E13.44.0", {"center": v(-19.17, 28.69) * mm, "radius": 0.5 * mm});
            skCircle(sketch, "E13.45.0", {"center": v(-20.55, 27.71) * mm, "radius": 0.5 * mm});
            skCircle(sketch, "E13.46.0", {"center": v(-21.89, 26.67) * mm, "radius": 0.5 * mm});
            skCircle(sketch, "E13.47.0", {"center": v(-23.17, 25.56) * mm, "radius": 0.5 * mm});
            skCircle(sketch, "E13.48.0", {"center": v(-24.4, 24.4) * mm, "radius": 0.5 * mm});
            skCircle(sketch, "E13.49.0", {"center": v(-25.56, 23.17) * mm, "radius": 0.5 * mm});
            skCircle(sketch, "E13.50.0", {"center": v(-26.67, 21.89) * mm, "radius": 0.5 * mm});
            skCircle(sketch, "E13.51.0", {"center": v(-27.71, 20.55) * mm, "radius": 0.5 * mm});
            skCircle(sketch, "E13.52.0", {"center": v(-28.69, 19.17) * mm, "radius": 0.5 * mm});
            skCircle(sketch, "E13.53.0", {"center": v(-29.6, 17.74) * mm, "radius": 0.5 * mm});
            skCircle(sketch, "E13.54.0", {"center": v(-30.43, 16.26) * mm, "radius": 0.5 * mm});
            skCircle(sketch, "E13.55.0", {"center": v(-31.19, 14.75) * mm, "radius": 0.5 * mm});
            skCircle(sketch, "E13.56.0", {"center": v(-31.87, 13.2) * mm, "radius": 0.5 * mm});
            skCircle(sketch, "E13.57.0", {"center": v(-32.48, 11.62) * mm, "radius": 0.5 * mm});
            skCircle(sketch, "E13.58.0", {"center": v(-33.01, 10.01) * mm, "radius": 0.5 * mm});
            skCircle(sketch, "E13.59.0", {"center": v(-33.47, 8.38) * mm, "radius": 0.5 * mm});
            skCircle(sketch, "E13.60.0", {"center": v(-33.84, 6.73) * mm, "radius": 0.5 * mm});
            skCircle(sketch, "E13.61.0", {"center": v(-34.13, 5.06) * mm, "radius": 0.5 * mm});
            skCircle(sketch, "E13.62.0", {"center": v(-34.33, 3.38) * mm, "radius": 0.5 * mm});
            skCircle(sketch, "E13.63.0", {"center": v(-34.46, 1.7) * mm, "radius": 0.5 * mm});
            skCircle(sketch, "E13.64.0", {"center": v(-34.5, 0) * mm, "radius": 0.5 * mm});
            skCircle(sketch, "E13.65.0", {"center": v(-34.46, -1.7) * mm, "radius": 0.5 * mm});
            skCircle(sketch, "E13.66.0", {"center": v(-34.33, -3.38) * mm, "radius": 0.5 * mm});
            skCircle(sketch, "E13.67.0", {"center": v(-34.13, -5.06) * mm, "radius": 0.5 * mm});
            skCircle(sketch, "E13.68.0", {"center": v(-33.84, -6.73) * mm, "radius": 0.5 * mm});
            skCircle(sketch, "E13.69.0", {"center": v(-33.47, -8.38) * mm, "radius": 0.5 * mm});
            skCircle(sketch, "E13.70.0", {"center": v(-33.01, -10.01) * mm, "radius": 0.5 * mm});
            skCircle(sketch, "E13.71.0", {"center": v(-32.48, -11.62) * mm, "radius": 0.5 * mm});
            skCircle(sketch, "E13.72.0", {"center": v(-31.87, -13.2) * mm, "radius": 0.5 * mm});
            skCircle(sketch, "E13.73.0", {"center": v(-31.19, -14.75) * mm, "radius": 0.5 * mm});
            skCircle(sketch, "E13.74.0", {"center": v(-30.43, -16.26) * mm, "radius": 0.5 * mm});
            skCircle(sketch, "E13.75.0", {"center": v(-29.6, -17.74) * mm, "radius": 0.5 * mm});
            skCircle(sketch, "E13.76.0", {"center": v(-28.69, -19.17) * mm, "radius": 0.5 * mm});
            skCircle(sketch, "E13.77.0", {"center": v(-27.71, -20.55) * mm, "radius": 0.5 * mm});
            skCircle(sketch, "E13.78.0", {"center": v(-26.67, -21.89) * mm, "radius": 0.5 * mm});
            skCircle(sketch, "E13.79.0", {"center": v(-25.56, -23.17) * mm, "radius": 0.5 * mm});
            skCircle(sketch, "E13.80.0", {"center": v(-24.4, -24.4) * mm, "radius": 0.5 * mm});
            skCircle(sketch, "E13.81.0", {"center": v(-23.17, -25.56) * mm, "radius": 0.5 * mm});
            skCircle(sketch, "E13.82.0", {"center": v(-21.89, -26.67) * mm, "radius": 0.5 * mm});
            skCircle(sketch, "E13.83.0", {"center": v(-20.55, -27.71) * mm, "radius": 0.5 * mm});
            skCircle(sketch, "E13.84.0", {"center": v(-19.17, -28.69) * mm, "radius": 0.5 * mm});
            skCircle(sketch, "E13.85.0", {"center": v(-17.74, -29.6) * mm, "radius": 0.5 * mm});
            skCircle(sketch, "E13.86.0", {"center": v(-16.26, -30.43) * mm, "radius": 0.5 * mm});
            skCircle(sketch, "E13.87.0", {"center": v(-14.75, -31.19) * mm, "radius": 0.5 * mm});
            skCircle(sketch, "E13.88.0", {"center": v(-13.2, -31.87) * mm, "radius": 0.5 * mm});
            skCircle(sketch, "E13.89.0", {"center": v(-11.62, -32.48) * mm, "radius": 0.5 * mm});
            skCircle(sketch, "E13.90.0", {"center": v(-10.01, -33.01) * mm, "radius": 0.5 * mm});
            skCircle(sketch, "E13.91.0", {"center": v(-8.38, -33.47) * mm, "radius": 0.5 * mm});
            skCircle(sketch, "E13.92.0", {"center": v(-6.73, -33.84) * mm, "radius": 0.5 * mm});
            skCircle(sketch, "E13.93.0", {"center": v(-5.06, -34.13) * mm, "radius": 0.5 * mm});
            skCircle(sketch, "E13.94.0", {"center": v(-3.38, -34.33) * mm, "radius": 0.5 * mm});
            skCircle(sketch, "E13.95.0", {"center": v(-1.7, -34.46) * mm, "radius": 0.5 * mm});
            skCircle(sketch, "E13.96.0", {"center": v(0, -34.5) * mm, "radius": 0.5 * mm});
            skCircle(sketch, "E13.97.0", {"center": v(1.7, -34.46) * mm, "radius": 0.5 * mm});
            skCircle(sketch, "E13.98.0", {"center": v(3.38, -34.33) * mm, "radius": 0.5 * mm});
            skCircle(sketch, "E13.99.0", {"center": v(5.06, -34.13) * mm, "radius": 0.5 * mm});
            skCircle(sketch, "E13.100.0", {"center": v(6.73, -33.84) * mm, "radius": 0.5 * mm});
            skCircle(sketch, "E13.101.0", {"center": v(8.38, -33.47) * mm, "radius": 0.5 * mm});
            skCircle(sketch, "E13.102.0", {"center": v(10.01, -33.01) * mm, "radius": 0.5 * mm});
            skCircle(sketch, "E13.103.0", {"center": v(11.62, -32.48) * mm, "radius": 0.5 * mm});
            skCircle(sketch, "E13.104.0", {"center": v(13.2, -31.87) * mm, "radius": 0.5 * mm});
            skCircle(sketch, "E13.105.0", {"center": v(14.75, -31.19) * mm, "radius": 0.5 * mm});
            skCircle(sketch, "E13.106.0", {"center": v(16.26, -30.43) * mm, "radius": 0.5 * mm});
            skCircle(sketch, "E13.107.0", {"center": v(17.74, -29.6) * mm, "radius": 0.5 * mm});
            skCircle(sketch, "E13.108.0", {"center": v(19.17, -28.69) * mm, "radius": 0.5 * mm});
            skCircle(sketch, "E13.109.0", {"center": v(20.55, -27.71) * mm, "radius": 0.5 * mm});
            skCircle(sketch, "E13.110.0", {"center": v(21.89, -26.67) * mm, "radius": 0.5 * mm});
            skCircle(sketch, "E13.111.0", {"center": v(23.17, -25.56) * mm, "radius": 0.5 * mm});
            skCircle(sketch, "E13.112.0", {"center": v(24.4, -24.4) * mm, "radius": 0.5 * mm});
            skCircle(sketch, "E13.113.0", {"center": v(25.56, -23.17) * mm, "radius": 0.5 * mm});
            skCircle(sketch, "E13.114.0", {"center": v(26.67, -21.89) * mm, "radius": 0.5 * mm});
            skCircle(sketch, "E13.115.0", {"center": v(27.71, -20.55) * mm, "radius": 0.5 * mm});
            skCircle(sketch, "E13.116.0", {"center": v(28.69, -19.17) * mm, "radius": 0.5 * mm});
            skCircle(sketch, "E13.117.0", {"center": v(29.6, -17.74) * mm, "radius": 0.5 * mm});
            skCircle(sketch, "E13.118.0", {"center": v(30.43, -16.26) * mm, "radius": 0.5 * mm});
            skCircle(sketch, "E13.119.0", {"center": v(31.19, -14.75) * mm, "radius": 0.5 * mm});
            skCircle(sketch, "E13.120.0", {"center": v(31.87, -13.2) * mm, "radius": 0.5 * mm});
            skCircle(sketch, "E13.121.0", {"center": v(32.48, -11.62) * mm, "radius": 0.5 * mm});
            skCircle(sketch, "E13.122.0", {"center": v(33.01, -10.01) * mm, "radius": 0.5 * mm});
            skCircle(sketch, "E13.123.0", {"center": v(33.47, -8.38) * mm, "radius": 0.5 * mm});
            skCircle(sketch, "E13.124.0", {"center": v(33.84, -6.73) * mm, "radius": 0.5 * mm});
            skCircle(sketch, "E13.125.0", {"center": v(34.13, -5.06) * mm, "radius": 0.5 * mm});
            skCircle(sketch, "E13.126.0", {"center": v(34.33, -3.38) * mm, "radius": 0.5 * mm});
            skCircle(sketch, "E13.127.0", {"center": v(34.46, -1.7) * mm, "radius": 0.5 * mm});
            skCircle(sketch, "E14.1.0", {"center": v(32.95, 1.74) * mm, "radius": 0.5 * mm});
            skCircle(sketch, "E14.2.0", {"center": v(32.82, 3.48) * mm, "radius": 0.5 * mm});
            skCircle(sketch, "E14.3.0", {"center": v(32.59, 5.2) * mm, "radius": 0.5 * mm});
            skCircle(sketch, "E14.4.0", {"center": v(32.27, 6.92) * mm, "radius": 0.5 * mm});
            skCircle(sketch, "E14.5.0", {"center": v(31.86, 8.61) * mm, "radius": 0.5 * mm});
            skCircle(sketch, "E14.6.0", {"center": v(31.36, 10.28) * mm, "radius": 0.5 * mm});
            skCircle(sketch, "E14.7.0", {"center": v(30.77, 11.92) * mm, "radius": 0.5 * mm});
            skCircle(sketch, "E14.8.0", {"center": v(30.1, 13.53) * mm, "radius": 0.5 * mm});
            skCircle(sketch, "E14.9.0", {"center": v(29.34, 15.1) * mm, "radius": 0.5 * mm});
            skCircle(sketch, "E14.10.0", {"center": v(28.5, 16.63) * mm, "radius": 0.5 * mm});
            skCircle(sketch, "E14.11.0", {"center": v(27.59, 18.1) * mm, "radius": 0.5 * mm});
            skCircle(sketch, "E14.12.0", {"center": v(26.6, 19.54) * mm, "radius": 0.5 * mm});
            skCircle(sketch, "E14.13.0", {"center": v(25.53, 20.91) * mm, "radius": 0.5 * mm});
            skCircle(sketch, "E14.14.0", {"center": v(24.39, 22.23) * mm, "radius": 0.5 * mm});
            skCircle(sketch, "E14.15.0", {"center": v(23.18, 23.49) * mm, "radius": 0.5 * mm});
            skCircle(sketch, "E14.16.0", {"center": v(21.9, 24.68) * mm, "radius": 0.5 * mm});
            skCircle(sketch, "E14.17.0", {"center": v(20.58, 25.8) * mm, "radius": 0.5 * mm});
            skCircle(sketch, "E14.18.0", {"center": v(19.18, 26.85) * mm, "radius": 0.5 * mm});
            skCircle(sketch, "E14.19.0", {"center": v(17.74, 27.83) * mm, "radius": 0.5 * mm});
            skCircle(sketch, "E14.20.0", {"center": v(16.25, 28.72) * mm, "radius": 0.5 * mm});
            skCircle(sketch, "E14.21.0", {"center": v(14.7, 29.54) * mm, "radius": 0.5 * mm});
            skCircle(sketch, "E14.22.0", {"center": v(13.13, 30.28) * mm, "radius": 0.5 * mm});
            skCircle(sketch, "E14.23.0", {"center": v(11.51, 30.93) * mm, "radius": 0.5 * mm});
            skCircle(sketch, "E14.24.0", {"center": v(9.87, 31.5) * mm, "radius": 0.5 * mm});
            skCircle(sketch, "E14.25.0", {"center": v(8.19, 31.97) * mm, "radius": 0.5 * mm});
            skCircle(sketch, "E14.26.0", {"center": v(6.5, 32.36) * mm, "radius": 0.5 * mm});
            skCircle(sketch, "E14.27.0", {"center": v(4.77, 32.65) * mm, "radius": 0.5 * mm});
            skCircle(sketch, "E14.28.0", {"center": v(3.04, 32.86) * mm, "radius": 0.5 * mm});
            skCircle(sketch, "E14.29.0", {"center": v(1.3, 32.97) * mm, "radius": 0.5 * mm});
            skCircle(sketch, "E14.30.0", {"center": v(-0.44, 33) * mm, "radius": 0.5 * mm});
            skCircle(sketch, "E14.31.0", {"center": v(-2.18, 32.93) * mm, "radius": 0.5 * mm});
            skCircle(sketch, "E14.32.0", {"center": v(-3.91, 32.77) * mm, "radius": 0.5 * mm});
            skCircle(sketch, "E14.33.0", {"center": v(-5.64, 32.52) * mm, "radius": 0.5 * mm});
            skCircle(sketch, "E14.34.0", {"center": v(-7.34, 32.17) * mm, "radius": 0.5 * mm});
            skCircle(sketch, "E14.35.0", {"center": v(-9.03, 31.74) * mm, "radius": 0.5 * mm});
            skCircle(sketch, "E14.36.0", {"center": v(-10.7, 31.22) * mm, "radius": 0.5 * mm});
            skCircle(sketch, "E14.37.0", {"center": v(-12.33, 30.61) * mm, "radius": 0.5 * mm});
            skCircle(sketch, "E14.38.0", {"center": v(-13.92, 29.92) * mm, "radius": 0.5 * mm});
            skCircle(sketch, "E14.39.0", {"center": v(-15.48, 29.14) * mm, "radius": 0.5 * mm});
            skCircle(sketch, "E14.40.0", {"center": v(-17, 28.28) * mm, "radius": 0.5 * mm});
            skCircle(sketch, "E14.41.0", {"center": v(-18.47, 27.35) * mm, "radius": 0.5 * mm});
            skCircle(sketch, "E14.42.0", {"center": v(-19.89, 26.33) * mm, "radius": 0.5 * mm});
            skCircle(sketch, "E14.43.0", {"center": v(-21.25, 25.25) * mm, "radius": 0.5 * mm});
            skCircle(sketch, "E14.44.0", {"center": v(-22.55, 24.1) * mm, "radius": 0.5 * mm});
            skCircle(sketch, "E14.45.0", {"center": v(-23.8, 22.87) * mm, "radius": 0.5 * mm});
            skCircle(sketch, "E14.46.0", {"center": v(-24.97, 21.58) * mm, "radius": 0.5 * mm});
            skCircle(sketch, "E14.47.0", {"center": v(-26.07, 20.23) * mm, "radius": 0.5 * mm});
            skCircle(sketch, "E14.48.0", {"center": v(-27.1, 18.83) * mm, "radius": 0.5 * mm});
            skCircle(sketch, "E14.49.0", {"center": v(-28.06, 17.37) * mm, "radius": 0.5 * mm});
            skCircle(sketch, "E14.50.0", {"center": v(-28.93, 15.87) * mm, "radius": 0.5 * mm});
            skCircle(sketch, "E14.51.0", {"center": v(-29.73, 14.32) * mm, "radius": 0.5 * mm});
            skCircle(sketch, "E14.52.0", {"center": v(-30.45, 12.73) * mm, "radius": 0.5 * mm});
            skCircle(sketch, "E14.53.0", {"center": v(-31.08, 11.1) * mm, "radius": 0.5 * mm});
            skCircle(sketch, "E14.54.0", {"center": v(-31.62, 9.45) * mm, "radius": 0.5 * mm});
            skCircle(sketch, "E14.55.0", {"center": v(-32.07, 7.77) * mm, "radius": 0.5 * mm});
            skCircle(sketch, "E14.56.0", {"center": v(-32.44, 6.06) * mm, "radius": 0.5 * mm});
            skCircle(sketch, "E14.57.0", {"center": v(-32.71, 4.34) * mm, "radius": 0.5 * mm});
            skCircle(sketch, "E14.58.0", {"center": v(-32.9, 2.61) * mm, "radius": 0.5 * mm});
            skCircle(sketch, "E14.59.0", {"center": v(-32.99, 0.87) * mm, "radius": 0.5 * mm});
            skCircle(sketch, "E14.60.0", {"center": v(-32.99, -0.87) * mm, "radius": 0.5 * mm});
            skCircle(sketch, "E14.61.0", {"center": v(-32.9, -2.61) * mm, "radius": 0.5 * mm});
            skCircle(sketch, "E14.62.0", {"center": v(-32.71, -4.34) * mm, "radius": 0.5 * mm});
            skCircle(sketch, "E14.63.0", {"center": v(-32.44, -6.06) * mm, "radius": 0.5 * mm});
            skCircle(sketch, "E14.64.0", {"center": v(-32.07, -7.77) * mm, "radius": 0.5 * mm});
            skCircle(sketch, "E14.65.0", {"center": v(-31.62, -9.45) * mm, "radius": 0.5 * mm});
            skCircle(sketch, "E14.66.0", {"center": v(-31.08, -11.1) * mm, "radius": 0.5 * mm});
            skCircle(sketch, "E14.67.0", {"center": v(-30.45, -12.73) * mm, "radius": 0.5 * mm});
            skCircle(sketch, "E14.68.0", {"center": v(-29.73, -14.32) * mm, "radius": 0.5 * mm});
            skCircle(sketch, "E14.69.0", {"center": v(-28.93, -15.87) * mm, "radius": 0.5 * mm});
            skCircle(sketch, "E14.70.0", {"center": v(-28.06, -17.37) * mm, "radius": 0.5 * mm});
            skCircle(sketch, "E14.71.0", {"center": v(-27.1, -18.83) * mm, "radius": 0.5 * mm});
            skCircle(sketch, "E14.72.0", {"center": v(-26.07, -20.23) * mm, "radius": 0.5 * mm});
            skCircle(sketch, "E14.73.0", {"center": v(-24.97, -21.58) * mm, "radius": 0.5 * mm});
            skCircle(sketch, "E14.74.0", {"center": v(-23.8, -22.87) * mm, "radius": 0.5 * mm});
            skCircle(sketch, "E14.75.0", {"center": v(-22.55, -24.1) * mm, "radius": 0.5 * mm});
            skCircle(sketch, "E14.76.0", {"center": v(-21.25, -25.25) * mm, "radius": 0.5 * mm});
            skCircle(sketch, "E14.77.0", {"center": v(-19.89, -26.33) * mm, "radius": 0.5 * mm});
            skCircle(sketch, "E14.78.0", {"center": v(-18.47, -27.35) * mm, "radius": 0.5 * mm});
            skCircle(sketch, "E14.79.0", {"center": v(-17, -28.28) * mm, "radius": 0.5 * mm});
            skCircle(sketch, "E14.80.0", {"center": v(-15.48, -29.14) * mm, "radius": 0.5 * mm});
            skCircle(sketch, "E14.81.0", {"center": v(-13.92, -29.92) * mm, "radius": 0.5 * mm});
            skCircle(sketch, "E14.82.0", {"center": v(-12.33, -30.61) * mm, "radius": 0.5 * mm});
            skCircle(sketch, "E14.83.0", {"center": v(-10.7, -31.22) * mm, "radius": 0.5 * mm});
            skCircle(sketch, "E14.84.0", {"center": v(-9.03, -31.74) * mm, "radius": 0.5 * mm});
            skCircle(sketch, "E14.85.0", {"center": v(-7.34, -32.17) * mm, "radius": 0.5 * mm});
            skCircle(sketch, "E14.86.0", {"center": v(-5.64, -32.52) * mm, "radius": 0.5 * mm});
            skCircle(sketch, "E14.87.0", {"center": v(-3.91, -32.77) * mm, "radius": 0.5 * mm});
            skCircle(sketch, "E14.88.0", {"center": v(-2.18, -32.93) * mm, "radius": 0.5 * mm});
            skCircle(sketch, "E14.89.0", {"center": v(-0.44, -33) * mm, "radius": 0.5 * mm});
            skCircle(sketch, "E14.90.0", {"center": v(1.3, -32.97) * mm, "radius": 0.5 * mm});
            skCircle(sketch, "E14.91.0", {"center": v(3.04, -32.86) * mm, "radius": 0.5 * mm});
            skCircle(sketch, "E14.92.0", {"center": v(4.77, -32.65) * mm, "radius": 0.5 * mm});
            skCircle(sketch, "E14.93.0", {"center": v(6.5, -32.36) * mm, "radius": 0.5 * mm});
            skCircle(sketch, "E14.94.0", {"center": v(8.19, -31.97) * mm, "radius": 0.5 * mm});
            skCircle(sketch, "E14.95.0", {"center": v(9.87, -31.5) * mm, "radius": 0.5 * mm});
            skCircle(sketch, "E14.96.0", {"center": v(11.51, -30.93) * mm, "radius": 0.5 * mm});
            skCircle(sketch, "E14.97.0", {"center": v(13.13, -30.28) * mm, "radius": 0.5 * mm});
            skCircle(sketch, "E14.98.0", {"center": v(14.7, -29.54) * mm, "radius": 0.5 * mm});
            skCircle(sketch, "E14.99.0", {"center": v(16.25, -28.72) * mm, "radius": 0.5 * mm});
            skCircle(sketch, "E14.100.0", {"center": v(17.74, -27.83) * mm, "radius": 0.5 * mm});
            skCircle(sketch, "E14.101.0", {"center": v(19.18, -26.85) * mm, "radius": 0.5 * mm});
            skCircle(sketch, "E14.102.0", {"center": v(20.58, -25.8) * mm, "radius": 0.5 * mm});
            skCircle(sketch, "E14.103.0", {"center": v(21.9, -24.68) * mm, "radius": 0.5 * mm});
            skCircle(sketch, "E14.104.0", {"center": v(23.18, -23.49) * mm, "radius": 0.5 * mm});
            skCircle(sketch, "E14.105.0", {"center": v(24.39, -22.23) * mm, "radius": 0.5 * mm});
            skCircle(sketch, "E14.106.0", {"center": v(25.53, -20.91) * mm, "radius": 0.5 * mm});
            skCircle(sketch, "E14.107.0", {"center": v(26.6, -19.54) * mm, "radius": 0.5 * mm});
            skCircle(sketch, "E14.108.0", {"center": v(27.59, -18.1) * mm, "radius": 0.5 * mm});
            skCircle(sketch, "E14.109.0", {"center": v(28.5, -16.63) * mm, "radius": 0.5 * mm});
            skCircle(sketch, "E14.110.0", {"center": v(29.34, -15.1) * mm, "radius": 0.5 * mm});
            skCircle(sketch, "E14.111.0", {"center": v(30.1, -13.53) * mm, "radius": 0.5 * mm});
            skCircle(sketch, "E14.112.0", {"center": v(30.77, -11.92) * mm, "radius": 0.5 * mm});
            skCircle(sketch, "E14.113.0", {"center": v(31.36, -10.28) * mm, "radius": 0.5 * mm});
            skCircle(sketch, "E14.114.0", {"center": v(31.86, -8.61) * mm, "radius": 0.5 * mm});
            skCircle(sketch, "E14.115.0", {"center": v(32.27, -6.92) * mm, "radius": 0.5 * mm});
            skCircle(sketch, "E14.116.0", {"center": v(32.59, -5.2) * mm, "radius": 0.5 * mm});
            skCircle(sketch, "E14.117.0", {"center": v(32.82, -3.48) * mm, "radius": 0.5 * mm});
            skCircle(sketch, "E14.118.0", {"center": v(32.95, -1.74) * mm, "radius": 0.5 * mm});
            skCircle(sketch, "E15.1.0", {"center": v(31.45, 1.8) * mm, "radius": 0.5 * mm});
            skCircle(sketch, "E15.2.0", {"center": v(31.3, 3.6) * mm, "radius": 0.5 * mm});
            skCircle(sketch, "E15.3.0", {"center": v(31.04, 5.37) * mm, "radius": 0.5 * mm});
            skCircle(sketch, "E15.4.0", {"center": v(30.68, 7.13) * mm, "radius": 0.5 * mm});
            skCircle(sketch, "E15.5.0", {"center": v(30.22, 8.87) * mm, "radius": 0.5 * mm});
            skCircle(sketch, "E15.6.0", {"center": v(29.67, 10.59) * mm, "radius": 0.5 * mm});
            skCircle(sketch, "E15.7.0", {"center": v(29.02, 12.26) * mm, "radius": 0.5 * mm});
            skCircle(sketch, "E15.8.0", {"center": v(28.27, 13.9) * mm, "radius": 0.5 * mm});
            skCircle(sketch, "E15.9.0", {"center": v(27.43, 15.49) * mm, "radius": 0.5 * mm});
            skCircle(sketch, "E15.10.0", {"center": v(26.5, 17.03) * mm, "radius": 0.5 * mm});
            skCircle(sketch, "E15.11.0", {"center": v(25.48, 18.52) * mm, "radius": 0.5 * mm});
            skCircle(sketch, "E15.12.0", {"center": v(24.39, 19.94) * mm, "radius": 0.5 * mm});
            skCircle(sketch, "E15.13.0", {"center": v(23.2, 21.3) * mm, "radius": 0.5 * mm});
            skCircle(sketch, "E15.14.0", {"center": v(21.95, 22.59) * mm, "radius": 0.5 * mm});
            skCircle(sketch, "E15.15.0", {"center": v(20.63, 23.8) * mm, "radius": 0.5 * mm});
            skCircle(sketch, "E15.16.0", {"center": v(19.24, 24.94) * mm, "radius": 0.5 * mm});
            skCircle(sketch, "E15.17.0", {"center": v(17.78, 26) * mm, "radius": 0.5 * mm});
            skCircle(sketch, "E15.18.0", {"center": v(16.27, 26.97) * mm, "radius": 0.5 * mm});
            skCircle(sketch, "E15.19.0", {"center": v(14.7, 27.86) * mm, "radius": 0.5 * mm});
            skCircle(sketch, "E15.20.0", {"center": v(13.09, 28.65) * mm, "radius": 0.5 * mm});
            skCircle(sketch, "E15.21.0", {"center": v(11.43, 29.35) * mm, "radius": 0.5 * mm});
            skCircle(sketch, "E15.22.0", {"center": v(9.73, 29.96) * mm, "radius": 0.5 * mm});
            skCircle(sketch, "E15.23.0", {"center": v(8, 30.47) * mm, "radius": 0.5 * mm});
            skCircle(sketch, "E15.24.0", {"center": v(6.26, 30.87) * mm, "radius": 0.5 * mm});
            skCircle(sketch, "E15.25.0", {"center": v(4.48, 31.18) * mm, "radius": 0.5 * mm});
            skCircle(sketch, "E15.26.0", {"center": v(2.7, 31.38) * mm, "radius": 0.5 * mm});
            skCircle(sketch, "E15.27.0", {"center": v(0.9, 31.49) * mm, "radius": 0.5 * mm});
            skCircle(sketch, "E15.28.0", {"center": v(-0.9, 31.49) * mm, "radius": 0.5 * mm});
            skCircle(sketch, "E15.29.0", {"center": v(-2.7, 31.38) * mm, "radius": 0.5 * mm});
            skCircle(sketch, "E15.30.0", {"center": v(-4.48, 31.18) * mm, "radius": 0.5 * mm});
            skCircle(sketch, "E15.31.0", {"center": v(-6.26, 30.87) * mm, "radius": 0.5 * mm});
            skCircle(sketch, "E15.32.0", {"center": v(-8, 30.47) * mm, "radius": 0.5 * mm});
            skCircle(sketch, "E15.33.0", {"center": v(-9.73, 29.96) * mm, "radius": 0.5 * mm});
            skCircle(sketch, "E15.34.0", {"center": v(-11.43, 29.35) * mm, "radius": 0.5 * mm});
            skCircle(sketch, "E15.35.0", {"center": v(-13.09, 28.65) * mm, "radius": 0.5 * mm});
            skCircle(sketch, "E15.36.0", {"center": v(-14.7, 27.86) * mm, "radius": 0.5 * mm});
            skCircle(sketch, "E15.37.0", {"center": v(-16.27, 26.97) * mm, "radius": 0.5 * mm});
            skCircle(sketch, "E15.38.0", {"center": v(-17.78, 26) * mm, "radius": 0.5 * mm});
            skCircle(sketch, "E15.39.0", {"center": v(-19.24, 24.94) * mm, "radius": 0.5 * mm});
            skCircle(sketch, "E15.40.0", {"center": v(-20.63, 23.8) * mm, "radius": 0.5 * mm});
            skCircle(sketch, "E15.41.0", {"center": v(-21.95, 22.59) * mm, "radius": 0.5 * mm});
            skCircle(sketch, "E15.42.0", {"center": v(-23.2, 21.3) * mm, "radius": 0.5 * mm});
            skCircle(sketch, "E15.43.0", {"center": v(-24.39, 19.94) * mm, "radius": 0.5 * mm});
            skCircle(sketch, "E15.44.0", {"center": v(-25.48, 18.52) * mm, "radius": 0.5 * mm});
            skCircle(sketch, "E15.45.0", {"center": v(-26.5, 17.03) * mm, "radius": 0.5 * mm});
            skCircle(sketch, "E15.46.0", {"center": v(-27.43, 15.49) * mm, "radius": 0.5 * mm});
            skCircle(sketch, "E15.47.0", {"center": v(-28.27, 13.9) * mm, "radius": 0.5 * mm});
            skCircle(sketch, "E15.48.0", {"center": v(-29.02, 12.26) * mm, "radius": 0.5 * mm});
            skCircle(sketch, "E15.49.0", {"center": v(-29.67, 10.59) * mm, "radius": 0.5 * mm});
            skCircle(sketch, "E15.50.0", {"center": v(-30.22, 8.87) * mm, "radius": 0.5 * mm});
            skCircle(sketch, "E15.51.0", {"center": v(-30.68, 7.13) * mm, "radius": 0.5 * mm});
            skCircle(sketch, "E15.52.0", {"center": v(-31.04, 5.37) * mm, "radius": 0.5 * mm});
            skCircle(sketch, "E15.53.0", {"center": v(-31.3, 3.6) * mm, "radius": 0.5 * mm});
            skCircle(sketch, "E15.54.0", {"center": v(-31.45, 1.8) * mm, "radius": 0.5 * mm});
            skCircle(sketch, "E15.55.0", {"center": v(-31.5, 0) * mm, "radius": 0.5 * mm});
            skCircle(sketch, "E15.56.0", {"center": v(-31.45, -1.8) * mm, "radius": 0.5 * mm});
            skCircle(sketch, "E15.57.0", {"center": v(-31.3, -3.6) * mm, "radius": 0.5 * mm});
            skCircle(sketch, "E15.58.0", {"center": v(-31.04, -5.37) * mm, "radius": 0.5 * mm});
            skCircle(sketch, "E15.59.0", {"center": v(-30.68, -7.13) * mm, "radius": 0.5 * mm});
            skCircle(sketch, "E15.60.0", {"center": v(-30.22, -8.87) * mm, "radius": 0.5 * mm});
            skCircle(sketch, "E15.61.0", {"center": v(-29.67, -10.59) * mm, "radius": 0.5 * mm});
            skCircle(sketch, "E15.62.0", {"center": v(-29.02, -12.26) * mm, "radius": 0.5 * mm});
            skCircle(sketch, "E15.63.0", {"center": v(-28.27, -13.9) * mm, "radius": 0.5 * mm});
            skCircle(sketch, "E15.64.0", {"center": v(-27.43, -15.49) * mm, "radius": 0.5 * mm});
            skCircle(sketch, "E15.65.0", {"center": v(-26.5, -17.03) * mm, "radius": 0.5 * mm});
            skCircle(sketch, "E15.66.0", {"center": v(-25.48, -18.52) * mm, "radius": 0.5 * mm});
            skCircle(sketch, "E15.67.0", {"center": v(-24.39, -19.94) * mm, "radius": 0.5 * mm});
            skCircle(sketch, "E15.68.0", {"center": v(-23.2, -21.3) * mm, "radius": 0.5 * mm});
            skCircle(sketch, "E15.69.0", {"center": v(-21.95, -22.59) * mm, "radius": 0.5 * mm});
            skCircle(sketch, "E15.70.0", {"center": v(-20.63, -23.8) * mm, "radius": 0.5 * mm});
            skCircle(sketch, "E15.71.0", {"center": v(-19.24, -24.94) * mm, "radius": 0.5 * mm});
            skCircle(sketch, "E15.72.0", {"center": v(-17.78, -26) * mm, "radius": 0.5 * mm});
            skCircle(sketch, "E15.73.0", {"center": v(-16.27, -26.97) * mm, "radius": 0.5 * mm});
            skCircle(sketch, "E15.74.0", {"center": v(-14.7, -27.86) * mm, "radius": 0.5 * mm});
            skCircle(sketch, "E15.75.0", {"center": v(-13.09, -28.65) * mm, "radius": 0.5 * mm});
            skCircle(sketch, "E15.76.0", {"center": v(-11.43, -29.35) * mm, "radius": 0.5 * mm});
            skCircle(sketch, "E15.77.0", {"center": v(-9.73, -29.96) * mm, "radius": 0.5 * mm});
            skCircle(sketch, "E15.78.0", {"center": v(-8, -30.47) * mm, "radius": 0.5 * mm});
            skCircle(sketch, "E15.79.0", {"center": v(-6.26, -30.87) * mm, "radius": 0.5 * mm});
            skCircle(sketch, "E15.80.0", {"center": v(-4.48, -31.18) * mm, "radius": 0.5 * mm});
            skCircle(sketch, "E15.81.0", {"center": v(-2.7, -31.38) * mm, "radius": 0.5 * mm});
            skCircle(sketch, "E15.82.0", {"center": v(-0.9, -31.49) * mm, "radius": 0.5 * mm});
            skCircle(sketch, "E15.83.0", {"center": v(0.9, -31.49) * mm, "radius": 0.5 * mm});
            skCircle(sketch, "E15.84.0", {"center": v(2.7, -31.38) * mm, "radius": 0.5 * mm});
            skCircle(sketch, "E15.85.0", {"center": v(4.48, -31.18) * mm, "radius": 0.5 * mm});
            skCircle(sketch, "E15.86.0", {"center": v(6.26, -30.87) * mm, "radius": 0.5 * mm});
            skCircle(sketch, "E15.87.0", {"center": v(8, -30.47) * mm, "radius": 0.5 * mm});
            skCircle(sketch, "E15.88.0", {"center": v(9.73, -29.96) * mm, "radius": 0.5 * mm});
            skCircle(sketch, "E15.89.0", {"center": v(11.43, -29.35) * mm, "radius": 0.5 * mm});
            skCircle(sketch, "E15.90.0", {"center": v(13.09, -28.65) * mm, "radius": 0.5 * mm});
            skCircle(sketch, "E15.91.0", {"center": v(14.7, -27.86) * mm, "radius": 0.5 * mm});
            skCircle(sketch, "E15.92.0", {"center": v(16.27, -26.97) * mm, "radius": 0.5 * mm});
            skCircle(sketch, "E15.93.0", {"center": v(17.78, -26) * mm, "radius": 0.5 * mm});
            skCircle(sketch, "E15.94.0", {"center": v(19.24, -24.94) * mm, "radius": 0.5 * mm});
            skCircle(sketch, "E15.95.0", {"center": v(20.63, -23.8) * mm, "radius": 0.5 * mm});
            skCircle(sketch, "E15.96.0", {"center": v(21.95, -22.59) * mm, "radius": 0.5 * mm});
            skCircle(sketch, "E15.97.0", {"center": v(23.2, -21.3) * mm, "radius": 0.5 * mm});
            skCircle(sketch, "E15.98.0", {"center": v(24.39, -19.94) * mm, "radius": 0.5 * mm});
            skCircle(sketch, "E15.99.0", {"center": v(25.48, -18.52) * mm, "radius": 0.5 * mm});
            skCircle(sketch, "E15.100.0", {"center": v(26.5, -17.03) * mm, "radius": 0.5 * mm});
            skCircle(sketch, "E15.101.0", {"center": v(27.43, -15.49) * mm, "radius": 0.5 * mm});
            skCircle(sketch, "E15.102.0", {"center": v(28.27, -13.9) * mm, "radius": 0.5 * mm});
            skCircle(sketch, "E15.103.0", {"center": v(29.02, -12.26) * mm, "radius": 0.5 * mm});
            skCircle(sketch, "E15.104.0", {"center": v(29.67, -10.59) * mm, "radius": 0.5 * mm});
            skCircle(sketch, "E15.105.0", {"center": v(30.22, -8.87) * mm, "radius": 0.5 * mm});
            skCircle(sketch, "E15.106.0", {"center": v(30.68, -7.13) * mm, "radius": 0.5 * mm});
            skCircle(sketch, "E15.107.0", {"center": v(31.04, -5.37) * mm, "radius": 0.5 * mm});
            skCircle(sketch, "E15.108.0", {"center": v(31.3, -3.6) * mm, "radius": 0.5 * mm});
            skCircle(sketch, "E15.109.0", {"center": v(31.45, -1.8) * mm, "radius": 0.5 * mm});
            skCircle(sketch, "E16.1.0", {"center": v(29.94, 1.87) * mm, "radius": 0.5 * mm});
            skCircle(sketch, "E16.2.0", {"center": v(29.77, 3.72) * mm, "radius": 0.5 * mm});
            skCircle(sketch, "E16.3.0", {"center": v(29.48, 5.57) * mm, "radius": 0.5 * mm});
            skCircle(sketch, "E16.4.0", {"center": v(29.08, 7.39) * mm, "radius": 0.5 * mm});
            skCircle(sketch, "E16.5.0", {"center": v(28.56, 9.18) * mm, "radius": 0.5 * mm});
            skCircle(sketch, "E16.6.0", {"center": v(27.93, 10.94) * mm, "radius": 0.5 * mm});
            skCircle(sketch, "E16.7.0", {"center": v(27.2, 12.66) * mm, "radius": 0.5 * mm});
            skCircle(sketch, "E16.8.0", {"center": v(26.36, 14.32) * mm, "radius": 0.5 * mm});
            skCircle(sketch, "E16.9.0", {"center": v(25.42, 15.93) * mm, "radius": 0.5 * mm});
            skCircle(sketch, "E16.10.0", {"center": v(24.38, 17.48) * mm, "radius": 0.5 * mm});
            skCircle(sketch, "E16.11.0", {"center": v(23.25, 18.96) * mm, "radius": 0.5 * mm});
            skCircle(sketch, "E16.12.0", {"center": v(22.02, 20.37) * mm, "radius": 0.5 * mm});
            skCircle(sketch, "E16.13.0", {"center": v(20.71, 21.7) * mm, "radius": 0.5 * mm});
            skCircle(sketch, "E16.14.0", {"center": v(19.32, 22.95) * mm, "radius": 0.5 * mm});
            skCircle(sketch, "E16.15.0", {"center": v(17.86, 24.1) * mm, "radius": 0.5 * mm});
            skCircle(sketch, "E16.16.0", {"center": v(16.33, 25.17) * mm, "radius": 0.5 * mm});
            skCircle(sketch, "E16.17.0", {"center": v(14.73, 26.13) * mm, "radius": 0.5 * mm});
            skCircle(sketch, "E16.18.0", {"center": v(13.08, 27) * mm, "radius": 0.5 * mm});
            skCircle(sketch, "E16.19.0", {"center": v(11.37, 27.76) * mm, "radius": 0.5 * mm});
            skCircle(sketch, "E16.20.0", {"center": v(9.62, 28.41) * mm, "radius": 0.5 * mm});
            skCircle(sketch, "E16.21.0", {"center": v(7.84, 28.96) * mm, "radius": 0.5 * mm});
            skCircle(sketch, "E16.22.0", {"center": v(6.02, 29.39) * mm, "radius": 0.5 * mm});
            skCircle(sketch, "E16.23.0", {"center": v(4.19, 29.7) * mm, "radius": 0.5 * mm});
            skCircle(sketch, "E16.24.0", {"center": v(2.33, 29.9) * mm, "radius": 0.5 * mm});
            skCircle(sketch, "E16.25.0", {"center": v(0.47, 30) * mm, "radius": 0.5 * mm});
            skCircle(sketch, "E16.26.0", {"center": v(-1.4, 29.97) * mm, "radius": 0.5 * mm});
            skCircle(sketch, "E16.27.0", {"center": v(-3.26, 29.82) * mm, "radius": 0.5 * mm});
            skCircle(sketch, "E16.28.0", {"center": v(-5.1, 29.56) * mm, "radius": 0.5 * mm});
            skCircle(sketch, "E16.29.0", {"center": v(-6.94, 29.19) * mm, "radius": 0.5 * mm});
            skCircle(sketch, "E16.30.0", {"center": v(-8.74, 28.7) * mm, "radius": 0.5 * mm});
            skCircle(sketch, "E16.31.0", {"center": v(-10.5, 28.1) * mm, "radius": 0.5 * mm});
            skCircle(sketch, "E16.32.0", {"center": v(-12.23, 27.4) * mm, "radius": 0.5 * mm});
            skCircle(sketch, "E16.33.0", {"center": v(-13.9, 26.58) * mm, "radius": 0.5 * mm});
            skCircle(sketch, "E16.34.0", {"center": v(-15.54, 25.66) * mm, "radius": 0.5 * mm});
            skCircle(sketch, "E16.35.0", {"center": v(-17.1, 24.65) * mm, "radius": 0.5 * mm});
            skCircle(sketch, "E16.36.0", {"center": v(-18.6, 23.54) * mm, "radius": 0.5 * mm});
            skCircle(sketch, "E16.37.0", {"center": v(-20.03, 22.34) * mm, "radius": 0.5 * mm});
            skCircle(sketch, "E16.38.0", {"center": v(-21.38, 21.05) * mm, "radius": 0.5 * mm});
            skCircle(sketch, "E16.39.0", {"center": v(-22.64, 19.68) * mm, "radius": 0.5 * mm});
            skCircle(sketch, "E16.40.0", {"center": v(-23.82, 18.23) * mm, "radius": 0.5 * mm});
            skCircle(sketch, "E16.41.0", {"center": v(-24.91, 16.72) * mm, "radius": 0.5 * mm});
            skCircle(sketch, "E16.42.0", {"center": v(-25.9, 15.13) * mm, "radius": 0.5 * mm});
            skCircle(sketch, "E16.43.0", {"center": v(-26.8, 13.5) * mm, "radius": 0.5 * mm});
            skCircle(sketch, "E16.44.0", {"center": v(-27.58, 11.8) * mm, "radius": 0.5 * mm});
            skCircle(sketch, "E16.45.0", {"center": v(-28.26, 10.07) * mm, "radius": 0.5 * mm});
            skCircle(sketch, "E16.46.0", {"center": v(-28.83, 8.29) * mm, "radius": 0.5 * mm});
            skCircle(sketch, "E16.47.0", {"center": v(-29.3, 6.48) * mm, "radius": 0.5 * mm});
            skCircle(sketch, "E16.48.0", {"center": v(-29.64, 4.65) * mm, "radius": 0.5 * mm});
            skCircle(sketch, "E16.49.0", {"center": v(-29.87, 2.8) * mm, "radius": 0.5 * mm});
            skCircle(sketch, "E16.50.0", {"center": v(-29.99, 0.93) * mm, "radius": 0.5 * mm});
            skCircle(sketch, "E16.51.0", {"center": v(-29.99, -0.93) * mm, "radius": 0.5 * mm});
            skCircle(sketch, "E16.52.0", {"center": v(-29.87, -2.8) * mm, "radius": 0.5 * mm});
            skCircle(sketch, "E16.53.0", {"center": v(-29.64, -4.65) * mm, "radius": 0.5 * mm});
            skCircle(sketch, "E16.54.0", {"center": v(-29.3, -6.48) * mm, "radius": 0.5 * mm});
            skCircle(sketch, "E16.55.0", {"center": v(-28.83, -8.29) * mm, "radius": 0.5 * mm});
            skCircle(sketch, "E16.56.0", {"center": v(-28.26, -10.07) * mm, "radius": 0.5 * mm});
            skCircle(sketch, "E16.57.0", {"center": v(-27.58, -11.8) * mm, "radius": 0.5 * mm});
            skCircle(sketch, "E16.58.0", {"center": v(-26.8, -13.5) * mm, "radius": 0.5 * mm});
            skCircle(sketch, "E16.59.0", {"center": v(-25.9, -15.13) * mm, "radius": 0.5 * mm});
            skCircle(sketch, "E16.60.0", {"center": v(-24.91, -16.72) * mm, "radius": 0.5 * mm});
            skCircle(sketch, "E16.61.0", {"center": v(-23.82, -18.23) * mm, "radius": 0.5 * mm});
            skCircle(sketch, "E16.62.0", {"center": v(-22.64, -19.68) * mm, "radius": 0.5 * mm});
            skCircle(sketch, "E16.63.0", {"center": v(-21.38, -21.05) * mm, "radius": 0.5 * mm});
            skCircle(sketch, "E16.64.0", {"center": v(-20.03, -22.34) * mm, "radius": 0.5 * mm});
            skCircle(sketch, "E16.65.0", {"center": v(-18.6, -23.54) * mm, "radius": 0.5 * mm});
            skCircle(sketch, "E16.66.0", {"center": v(-17.1, -24.65) * mm, "radius": 0.5 * mm});
            skCircle(sketch, "E16.67.0", {"center": v(-15.54, -25.66) * mm, "radius": 0.5 * mm});
            skCircle(sketch, "E16.68.0", {"center": v(-13.9, -26.58) * mm, "radius": 0.5 * mm});
            skCircle(sketch, "E16.69.0", {"center": v(-12.23, -27.4) * mm, "radius": 0.5 * mm});
            skCircle(sketch, "E16.70.0", {"center": v(-10.5, -28.1) * mm, "radius": 0.5 * mm});
            skCircle(sketch, "E16.71.0", {"center": v(-8.74, -28.7) * mm, "radius": 0.5 * mm});
            skCircle(sketch, "E16.72.0", {"center": v(-6.94, -29.19) * mm, "radius": 0.5 * mm});
            skCircle(sketch, "E16.73.0", {"center": v(-5.1, -29.56) * mm, "radius": 0.5 * mm});
            skCircle(sketch, "E16.74.0", {"center": v(-3.26, -29.82) * mm, "radius": 0.5 * mm});
            skCircle(sketch, "E16.75.0", {"center": v(-1.4, -29.97) * mm, "radius": 0.5 * mm});
            skCircle(sketch, "E16.76.0", {"center": v(0.47, -30) * mm, "radius": 0.5 * mm});
            skCircle(sketch, "E16.77.0", {"center": v(2.33, -29.9) * mm, "radius": 0.5 * mm});
            skCircle(sketch, "E16.78.0", {"center": v(4.19, -29.7) * mm, "radius": 0.5 * mm});
            skCircle(sketch, "E16.79.0", {"center": v(6.02, -29.39) * mm, "radius": 0.5 * mm});
            skCircle(sketch, "E16.80.0", {"center": v(7.84, -28.96) * mm, "radius": 0.5 * mm});
            skCircle(sketch, "E16.81.0", {"center": v(9.62, -28.41) * mm, "radius": 0.5 * mm});
            skCircle(sketch, "E16.82.0", {"center": v(11.37, -27.76) * mm, "radius": 0.5 * mm});
            skCircle(sketch, "E16.83.0", {"center": v(13.08, -27) * mm, "radius": 0.5 * mm});
            skCircle(sketch, "E16.84.0", {"center": v(14.73, -26.13) * mm, "radius": 0.5 * mm});
            skCircle(sketch, "E16.85.0", {"center": v(16.33, -25.17) * mm, "radius": 0.5 * mm});
            skCircle(sketch, "E16.86.0", {"center": v(17.86, -24.1) * mm, "radius": 0.5 * mm});
            skCircle(sketch, "E16.87.0", {"center": v(19.32, -22.95) * mm, "radius": 0.5 * mm});
            skCircle(sketch, "E16.88.0", {"center": v(20.71, -21.7) * mm, "radius": 0.5 * mm});
            skCircle(sketch, "E16.89.0", {"center": v(22.02, -20.37) * mm, "radius": 0.5 * mm});
            skCircle(sketch, "E16.90.0", {"center": v(23.25, -18.96) * mm, "radius": 0.5 * mm});
            skCircle(sketch, "E16.91.0", {"center": v(24.38, -17.48) * mm, "radius": 0.5 * mm});
            skCircle(sketch, "E16.92.0", {"center": v(25.42, -15.93) * mm, "radius": 0.5 * mm});
            skCircle(sketch, "E16.93.0", {"center": v(26.36, -14.32) * mm, "radius": 0.5 * mm});
            skCircle(sketch, "E16.94.0", {"center": v(27.2, -12.66) * mm, "radius": 0.5 * mm});
            skCircle(sketch, "E16.95.0", {"center": v(27.93, -10.94) * mm, "radius": 0.5 * mm});
            skCircle(sketch, "E16.96.0", {"center": v(28.56, -9.18) * mm, "radius": 0.5 * mm});
            skCircle(sketch, "E16.97.0", {"center": v(29.08, -7.39) * mm, "radius": 0.5 * mm});
            skCircle(sketch, "E16.98.0", {"center": v(29.48, -5.57) * mm, "radius": 0.5 * mm});
            skCircle(sketch, "E16.99.0", {"center": v(29.77, -3.72) * mm, "radius": 0.5 * mm});
            skCircle(sketch, "E16.100.0", {"center": v(29.94, -1.87) * mm, "radius": 0.5 * mm});
            skCircle(sketch, "E17.1.0", {"center": v(28.43, 1.94) * mm, "radius": 0.5 * mm});
            skCircle(sketch, "E17.2.0", {"center": v(28.23, 3.88) * mm, "radius": 0.5 * mm});
            skCircle(sketch, "E17.3.0", {"center": v(27.9, 5.8) * mm, "radius": 0.5 * mm});
            skCircle(sketch, "E17.4.0", {"center": v(27.44, 7.69) * mm, "radius": 0.5 * mm});
            skCircle(sketch, "E17.5.0", {"center": v(26.85, 9.54) * mm, "radius": 0.5 * mm});
            skCircle(sketch, "E17.6.0", {"center": v(26.14, 11.35) * mm, "radius": 0.5 * mm});
            skCircle(sketch, "E17.7.0", {"center": v(25.3, 13.11) * mm, "radius": 0.5 * mm});
            skCircle(sketch, "E17.8.0", {"center": v(24.35, 14.8) * mm, "radius": 0.5 * mm});
            skCircle(sketch, "E17.9.0", {"center": v(23.28, 16.44) * mm, "radius": 0.5 * mm});
            skCircle(sketch, "E17.10.0", {"center": v(22.1, 17.99) * mm, "radius": 0.5 * mm});
            skCircle(sketch, "E17.11.0", {"center": v(20.83, 19.45) * mm, "radius": 0.5 * mm});
            skCircle(sketch, "E17.12.0", {"center": v(19.45, 20.83) * mm, "radius": 0.5 * mm});
            skCircle(sketch, "E17.13.0", {"center": v(17.99, 22.1) * mm, "radius": 0.5 * mm});
            skCircle(sketch, "E17.14.0", {"center": v(16.44, 23.28) * mm, "radius": 0.5 * mm});
            skCircle(sketch, "E17.15.0", {"center": v(14.8, 24.35) * mm, "radius": 0.5 * mm});
            skCircle(sketch, "E17.16.0", {"center": v(13.11, 25.3) * mm, "radius": 0.5 * mm});
            skCircle(sketch, "E17.17.0", {"center": v(11.35, 26.14) * mm, "radius": 0.5 * mm});
            skCircle(sketch, "E17.18.0", {"center": v(9.54, 26.85) * mm, "radius": 0.5 * mm});
            skCircle(sketch, "E17.19.0", {"center": v(7.69, 27.44) * mm, "radius": 0.5 * mm});
            skCircle(sketch, "E17.20.0", {"center": v(5.8, 27.9) * mm, "radius": 0.5 * mm});
            skCircle(sketch, "E17.21.0", {"center": v(3.88, 28.23) * mm, "radius": 0.5 * mm});
            skCircle(sketch, "E17.22.0", {"center": v(1.94, 28.43) * mm, "radius": 0.5 * mm});
            skCircle(sketch, "E17.23.0", {"center": v(0, 28.5) * mm, "radius": 0.5 * mm});
            skCircle(sketch, "E17.24.0", {"center": v(-1.94, 28.43) * mm, "radius": 0.5 * mm});
            skCircle(sketch, "E17.25.0", {"center": v(-3.88, 28.23) * mm, "radius": 0.5 * mm});
            skCircle(sketch, "E17.26.0", {"center": v(-5.8, 27.9) * mm, "radius": 0.5 * mm});
            skCircle(sketch, "E17.27.0", {"center": v(-7.69, 27.44) * mm, "radius": 0.5 * mm});
            skCircle(sketch, "E17.28.0", {"center": v(-9.54, 26.85) * mm, "radius": 0.5 * mm});
            skCircle(sketch, "E17.29.0", {"center": v(-11.35, 26.14) * mm, "radius": 0.5 * mm});
            skCircle(sketch, "E17.30.0", {"center": v(-13.11, 25.3) * mm, "radius": 0.5 * mm});
            skCircle(sketch, "E17.31.0", {"center": v(-14.8, 24.35) * mm, "radius": 0.5 * mm});
            skCircle(sketch, "E17.32.0", {"center": v(-16.44, 23.28) * mm, "radius": 0.5 * mm});
            skCircle(sketch, "E17.33.0", {"center": v(-17.99, 22.1) * mm, "radius": 0.5 * mm});
            skCircle(sketch, "E17.34.0", {"center": v(-19.45, 20.83) * mm, "radius": 0.5 * mm});
            skCircle(sketch, "E17.35.0", {"center": v(-20.83, 19.45) * mm, "radius": 0.5 * mm});
            skCircle(sketch, "E17.36.0", {"center": v(-22.1, 17.99) * mm, "radius": 0.5 * mm});
            skCircle(sketch, "E17.37.0", {"center": v(-23.28, 16.44) * mm, "radius": 0.5 * mm});
            skCircle(sketch, "E17.38.0", {"center": v(-24.35, 14.8) * mm, "radius": 0.5 * mm});
            skCircle(sketch, "E17.39.0", {"center": v(-25.3, 13.11) * mm, "radius": 0.5 * mm});
            skCircle(sketch, "E17.40.0", {"center": v(-26.14, 11.35) * mm, "radius": 0.5 * mm});
            skCircle(sketch, "E17.41.0", {"center": v(-26.85, 9.54) * mm, "radius": 0.5 * mm});
            skCircle(sketch, "E17.42.0", {"center": v(-27.44, 7.69) * mm, "radius": 0.5 * mm});
            skCircle(sketch, "E17.43.0", {"center": v(-27.9, 5.8) * mm, "radius": 0.5 * mm});
            skCircle(sketch, "E17.44.0", {"center": v(-28.23, 3.88) * mm, "radius": 0.5 * mm});
            skCircle(sketch, "E17.45.0", {"center": v(-28.43, 1.94) * mm, "radius": 0.5 * mm});
            skCircle(sketch, "E17.46.0", {"center": v(-28.5, 0) * mm, "radius": 0.5 * mm});
            skCircle(sketch, "E17.47.0", {"center": v(-28.43, -1.94) * mm, "radius": 0.5 * mm});
            skCircle(sketch, "E17.48.0", {"center": v(-28.23, -3.88) * mm, "radius": 0.5 * mm});
            skCircle(sketch, "E17.49.0", {"center": v(-27.9, -5.8) * mm, "radius": 0.5 * mm});
            skCircle(sketch, "E17.50.0", {"center": v(-27.44, -7.69) * mm, "radius": 0.5 * mm});
            skCircle(sketch, "E17.51.0", {"center": v(-26.85, -9.54) * mm, "radius": 0.5 * mm});
            skCircle(sketch, "E17.52.0", {"center": v(-26.14, -11.35) * mm, "radius": 0.5 * mm});
            skCircle(sketch, "E17.53.0", {"center": v(-25.3, -13.11) * mm, "radius": 0.5 * mm});
            skCircle(sketch, "E17.54.0", {"center": v(-24.35, -14.8) * mm, "radius": 0.5 * mm});
            skCircle(sketch, "E17.55.0", {"center": v(-23.28, -16.44) * mm, "radius": 0.5 * mm});
            skCircle(sketch, "E17.56.0", {"center": v(-22.1, -17.99) * mm, "radius": 0.5 * mm});
            skCircle(sketch, "E17.57.0", {"center": v(-20.83, -19.45) * mm, "radius": 0.5 * mm});
            skCircle(sketch, "E17.58.0", {"center": v(-19.45, -20.83) * mm, "radius": 0.5 * mm});
            skCircle(sketch, "E17.59.0", {"center": v(-17.99, -22.1) * mm, "radius": 0.5 * mm});
            skCircle(sketch, "E17.60.0", {"center": v(-16.44, -23.28) * mm, "radius": 0.5 * mm});
            skCircle(sketch, "E17.61.0", {"center": v(-14.8, -24.35) * mm, "radius": 0.5 * mm});
            skCircle(sketch, "E17.62.0", {"center": v(-13.11, -25.3) * mm, "radius": 0.5 * mm});
            skCircle(sketch, "E17.63.0", {"center": v(-11.35, -26.14) * mm, "radius": 0.5 * mm});
            skCircle(sketch, "E17.64.0", {"center": v(-9.54, -26.85) * mm, "radius": 0.5 * mm});
            skCircle(sketch, "E17.65.0", {"center": v(-7.69, -27.44) * mm, "radius": 0.5 * mm});
            skCircle(sketch, "E17.66.0", {"center": v(-5.8, -27.9) * mm, "radius": 0.5 * mm});
            skCircle(sketch, "E17.67.0", {"center": v(-3.88, -28.23) * mm, "radius": 0.5 * mm});
            skCircle(sketch, "E17.68.0", {"center": v(-1.94, -28.43) * mm, "radius": 0.5 * mm});
            skCircle(sketch, "E17.69.0", {"center": v(0, -28.5) * mm, "radius": 0.5 * mm});
            skCircle(sketch, "E17.70.0", {"center": v(1.94, -28.43) * mm, "radius": 0.5 * mm});
            skCircle(sketch, "E17.71.0", {"center": v(3.88, -28.23) * mm, "radius": 0.5 * mm});
            skCircle(sketch, "E17.72.0", {"center": v(5.8, -27.9) * mm, "radius": 0.5 * mm});
            skCircle(sketch, "E17.73.0", {"center": v(7.69, -27.44) * mm, "radius": 0.5 * mm});
            skCircle(sketch, "E17.74.0", {"center": v(9.54, -26.85) * mm, "radius": 0.5 * mm});
            skCircle(sketch, "E17.75.0", {"center": v(11.35, -26.14) * mm, "radius": 0.5 * mm});
            skCircle(sketch, "E17.76.0", {"center": v(13.11, -25.3) * mm, "radius": 0.5 * mm});
            skCircle(sketch, "E17.77.0", {"center": v(14.8, -24.35) * mm, "radius": 0.5 * mm});
            skCircle(sketch, "E17.78.0", {"center": v(16.44, -23.28) * mm, "radius": 0.5 * mm});
            skCircle(sketch, "E17.79.0", {"center": v(17.99, -22.1) * mm, "radius": 0.5 * mm});
            skCircle(sketch, "E17.80.0", {"center": v(19.45, -20.83) * mm, "radius": 0.5 * mm});
            skCircle(sketch, "E17.81.0", {"center": v(20.83, -19.45) * mm, "radius": 0.5 * mm});
            skCircle(sketch, "E17.82.0", {"center": v(22.1, -17.99) * mm, "radius": 0.5 * mm});
            skCircle(sketch, "E17.83.0", {"center": v(23.28, -16.44) * mm, "radius": 0.5 * mm});
            skCircle(sketch, "E17.84.0", {"center": v(24.35, -14.8) * mm, "radius": 0.5 * mm});
            skCircle(sketch, "E17.85.0", {"center": v(25.3, -13.11) * mm, "radius": 0.5 * mm});
            skCircle(sketch, "E17.86.0", {"center": v(26.14, -11.35) * mm, "radius": 0.5 * mm});
            skCircle(sketch, "E17.87.0", {"center": v(26.85, -9.54) * mm, "radius": 0.5 * mm});
            skCircle(sketch, "E17.88.0", {"center": v(27.44, -7.69) * mm, "radius": 0.5 * mm});
            skCircle(sketch, "E17.89.0", {"center": v(27.9, -5.8) * mm, "radius": 0.5 * mm});
            skCircle(sketch, "E17.90.0", {"center": v(28.23, -3.88) * mm, "radius": 0.5 * mm});
            skCircle(sketch, "E17.91.0", {"center": v(28.43, -1.94) * mm, "radius": 0.5 * mm});
            skCircle(sketch, "E18.1.0", {"center": v(26.92, 2.04) * mm, "radius": 0.5 * mm});
            skCircle(sketch, "E18.2.0", {"center": v(26.7, 4.07) * mm, "radius": 0.5 * mm});
            skCircle(sketch, "E18.3.0", {"center": v(26.3, 6.08) * mm, "radius": 0.5 * mm});
            skCircle(sketch, "E18.4.0", {"center": v(25.77, 8.05) * mm, "radius": 0.5 * mm});
            skCircle(sketch, "E18.5.0", {"center": v(25.09, 9.98) * mm, "radius": 0.5 * mm});
            skCircle(sketch, "E18.6.0", {"center": v(24.26, 11.85) * mm, "radius": 0.5 * mm});
            skCircle(sketch, "E18.7.0", {"center": v(23.3, 13.65) * mm, "radius": 0.5 * mm});
            skCircle(sketch, "E18.8.0", {"center": v(22.2, 15.37) * mm, "radius": 0.5 * mm});
            skCircle(sketch, "E18.9.0", {"center": v(20.97, 17) * mm, "radius": 0.5 * mm});
            skCircle(sketch, "E18.10.0", {"center": v(19.63, 18.54) * mm, "radius": 0.5 * mm});
            skCircle(sketch, "E18.11.0", {"center": v(18.17, 19.97) * mm, "radius": 0.5 * mm});
            skCircle(sketch, "E18.12.0", {"center": v(16.6, 21.3) * mm, "radius": 0.5 * mm});
            skCircle(sketch, "E18.13.0", {"center": v(14.95, 22.49) * mm, "radius": 0.5 * mm});
            skCircle(sketch, "E18.14.0", {"center": v(13.2, 23.55) * mm, "radius": 0.5 * mm});
            skCircle(sketch, "E18.15.0", {"center": v(11.38, 24.48) * mm, "radius": 0.5 * mm});
            skCircle(sketch, "E18.16.0", {"center": v(9.5, 25.27) * mm, "radius": 0.5 * mm});
            skCircle(sketch, "E18.17.0", {"center": v(7.56, 25.92) * mm, "radius": 0.5 * mm});
            skCircle(sketch, "E18.18.0", {"center": v(5.58, 26.42) * mm, "radius": 0.5 * mm});
            skCircle(sketch, "E18.19.0", {"center": v(3.57, 26.76) * mm, "radius": 0.5 * mm});
            skCircle(sketch, "E18.20.0", {"center": v(1.53, 26.96) * mm, "radius": 0.5 * mm});
            skCircle(sketch, "E18.21.0", {"center": v(-0.51, 27) * mm, "radius": 0.5 * mm});
            skCircle(sketch, "E18.22.0", {"center": v(-2.55, 26.88) * mm, "radius": 0.5 * mm});
            skCircle(sketch, "E18.23.0", {"center": v(-4.58, 26.6) * mm, "radius": 0.5 * mm});
            skCircle(sketch, "E18.24.0", {"center": v(-6.58, 26.19) * mm, "radius": 0.5 * mm});
            skCircle(sketch, "E18.25.0", {"center": v(-8.54, 25.61) * mm, "radius": 0.5 * mm});
            skCircle(sketch, "E18.26.0", {"center": v(-10.45, 24.9) * mm, "radius": 0.5 * mm});
            skCircle(sketch, "E18.27.0", {"center": v(-12.3, 24.03) * mm, "radius": 0.5 * mm});
            skCircle(sketch, "E18.28.0", {"center": v(-14.09, 23.03) * mm, "radius": 0.5 * mm});
            skCircle(sketch, "E18.29.0", {"center": v(-15.79, 21.9) * mm, "radius": 0.5 * mm});
            skCircle(sketch, "E18.30.0", {"center": v(-17.4, 20.65) * mm, "radius": 0.5 * mm});
            skCircle(sketch, "E18.31.0", {"center": v(-18.91, 19.27) * mm, "radius": 0.5 * mm});
            skCircle(sketch, "E18.32.0", {"center": v(-20.31, 17.79) * mm, "radius": 0.5 * mm});
            skCircle(sketch, "E18.33.0", {"center": v(-21.6, 16.2) * mm, "radius": 0.5 * mm});
            skCircle(sketch, "E18.34.0", {"center": v(-22.76, 14.52) * mm, "radius": 0.5 * mm});
            skCircle(sketch, "E18.35.0", {"center": v(-23.8, 12.76) * mm, "radius": 0.5 * mm});
            skCircle(sketch, "E18.36.0", {"center": v(-24.7, 10.92) * mm, "radius": 0.5 * mm});
            skCircle(sketch, "E18.37.0", {"center": v(-25.45, 9.02) * mm, "radius": 0.5 * mm});
            skCircle(sketch, "E18.38.0", {"center": v(-26.06, 7.07) * mm, "radius": 0.5 * mm});
            skCircle(sketch, "E18.39.0", {"center": v(-26.52, 5.08) * mm, "radius": 0.5 * mm});
            skCircle(sketch, "E18.40.0", {"center": v(-26.83, 3.06) * mm, "radius": 0.5 * mm});
            skCircle(sketch, "E18.41.0", {"center": v(-26.98, 1.02) * mm, "radius": 0.5 * mm});
            skCircle(sketch, "E18.42.0", {"center": v(-26.98, -1.02) * mm, "radius": 0.5 * mm});
            skCircle(sketch, "E18.43.0", {"center": v(-26.83, -3.06) * mm, "radius": 0.5 * mm});
            skCircle(sketch, "E18.44.0", {"center": v(-26.52, -5.08) * mm, "radius": 0.5 * mm});
            skCircle(sketch, "E18.45.0", {"center": v(-26.06, -7.07) * mm, "radius": 0.5 * mm});
            skCircle(sketch, "E18.46.0", {"center": v(-25.45, -9.02) * mm, "radius": 0.5 * mm});
            skCircle(sketch, "E18.47.0", {"center": v(-24.7, -10.92) * mm, "radius": 0.5 * mm});
            skCircle(sketch, "E18.48.0", {"center": v(-23.8, -12.76) * mm, "radius": 0.5 * mm});
            skCircle(sketch, "E18.49.0", {"center": v(-22.76, -14.52) * mm, "radius": 0.5 * mm});
            skCircle(sketch, "E18.50.0", {"center": v(-21.6, -16.2) * mm, "radius": 0.5 * mm});
            skCircle(sketch, "E18.51.0", {"center": v(-20.31, -17.79) * mm, "radius": 0.5 * mm});
            skCircle(sketch, "E18.52.0", {"center": v(-18.91, -19.27) * mm, "radius": 0.5 * mm});
            skCircle(sketch, "E18.53.0", {"center": v(-17.4, -20.65) * mm, "radius": 0.5 * mm});
            skCircle(sketch, "E18.54.0", {"center": v(-15.79, -21.9) * mm, "radius": 0.5 * mm});
            skCircle(sketch, "E18.55.0", {"center": v(-14.09, -23.03) * mm, "radius": 0.5 * mm});
            skCircle(sketch, "E18.56.0", {"center": v(-12.3, -24.03) * mm, "radius": 0.5 * mm});
            skCircle(sketch, "E18.57.0", {"center": v(-10.45, -24.9) * mm, "radius": 0.5 * mm});
            skCircle(sketch, "E18.58.0", {"center": v(-8.54, -25.61) * mm, "radius": 0.5 * mm});
            skCircle(sketch, "E18.59.0", {"center": v(-6.58, -26.19) * mm, "radius": 0.5 * mm});
            skCircle(sketch, "E18.60.0", {"center": v(-4.58, -26.6) * mm, "radius": 0.5 * mm});
            skCircle(sketch, "E18.61.0", {"center": v(-2.55, -26.88) * mm, "radius": 0.5 * mm});
            skCircle(sketch, "E18.62.0", {"center": v(-0.51, -27) * mm, "radius": 0.5 * mm});
            skCircle(sketch, "E18.63.0", {"center": v(1.53, -26.96) * mm, "radius": 0.5 * mm});
            skCircle(sketch, "E18.64.0", {"center": v(3.57, -26.76) * mm, "radius": 0.5 * mm});
            skCircle(sketch, "E18.65.0", {"center": v(5.58, -26.42) * mm, "radius": 0.5 * mm});
            skCircle(sketch, "E18.66.0", {"center": v(7.56, -25.92) * mm, "radius": 0.5 * mm});
            skCircle(sketch, "E18.67.0", {"center": v(9.5, -25.27) * mm, "radius": 0.5 * mm});
            skCircle(sketch, "E18.68.0", {"center": v(11.38, -24.48) * mm, "radius": 0.5 * mm});
            skCircle(sketch, "E18.69.0", {"center": v(13.2, -23.55) * mm, "radius": 0.5 * mm});
            skCircle(sketch, "E18.70.0", {"center": v(14.95, -22.49) * mm, "radius": 0.5 * mm});
            skCircle(sketch, "E18.71.0", {"center": v(16.6, -21.3) * mm, "radius": 0.5 * mm});
            skCircle(sketch, "E18.72.0", {"center": v(18.17, -19.97) * mm, "radius": 0.5 * mm});
            skCircle(sketch, "E18.73.0", {"center": v(19.63, -18.54) * mm, "radius": 0.5 * mm});
            skCircle(sketch, "E18.74.0", {"center": v(20.97, -17) * mm, "radius": 0.5 * mm});
            skCircle(sketch, "E18.75.0", {"center": v(22.2, -15.37) * mm, "radius": 0.5 * mm});
            skCircle(sketch, "E18.76.0", {"center": v(23.3, -13.65) * mm, "radius": 0.5 * mm});
            skCircle(sketch, "E18.77.0", {"center": v(24.26, -11.85) * mm, "radius": 0.5 * mm});
            skCircle(sketch, "E18.78.0", {"center": v(25.09, -9.98) * mm, "radius": 0.5 * mm});
            skCircle(sketch, "E18.79.0", {"center": v(25.77, -8.05) * mm, "radius": 0.5 * mm});
            skCircle(sketch, "E18.80.0", {"center": v(26.3, -6.08) * mm, "radius": 0.5 * mm});
            skCircle(sketch, "E18.81.0", {"center": v(26.7, -4.07) * mm, "radius": 0.5 * mm});
            skCircle(sketch, "E18.82.0", {"center": v(26.92, -2.04) * mm, "radius": 0.5 * mm});
            skCircle(sketch, "E19.1.0", {"center": v(25.4, 2.16) * mm, "radius": 0.5 * mm});
            skCircle(sketch, "E19.2.0", {"center": v(25.13, 4.3) * mm, "radius": 0.5 * mm});
            skCircle(sketch, "E19.3.0", {"center": v(24.68, 6.43) * mm, "radius": 0.5 * mm});
            skCircle(sketch, "E19.4.0", {"center": v(24.04, 8.5) * mm, "radius": 0.5 * mm});
            skCircle(sketch, "E19.5.0", {"center": v(23.24, 10.5) * mm, "radius": 0.5 * mm});
            skCircle(sketch, "E19.6.0", {"center": v(22.26, 12.44) * mm, "radius": 0.5 * mm});
            skCircle(sketch, "E19.7.0", {"center": v(21.13, 14.28) * mm, "radius": 0.5 * mm});
            skCircle(sketch, "E19.8.0", {"center": v(19.84, 16.02) * mm, "radius": 0.5 * mm});
            skCircle(sketch, "E19.9.0", {"center": v(18.4, 17.64) * mm, "radius": 0.5 * mm});
            skCircle(sketch, "E19.10.0", {"center": v(16.85, 19.14) * mm, "radius": 0.5 * mm});
            skCircle(sketch, "E19.11.0", {"center": v(15.16, 20.5) * mm, "radius": 0.5 * mm});
            skCircle(sketch, "E19.12.0", {"center": v(13.37, 21.71) * mm, "radius": 0.5 * mm});
            skCircle(sketch, "E19.13.0", {"center": v(11.48, 22.77) * mm, "radius": 0.5 * mm});
            skCircle(sketch, "E19.14.0", {"center": v(9.5, 23.66) * mm, "radius": 0.5 * mm});
            skCircle(sketch, "E19.15.0", {"center": v(7.47, 24.38) * mm, "radius": 0.5 * mm});
            skCircle(sketch, "E19.16.0", {"center": v(5.37, 24.93) * mm, "radius": 0.5 * mm});
            skCircle(sketch, "E19.17.0", {"center": v(3.24, 25.3) * mm, "radius": 0.5 * mm});
            skCircle(sketch, "E19.18.0", {"center": v(1.08, 25.48) * mm, "radius": 0.5 * mm});
            skCircle(sketch, "E19.19.0", {"center": v(-1.08, 25.48) * mm, "radius": 0.5 * mm});
            skCircle(sketch, "E19.20.0", {"center": v(-3.24, 25.3) * mm, "radius": 0.5 * mm});
            skCircle(sketch, "E19.21.0", {"center": v(-5.37, 24.93) * mm, "radius": 0.5 * mm});
            skCircle(sketch, "E19.22.0", {"center": v(-7.47, 24.38) * mm, "radius": 0.5 * mm});
            skCircle(sketch, "E19.23.0", {"center": v(-9.5, 23.66) * mm, "radius": 0.5 * mm});
            skCircle(sketch, "E19.24.0", {"center": v(-11.48, 22.77) * mm, "radius": 0.5 * mm});
            skCircle(sketch, "E19.25.0", {"center": v(-13.37, 21.71) * mm, "radius": 0.5 * mm});
            skCircle(sketch, "E19.26.0", {"center": v(-15.16, 20.5) * mm, "radius": 0.5 * mm});
            skCircle(sketch, "E19.27.0", {"center": v(-16.85, 19.14) * mm, "radius": 0.5 * mm});
            skCircle(sketch, "E19.28.0", {"center": v(-18.4, 17.64) * mm, "radius": 0.5 * mm});
            skCircle(sketch, "E19.29.0", {"center": v(-19.84, 16.02) * mm, "radius": 0.5 * mm});
            skCircle(sketch, "E19.30.0", {"center": v(-21.13, 14.28) * mm, "radius": 0.5 * mm});
            skCircle(sketch, "E19.31.0", {"center": v(-22.26, 12.44) * mm, "radius": 0.5 * mm});
            skCircle(sketch, "E19.32.0", {"center": v(-23.24, 10.5) * mm, "radius": 0.5 * mm});
            skCircle(sketch, "E19.33.0", {"center": v(-24.04, 8.5) * mm, "radius": 0.5 * mm});
            skCircle(sketch, "E19.34.0", {"center": v(-24.68, 6.43) * mm, "radius": 0.5 * mm});
            skCircle(sketch, "E19.35.0", {"center": v(-25.13, 4.3) * mm, "radius": 0.5 * mm});
            skCircle(sketch, "E19.36.0", {"center": v(-25.4, 2.16) * mm, "radius": 0.5 * mm});
            skCircle(sketch, "E19.37.0", {"center": v(-25.5, 0) * mm, "radius": 0.5 * mm});
            skCircle(sketch, "E19.38.0", {"center": v(-25.4, -2.16) * mm, "radius": 0.5 * mm});
            skCircle(sketch, "E19.39.0", {"center": v(-25.13, -4.3) * mm, "radius": 0.5 * mm});
            skCircle(sketch, "E19.40.0", {"center": v(-24.68, -6.43) * mm, "radius": 0.5 * mm});
            skCircle(sketch, "E19.41.0", {"center": v(-24.04, -8.5) * mm, "radius": 0.5 * mm});
            skCircle(sketch, "E19.42.0", {"center": v(-23.24, -10.5) * mm, "radius": 0.5 * mm});
            skCircle(sketch, "E19.43.0", {"center": v(-22.26, -12.44) * mm, "radius": 0.5 * mm});
            skCircle(sketch, "E19.44.0", {"center": v(-21.13, -14.28) * mm, "radius": 0.5 * mm});
            skCircle(sketch, "E19.45.0", {"center": v(-19.84, -16.02) * mm, "radius": 0.5 * mm});
            skCircle(sketch, "E19.46.0", {"center": v(-18.4, -17.64) * mm, "radius": 0.5 * mm});
            skCircle(sketch, "E19.47.0", {"center": v(-16.85, -19.14) * mm, "radius": 0.5 * mm});
            skCircle(sketch, "E19.48.0", {"center": v(-15.16, -20.5) * mm, "radius": 0.5 * mm});
            skCircle(sketch, "E19.49.0", {"center": v(-13.37, -21.71) * mm, "radius": 0.5 * mm});
            skCircle(sketch, "E19.50.0", {"center": v(-11.48, -22.77) * mm, "radius": 0.5 * mm});
            skCircle(sketch, "E19.51.0", {"center": v(-9.5, -23.66) * mm, "radius": 0.5 * mm});
            skCircle(sketch, "E19.52.0", {"center": v(-7.47, -24.38) * mm, "radius": 0.5 * mm});
            skCircle(sketch, "E19.53.0", {"center": v(-5.37, -24.93) * mm, "radius": 0.5 * mm});
            skCircle(sketch, "E19.54.0", {"center": v(-3.24, -25.3) * mm, "radius": 0.5 * mm});
            skCircle(sketch, "E19.55.0", {"center": v(-1.08, -25.48) * mm, "radius": 0.5 * mm});
            skCircle(sketch, "E19.56.0", {"center": v(1.08, -25.48) * mm, "radius": 0.5 * mm});
            skCircle(sketch, "E19.57.0", {"center": v(3.24, -25.3) * mm, "radius": 0.5 * mm});
            skCircle(sketch, "E19.58.0", {"center": v(5.37, -24.93) * mm, "radius": 0.5 * mm});
            skCircle(sketch, "E19.59.0", {"center": v(7.47, -24.38) * mm, "radius": 0.5 * mm});
            skCircle(sketch, "E19.60.0", {"center": v(9.5, -23.66) * mm, "radius": 0.5 * mm});
            skCircle(sketch, "E19.61.0", {"center": v(11.48, -22.77) * mm, "radius": 0.5 * mm});
            skCircle(sketch, "E19.62.0", {"center": v(13.37, -21.71) * mm, "radius": 0.5 * mm});
            skCircle(sketch, "E19.63.0", {"center": v(15.16, -20.5) * mm, "radius": 0.5 * mm});
            skCircle(sketch, "E19.64.0", {"center": v(16.85, -19.14) * mm, "radius": 0.5 * mm});
            skCircle(sketch, "E19.65.0", {"center": v(18.4, -17.64) * mm, "radius": 0.5 * mm});
            skCircle(sketch, "E19.66.0", {"center": v(19.84, -16.02) * mm, "radius": 0.5 * mm});
            skCircle(sketch, "E19.67.0", {"center": v(21.13, -14.28) * mm, "radius": 0.5 * mm});
            skCircle(sketch, "E19.68.0", {"center": v(22.26, -12.44) * mm, "radius": 0.5 * mm});
            skCircle(sketch, "E19.69.0", {"center": v(23.24, -10.5) * mm, "radius": 0.5 * mm});
            skCircle(sketch, "E19.70.0", {"center": v(24.04, -8.5) * mm, "radius": 0.5 * mm});
            skCircle(sketch, "E19.71.0", {"center": v(24.68, -6.43) * mm, "radius": 0.5 * mm});
            skCircle(sketch, "E19.72.0", {"center": v(25.13, -4.3) * mm, "radius": 0.5 * mm});
            skCircle(sketch, "E19.73.0", {"center": v(25.4, -2.16) * mm, "radius": 0.5 * mm});
            skCircle(sketch, "E20.1.0", {"center": v(23.89, 2.32) * mm, "radius": 0.5 * mm});
            skCircle(sketch, "E20.2.0", {"center": v(23.55, 4.61) * mm, "radius": 0.5 * mm});
            skCircle(sketch, "E20.3.0", {"center": v(23, 6.86) * mm, "radius": 0.5 * mm});
            skCircle(sketch, "E20.4.0", {"center": v(22.23, 9.05) * mm, "radius": 0.5 * mm});
            skCircle(sketch, "E20.5.0", {"center": v(21.25, 11.15) * mm, "radius": 0.5 * mm});
            skCircle(sketch, "E20.6.0", {"center": v(20.08, 13.15) * mm, "radius": 0.5 * mm});
            skCircle(sketch, "E20.7.0", {"center": v(18.71, 15.03) * mm, "radius": 0.5 * mm});
            skCircle(sketch, "E20.8.0", {"center": v(17.17, 16.76) * mm, "radius": 0.5 * mm});
            skCircle(sketch, "E20.9.0", {"center": v(15.48, 18.34) * mm, "radius": 0.5 * mm});
            skCircle(sketch, "E20.10.0", {"center": v(13.63, 19.75) * mm, "radius": 0.5 * mm});
            skCircle(sketch, "E20.11.0", {"center": v(11.66, 20.98) * mm, "radius": 0.5 * mm});
            skCircle(sketch, "E20.12.0", {"center": v(9.58, 22) * mm, "radius": 0.5 * mm});
            skCircle(sketch, "E20.13.0", {"center": v(7.42, 22.83) * mm, "radius": 0.5 * mm});
            skCircle(sketch, "E20.14.0", {"center": v(5.18, 23.43) * mm, "radius": 0.5 * mm});
            skCircle(sketch, "E20.15.0", {"center": v(2.9, 23.83) * mm, "radius": 0.5 * mm});
            skCircle(sketch, "E20.16.0", {"center": v(0.58, 24) * mm, "radius": 0.5 * mm});
            skCircle(sketch, "E20.17.0", {"center": v(-1.74, 23.94) * mm, "radius": 0.5 * mm});
            skCircle(sketch, "E20.18.0", {"center": v(-4.04, 23.66) * mm, "radius": 0.5 * mm});
            skCircle(sketch, "E20.19.0", {"center": v(-6.3, 23.16) * mm, "radius": 0.5 * mm});
            skCircle(sketch, "E20.20.0", {"center": v(-8.51, 22.44) * mm, "radius": 0.5 * mm});
            skCircle(sketch, "E20.21.0", {"center": v(-10.64, 21.51) * mm, "radius": 0.5 * mm});
            skCircle(sketch, "E20.22.0", {"center": v(-12.66, 20.39) * mm, "radius": 0.5 * mm});
            skCircle(sketch, "E20.23.0", {"center": v(-14.57, 19.07) * mm, "radius": 0.5 * mm});
            skCircle(sketch, "E20.24.0", {"center": v(-16.34, 17.57) * mm, "radius": 0.5 * mm});
            skCircle(sketch, "E20.25.0", {"center": v(-17.96, 15.91) * mm, "radius": 0.5 * mm});
            skCircle(sketch, "E20.26.0", {"center": v(-19.42, 14.1) * mm, "radius": 0.5 * mm});
            skCircle(sketch, "E20.27.0", {"center": v(-20.69, 12.17) * mm, "radius": 0.5 * mm});
            skCircle(sketch, "E20.28.0", {"center": v(-21.76, 10.11) * mm, "radius": 0.5 * mm});
            skCircle(sketch, "E20.29.0", {"center": v(-22.64, 7.97) * mm, "radius": 0.5 * mm});
            skCircle(sketch, "E20.30.0", {"center": v(-23.3, 5.74) * mm, "radius": 0.5 * mm});
            skCircle(sketch, "E20.31.0", {"center": v(-23.75, 3.47) * mm, "radius": 0.5 * mm});
            skCircle(sketch, "E20.32.0", {"center": v(-23.97, 1.16) * mm, "radius": 0.5 * mm});
            skCircle(sketch, "E20.33.0", {"center": v(-23.97, -1.16) * mm, "radius": 0.5 * mm});
            skCircle(sketch, "E20.34.0", {"center": v(-23.75, -3.47) * mm, "radius": 0.5 * mm});
            skCircle(sketch, "E20.35.0", {"center": v(-23.3, -5.74) * mm, "radius": 0.5 * mm});
            skCircle(sketch, "E20.36.0", {"center": v(-22.64, -7.97) * mm, "radius": 0.5 * mm});
            skCircle(sketch, "E20.37.0", {"center": v(-21.76, -10.11) * mm, "radius": 0.5 * mm});
            skCircle(sketch, "E20.38.0", {"center": v(-20.69, -12.17) * mm, "radius": 0.5 * mm});
            skCircle(sketch, "E20.39.0", {"center": v(-19.42, -14.1) * mm, "radius": 0.5 * mm});
            skCircle(sketch, "E20.40.0", {"center": v(-17.96, -15.91) * mm, "radius": 0.5 * mm});
            skCircle(sketch, "E20.41.0", {"center": v(-16.34, -17.57) * mm, "radius": 0.5 * mm});
            skCircle(sketch, "E20.42.0", {"center": v(-14.57, -19.07) * mm, "radius": 0.5 * mm});
            skCircle(sketch, "E20.43.0", {"center": v(-12.66, -20.39) * mm, "radius": 0.5 * mm});
            skCircle(sketch, "E20.44.0", {"center": v(-10.64, -21.51) * mm, "radius": 0.5 * mm});
            skCircle(sketch, "E20.45.0", {"center": v(-8.51, -22.44) * mm, "radius": 0.5 * mm});
            skCircle(sketch, "E20.46.0", {"center": v(-6.3, -23.16) * mm, "radius": 0.5 * mm});
            skCircle(sketch, "E20.47.0", {"center": v(-4.04, -23.66) * mm, "radius": 0.5 * mm});
            skCircle(sketch, "E20.48.0", {"center": v(-1.74, -23.94) * mm, "radius": 0.5 * mm});
            skCircle(sketch, "E20.49.0", {"center": v(0.58, -24) * mm, "radius": 0.5 * mm});
            skCircle(sketch, "E20.50.0", {"center": v(2.9, -23.83) * mm, "radius": 0.5 * mm});
            skCircle(sketch, "E20.51.0", {"center": v(5.18, -23.43) * mm, "radius": 0.5 * mm});
            skCircle(sketch, "E20.52.0", {"center": v(7.42, -22.83) * mm, "radius": 0.5 * mm});
            skCircle(sketch, "E20.53.0", {"center": v(9.58, -22) * mm, "radius": 0.5 * mm});
            skCircle(sketch, "E20.54.0", {"center": v(11.66, -20.98) * mm, "radius": 0.5 * mm});
            skCircle(sketch, "E20.55.0", {"center": v(13.63, -19.75) * mm, "radius": 0.5 * mm});
            skCircle(sketch, "E20.56.0", {"center": v(15.48, -18.34) * mm, "radius": 0.5 * mm});
            skCircle(sketch, "E20.57.0", {"center": v(17.17, -16.76) * mm, "radius": 0.5 * mm});
            skCircle(sketch, "E20.58.0", {"center": v(18.71, -15.03) * mm, "radius": 0.5 * mm});
            skCircle(sketch, "E20.59.0", {"center": v(20.08, -13.15) * mm, "radius": 0.5 * mm});
            skCircle(sketch, "E20.60.0", {"center": v(21.25, -11.15) * mm, "radius": 0.5 * mm});
            skCircle(sketch, "E20.61.0", {"center": v(22.23, -9.05) * mm, "radius": 0.5 * mm});
            skCircle(sketch, "E20.62.0", {"center": v(23, -6.86) * mm, "radius": 0.5 * mm});
            skCircle(sketch, "E20.63.0", {"center": v(23.55, -4.61) * mm, "radius": 0.5 * mm});
            skCircle(sketch, "E20.64.0", {"center": v(23.89, -2.32) * mm, "radius": 0.5 * mm});
            skCircle(sketch, "E21.1.0", {"center": v(22.36, 2.52) * mm, "radius": 0.5 * mm});
            skCircle(sketch, "E21.2.0", {"center": v(21.94, 5) * mm, "radius": 0.5 * mm});
            skCircle(sketch, "E21.3.0", {"center": v(21.24, 7.43) * mm, "radius": 0.5 * mm});
            skCircle(sketch, "E21.4.0", {"center": v(20.27, 9.76) * mm, "radius": 0.5 * mm});
            skCircle(sketch, "E21.5.0", {"center": v(19.05, 11.97) * mm, "radius": 0.5 * mm});
            skCircle(sketch, "E21.6.0", {"center": v(17.6, 14.03) * mm, "radius": 0.5 * mm});
            skCircle(sketch, "E21.7.0", {"center": v(15.9, 15.9) * mm, "radius": 0.5 * mm});
            skCircle(sketch, "E21.8.0", {"center": v(14.03, 17.6) * mm, "radius": 0.5 * mm});
            skCircle(sketch, "E21.9.0", {"center": v(11.97, 19.05) * mm, "radius": 0.5 * mm});
            skCircle(sketch, "E21.10.0", {"center": v(9.76, 20.27) * mm, "radius": 0.5 * mm});
            skCircle(sketch, "E21.11.0", {"center": v(7.43, 21.24) * mm, "radius": 0.5 * mm});
            skCircle(sketch, "E21.12.0", {"center": v(5, 21.94) * mm, "radius": 0.5 * mm});
            skCircle(sketch, "E21.13.0", {"center": v(2.52, 22.36) * mm, "radius": 0.5 * mm});
            skCircle(sketch, "E21.14.0", {"center": v(0, 22.5) * mm, "radius": 0.5 * mm});
            skCircle(sketch, "E21.15.0", {"center": v(-2.52, 22.36) * mm, "radius": 0.5 * mm});
            skCircle(sketch, "E21.16.0", {"center": v(-5, 21.94) * mm, "radius": 0.5 * mm});
            skCircle(sketch, "E21.17.0", {"center": v(-7.43, 21.24) * mm, "radius": 0.5 * mm});
            skCircle(sketch, "E21.18.0", {"center": v(-9.76, 20.27) * mm, "radius": 0.5 * mm});
            skCircle(sketch, "E21.19.0", {"center": v(-11.97, 19.05) * mm, "radius": 0.5 * mm});
            skCircle(sketch, "E21.20.0", {"center": v(-14.03, 17.6) * mm, "radius": 0.5 * mm});
            skCircle(sketch, "E21.21.0", {"center": v(-15.9, 15.9) * mm, "radius": 0.5 * mm});
            skCircle(sketch, "E21.22.0", {"center": v(-17.6, 14.03) * mm, "radius": 0.5 * mm});
            skCircle(sketch, "E21.23.0", {"center": v(-19.05, 11.97) * mm, "radius": 0.5 * mm});
            skCircle(sketch, "E21.24.0", {"center": v(-20.27, 9.76) * mm, "radius": 0.5 * mm});
            skCircle(sketch, "E21.25.0", {"center": v(-21.24, 7.43) * mm, "radius": 0.5 * mm});
            skCircle(sketch, "E21.26.0", {"center": v(-21.94, 5) * mm, "radius": 0.5 * mm});
            skCircle(sketch, "E21.27.0", {"center": v(-22.36, 2.52) * mm, "radius": 0.5 * mm});
            skCircle(sketch, "E21.28.0", {"center": v(-22.5, 0) * mm, "radius": 0.5 * mm});
            skCircle(sketch, "E21.29.0", {"center": v(-22.36, -2.52) * mm, "radius": 0.5 * mm});
            skCircle(sketch, "E21.30.0", {"center": v(-21.94, -5) * mm, "radius": 0.5 * mm});
            skCircle(sketch, "E21.31.0", {"center": v(-21.24, -7.43) * mm, "radius": 0.5 * mm});
            skCircle(sketch, "E21.32.0", {"center": v(-20.27, -9.76) * mm, "radius": 0.5 * mm});
            skCircle(sketch, "E21.33.0", {"center": v(-19.05, -11.97) * mm, "radius": 0.5 * mm});
            skCircle(sketch, "E21.34.0", {"center": v(-17.6, -14.03) * mm, "radius": 0.5 * mm});
            skCircle(sketch, "E21.35.0", {"center": v(-15.9, -15.9) * mm, "radius": 0.5 * mm});
            skCircle(sketch, "E21.36.0", {"center": v(-14.03, -17.6) * mm, "radius": 0.5 * mm});
            skCircle(sketch, "E21.37.0", {"center": v(-11.97, -19.05) * mm, "radius": 0.5 * mm});
            skCircle(sketch, "E21.38.0", {"center": v(-9.76, -20.27) * mm, "radius": 0.5 * mm});
            skCircle(sketch, "E21.39.0", {"center": v(-7.43, -21.24) * mm, "radius": 0.5 * mm});
            skCircle(sketch, "E21.40.0", {"center": v(-5, -21.94) * mm, "radius": 0.5 * mm});
            skCircle(sketch, "E21.41.0", {"center": v(-2.52, -22.36) * mm, "radius": 0.5 * mm});
            skCircle(sketch, "E21.42.0", {"center": v(0, -22.5) * mm, "radius": 0.5 * mm});
            skCircle(sketch, "E21.43.0", {"center": v(2.52, -22.36) * mm, "radius": 0.5 * mm});
            skCircle(sketch, "E21.44.0", {"center": v(5, -21.94) * mm, "radius": 0.5 * mm});
            skCircle(sketch, "E21.45.0", {"center": v(7.43, -21.24) * mm, "radius": 0.5 * mm});
            skCircle(sketch, "E21.46.0", {"center": v(9.76, -20.27) * mm, "radius": 0.5 * mm});
            skCircle(sketch, "E21.47.0", {"center": v(11.97, -19.05) * mm, "radius": 0.5 * mm});
            skCircle(sketch, "E21.48.0", {"center": v(14.03, -17.6) * mm, "radius": 0.5 * mm});
            skCircle(sketch, "E21.49.0", {"center": v(15.9, -15.9) * mm, "radius": 0.5 * mm});
            skCircle(sketch, "E21.50.0", {"center": v(17.6, -14.03) * mm, "radius": 0.5 * mm});
            skCircle(sketch, "E21.51.0", {"center": v(19.05, -11.97) * mm, "radius": 0.5 * mm});
            skCircle(sketch, "E21.52.0", {"center": v(20.27, -9.76) * mm, "radius": 0.5 * mm});
            skCircle(sketch, "E21.53.0", {"center": v(21.24, -7.43) * mm, "radius": 0.5 * mm});
            skCircle(sketch, "E21.54.0", {"center": v(21.94, -5) * mm, "radius": 0.5 * mm});
            skCircle(sketch, "E21.55.0", {"center": v(22.36, -2.52) * mm, "radius": 0.5 * mm});
            skCircle(sketch, "E22.1.0", {"center": v(20.81, 2.8) * mm, "radius": 0.5 * mm});
            skCircle(sketch, "E22.2.0", {"center": v(20.25, 5.55) * mm, "radius": 0.5 * mm});
            skCircle(sketch, "E22.3.0", {"center": v(19.33, 8.2) * mm, "radius": 0.5 * mm});
            skCircle(sketch, "E22.4.0", {"center": v(18.07, 10.7) * mm, "radius": 0.5 * mm});
            skCircle(sketch, "E22.5.0", {"center": v(16.48, 13.01) * mm, "radius": 0.5 * mm});
            skCircle(sketch, "E22.6.0", {"center": v(14.6, 15.1) * mm, "radius": 0.5 * mm});
            skCircle(sketch, "E22.7.0", {"center": v(12.46, 16.9) * mm, "radius": 0.5 * mm});
            skCircle(sketch, "E22.8.0", {"center": v(10.1, 18.42) * mm, "radius": 0.5 * mm});
            skCircle(sketch, "E22.9.0", {"center": v(7.55, 19.6) * mm, "radius": 0.5 * mm});
            skCircle(sketch, "E22.10.0", {"center": v(4.87, 20.43) * mm, "radius": 0.5 * mm});
            skCircle(sketch, "E22.11.0", {"center": v(2.1, 20.9) * mm, "radius": 0.5 * mm});
            skCircle(sketch, "E22.12.0", {"center": v(-0.7, 20.99) * mm, "radius": 0.5 * mm});
            skCircle(sketch, "E22.13.0", {"center": v(-3.5, 20.7) * mm, "radius": 0.5 * mm});
            skCircle(sketch, "E22.14.0", {"center": v(-6.22, 20.06) * mm, "radius": 0.5 * mm});
            skCircle(sketch, "E22.15.0", {"center": v(-8.84, 19.05) * mm, "radius": 0.5 * mm});
            skCircle(sketch, "E22.16.0", {"center": v(-11.3, 17.7) * mm, "radius": 0.5 * mm});
            skCircle(sketch, "E22.17.0", {"center": v(-13.56, 16.04) * mm, "radius": 0.5 * mm});
            skCircle(sketch, "E22.18.0", {"center": v(-15.57, 14.09) * mm, "radius": 0.5 * mm});
            skCircle(sketch, "E22.19.0", {"center": v(-17.31, 11.88) * mm, "radius": 0.5 * mm});
            skCircle(sketch, "E22.20.0", {"center": v(-18.74, 9.47) * mm, "radius": 0.5 * mm});
            skCircle(sketch, "E22.21.0", {"center": v(-19.84, 6.89) * mm, "radius": 0.5 * mm});
            skCircle(sketch, "E22.22.0", {"center": v(-20.58, 4.18) * mm, "radius": 0.5 * mm});
            skCircle(sketch, "E22.23.0", {"center": v(-20.95, 1.4) * mm, "radius": 0.5 * mm});
            skCircle(sketch, "E22.24.0", {"center": v(-20.95, -1.4) * mm, "radius": 0.5 * mm});
            skCircle(sketch, "E22.25.0", {"center": v(-20.58, -4.18) * mm, "radius": 0.5 * mm});
            skCircle(sketch, "E22.26.0", {"center": v(-19.84, -6.89) * mm, "radius": 0.5 * mm});
            skCircle(sketch, "E22.27.0", {"center": v(-18.74, -9.47) * mm, "radius": 0.5 * mm});
            skCircle(sketch, "E22.28.0", {"center": v(-17.31, -11.88) * mm, "radius": 0.5 * mm});
            skCircle(sketch, "E22.29.0", {"center": v(-15.57, -14.09) * mm, "radius": 0.5 * mm});
            skCircle(sketch, "E22.30.0", {"center": v(-13.56, -16.04) * mm, "radius": 0.5 * mm});
            skCircle(sketch, "E22.31.0", {"center": v(-11.3, -17.7) * mm, "radius": 0.5 * mm});
            skCircle(sketch, "E22.32.0", {"center": v(-8.84, -19.05) * mm, "radius": 0.5 * mm});
            skCircle(sketch, "E22.33.0", {"center": v(-6.22, -20.06) * mm, "radius": 0.5 * mm});
            skCircle(sketch, "E22.34.0", {"center": v(-3.5, -20.7) * mm, "radius": 0.5 * mm});
            skCircle(sketch, "E22.35.0", {"center": v(-0.7, -20.99) * mm, "radius": 0.5 * mm});
            skCircle(sketch, "E22.36.0", {"center": v(2.1, -20.9) * mm, "radius": 0.5 * mm});
            skCircle(sketch, "E22.37.0", {"center": v(4.87, -20.43) * mm, "radius": 0.5 * mm});
            skCircle(sketch, "E22.38.0", {"center": v(7.55, -19.6) * mm, "radius": 0.5 * mm});
            skCircle(sketch, "E22.39.0", {"center": v(10.1, -18.42) * mm, "radius": 0.5 * mm});
            skCircle(sketch, "E22.40.0", {"center": v(12.46, -16.9) * mm, "radius": 0.5 * mm});
            skCircle(sketch, "E22.41.0", {"center": v(14.6, -15.1) * mm, "radius": 0.5 * mm});
            skCircle(sketch, "E22.42.0", {"center": v(16.48, -13.01) * mm, "radius": 0.5 * mm});
            skCircle(sketch, "E22.43.0", {"center": v(18.07, -10.7) * mm, "radius": 0.5 * mm});
            skCircle(sketch, "E22.44.0", {"center": v(19.33, -8.2) * mm, "radius": 0.5 * mm});
            skCircle(sketch, "E22.45.0", {"center": v(20.25, -5.55) * mm, "radius": 0.5 * mm});
            skCircle(sketch, "E22.46.0", {"center": v(20.81, -2.8) * mm, "radius": 0.5 * mm});
            skCircle(sketch, "E23.1.0", {"center": v(19.23, 3.2) * mm, "radius": 0.5 * mm});
            skCircle(sketch, "E23.2.0", {"center": v(18.44, 6.33) * mm, "radius": 0.5 * mm});
            skCircle(sketch, "E23.3.0", {"center": v(17.15, 9.28) * mm, "radius": 0.5 * mm});
            skCircle(sketch, "E23.4.0", {"center": v(15.39, 11.98) * mm, "radius": 0.5 * mm});
            skCircle(sketch, "E23.5.0", {"center": v(13.2, 14.35) * mm, "radius": 0.5 * mm});
            skCircle(sketch, "E23.6.0", {"center": v(10.67, 16.32) * mm, "radius": 0.5 * mm});
            skCircle(sketch, "E23.7.0", {"center": v(7.83, 17.86) * mm, "radius": 0.5 * mm});
            skCircle(sketch, "E23.8.0", {"center": v(4.79, 18.9) * mm, "radius": 0.5 * mm});
            skCircle(sketch, "E23.9.0", {"center": v(1.61, 19.43) * mm, "radius": 0.5 * mm});
            skCircle(sketch, "E23.10.0", {"center": v(-1.61, 19.43) * mm, "radius": 0.5 * mm});
            skCircle(sketch, "E23.11.0", {"center": v(-4.79, 18.9) * mm, "radius": 0.5 * mm});
            skCircle(sketch, "E23.12.0", {"center": v(-7.83, 17.86) * mm, "radius": 0.5 * mm});
            skCircle(sketch, "E23.13.0", {"center": v(-10.67, 16.32) * mm, "radius": 0.5 * mm});
            skCircle(sketch, "E23.14.0", {"center": v(-13.2, 14.35) * mm, "radius": 0.5 * mm});
            skCircle(sketch, "E23.15.0", {"center": v(-15.39, 11.98) * mm, "radius": 0.5 * mm});
            skCircle(sketch, "E23.16.0", {"center": v(-17.15, 9.28) * mm, "radius": 0.5 * mm});
            skCircle(sketch, "E23.17.0", {"center": v(-18.44, 6.33) * mm, "radius": 0.5 * mm});
            skCircle(sketch, "E23.18.0", {"center": v(-19.23, 3.2) * mm, "radius": 0.5 * mm});
            skCircle(sketch, "E23.19.0", {"center": v(-19.5, 0) * mm, "radius": 0.5 * mm});
            skCircle(sketch, "E23.20.0", {"center": v(-19.23, -3.2) * mm, "radius": 0.5 * mm});
            skCircle(sketch, "E23.21.0", {"center": v(-18.44, -6.33) * mm, "radius": 0.5 * mm});
            skCircle(sketch, "E23.22.0", {"center": v(-17.15, -9.28) * mm, "radius": 0.5 * mm});
            skCircle(sketch, "E23.23.0", {"center": v(-15.39, -11.98) * mm, "radius": 0.5 * mm});
            skCircle(sketch, "E23.24.0", {"center": v(-13.2, -14.35) * mm, "radius": 0.5 * mm});
            skCircle(sketch, "E23.25.0", {"center": v(-10.67, -16.32) * mm, "radius": 0.5 * mm});
            skCircle(sketch, "E23.26.0", {"center": v(-7.83, -17.86) * mm, "radius": 0.5 * mm});
            skCircle(sketch, "E23.27.0", {"center": v(-4.79, -18.9) * mm, "radius": 0.5 * mm});
            skCircle(sketch, "E23.28.0", {"center": v(-1.61, -19.43) * mm, "radius": 0.5 * mm});
            skCircle(sketch, "E23.29.0", {"center": v(1.61, -19.43) * mm, "radius": 0.5 * mm});
            skCircle(sketch, "E23.30.0", {"center": v(4.79, -18.9) * mm, "radius": 0.5 * mm});
            skCircle(sketch, "E23.31.0", {"center": v(7.83, -17.86) * mm, "radius": 0.5 * mm});
            skCircle(sketch, "E23.32.0", {"center": v(10.67, -16.32) * mm, "radius": 0.5 * mm});
            skCircle(sketch, "E23.33.0", {"center": v(13.2, -14.35) * mm, "radius": 0.5 * mm});
            skCircle(sketch, "E23.34.0", {"center": v(15.39, -11.98) * mm, "radius": 0.5 * mm});
            skCircle(sketch, "E23.35.0", {"center": v(17.15, -9.28) * mm, "radius": 0.5 * mm});
            skCircle(sketch, "E23.36.0", {"center": v(18.44, -6.33) * mm, "radius": 0.5 * mm});
            skCircle(sketch, "E23.37.0", {"center": v(19.23, -3.2) * mm, "radius": 0.5 * mm});
            skCircle(sketch, "E24.1.0", {"center": v(17.58, 3.87) * mm, "radius": 0.5 * mm});
            skCircle(sketch, "E24.2.0", {"center": v(16.34, 7.56) * mm, "radius": 0.5 * mm});
            skCircle(sketch, "E24.3.0", {"center": v(14.33, 10.9) * mm, "radius": 0.5 * mm});
            skCircle(sketch, "E24.4.0", {"center": v(11.65, 13.72) * mm, "radius": 0.5 * mm});
            skCircle(sketch, "E24.5.0", {"center": v(8.43, 15.9) * mm, "radius": 0.5 * mm});
            skCircle(sketch, "E24.6.0", {"center": v(4.82, 17.34) * mm, "radius": 0.5 * mm});
            skCircle(sketch, "E24.7.0", {"center": v(0.97, 17.97) * mm, "radius": 0.5 * mm});
            skCircle(sketch, "E24.8.0", {"center": v(-2.91, 17.76) * mm, "radius": 0.5 * mm});
            skCircle(sketch, "E24.9.0", {"center": v(-6.66, 16.72) * mm, "radius": 0.5 * mm});
            skCircle(sketch, "E24.10.0", {"center": v(-10.1, 14.9) * mm, "radius": 0.5 * mm});
            skCircle(sketch, "E24.11.0", {"center": v(-13.07, 12.38) * mm, "radius": 0.5 * mm});
            skCircle(sketch, "E24.12.0", {"center": v(-15.42, 9.28) * mm, "radius": 0.5 * mm});
            skCircle(sketch, "E24.13.0", {"center": v(-17.06, 5.75) * mm, "radius": 0.5 * mm});
            skCircle(sketch, "E24.14.0", {"center": v(-17.9, 1.95) * mm, "radius": 0.5 * mm});
            skCircle(sketch, "E24.15.0", {"center": v(-17.9, -1.95) * mm, "radius": 0.5 * mm});
            skCircle(sketch, "E24.16.0", {"center": v(-17.06, -5.75) * mm, "radius": 0.5 * mm});
            skCircle(sketch, "E24.17.0", {"center": v(-15.42, -9.28) * mm, "radius": 0.5 * mm});
            skCircle(sketch, "E24.18.0", {"center": v(-13.07, -12.38) * mm, "radius": 0.5 * mm});
            skCircle(sketch, "E24.19.0", {"center": v(-10.1, -14.9) * mm, "radius": 0.5 * mm});
            skCircle(sketch, "E24.20.0", {"center": v(-6.66, -16.72) * mm, "radius": 0.5 * mm});
            skCircle(sketch, "E24.21.0", {"center": v(-2.91, -17.76) * mm, "radius": 0.5 * mm});
            skCircle(sketch, "E24.22.0", {"center": v(0.97, -17.97) * mm, "radius": 0.5 * mm});
            skCircle(sketch, "E24.23.0", {"center": v(4.82, -17.34) * mm, "radius": 0.5 * mm});
            skCircle(sketch, "E24.24.0", {"center": v(8.43, -15.9) * mm, "radius": 0.5 * mm});
            skCircle(sketch, "E24.25.0", {"center": v(11.65, -13.72) * mm, "radius": 0.5 * mm});
            skCircle(sketch, "E24.26.0", {"center": v(14.33, -10.9) * mm, "radius": 0.5 * mm});
            skCircle(sketch, "E24.27.0", {"center": v(16.34, -7.56) * mm, "radius": 0.5 * mm});
            skCircle(sketch, "E24.28.0", {"center": v(17.58, -3.87) * mm, "radius": 0.5 * mm});
            skCircle(sketch, "E25.1.0", {"center": v(15.7, 5.1) * mm, "radius": 0.5 * mm});
            skCircle(sketch, "E25.2.0", {"center": v(13.35, 9.7) * mm, "radius": 0.5 * mm});
            skCircle(sketch, "E25.3.0", {"center": v(9.7, 13.35) * mm, "radius": 0.5 * mm});
            skCircle(sketch, "E25.4.0", {"center": v(5.1, 15.7) * mm, "radius": 0.5 * mm});
            skCircle(sketch, "E25.5.0", {"center": v(0, 16.5) * mm, "radius": 0.5 * mm});
            skCircle(sketch, "E25.6.0", {"center": v(-5.1, 15.7) * mm, "radius": 0.5 * mm});
            skCircle(sketch, "E25.7.0", {"center": v(-9.7, 13.35) * mm, "radius": 0.5 * mm});
            skCircle(sketch, "E25.8.0", {"center": v(-13.35, 9.7) * mm, "radius": 0.5 * mm});
            skCircle(sketch, "E25.9.0", {"center": v(-15.7, 5.1) * mm, "radius": 0.5 * mm});
            skCircle(sketch, "E25.10.0", {"center": v(-16.5, 0) * mm, "radius": 0.5 * mm});
            skCircle(sketch, "E25.11.0", {"center": v(-15.7, -5.1) * mm, "radius": 0.5 * mm});
            skCircle(sketch, "E25.12.0", {"center": v(-13.35, -9.7) * mm, "radius": 0.5 * mm});
            skCircle(sketch, "E25.13.0", {"center": v(-9.7, -13.35) * mm, "radius": 0.5 * mm});
            skCircle(sketch, "E25.14.0", {"center": v(-5.1, -15.7) * mm, "radius": 0.5 * mm});
            skCircle(sketch, "E25.15.0", {"center": v(0, -16.5) * mm, "radius": 0.5 * mm});
            skCircle(sketch, "E25.16.0", {"center": v(5.1, -15.7) * mm, "radius": 0.5 * mm});
            skCircle(sketch, "E25.17.0", {"center": v(9.7, -13.35) * mm, "radius": 0.5 * mm});
            skCircle(sketch, "E25.18.0", {"center": v(13.35, -9.7) * mm, "radius": 0.5 * mm});
            skCircle(sketch, "E25.19.0", {"center": v(15.7, -5.1) * mm, "radius": 0.5 * mm});
            skCircle(sketch, "E26.1.0", {"center": v(12.62, 8.1) * mm, "radius": 0.5 * mm});
            skCircle(sketch, "E26.2.0", {"center": v(6.23, 13.64) * mm, "radius": 0.5 * mm});
            skCircle(sketch, "E26.3.0", {"center": v(-2.13, 14.85) * mm, "radius": 0.5 * mm});
            skCircle(sketch, "E26.4.0", {"center": v(-9.82, 11.34) * mm, "radius": 0.5 * mm});
            skCircle(sketch, "E26.5.0", {"center": v(-14.4, 4.23) * mm, "radius": 0.5 * mm});
            skCircle(sketch, "E26.6.0", {"center": v(-14.4, -4.23) * mm, "radius": 0.5 * mm});
            skCircle(sketch, "E26.7.0", {"center": v(-9.82, -11.34) * mm, "radius": 0.5 * mm});
            skCircle(sketch, "E26.8.0", {"center": v(-2.13, -14.85) * mm, "radius": 0.5 * mm});
            skCircle(sketch, "E26.9.0", {"center": v(6.23, -13.64) * mm, "radius": 0.5 * mm});
            skCircle(sketch, "E26.10.0", {"center": v(12.62, -8.1) * mm, "radius": 0.5 * mm});
            skCircle(sketch, "E27.1.0", {"center": v(-13.5, 0) * mm, "radius": 0.5 * mm});
            skSolve(sketch);
        }
        {
            var Q0;
            Q0 = qSketchRegion(id + "F4", true);
            extrude(context, id + "F5", {"entities" : qUnion([Q0]), "operationType" : NewBodyOperationType.REMOVE, "oppositeDirection" : true, "depth" : 25 * mm, "offsetDistance" : 25 * mm});
        }
        {
            var Q0;
            Q0=makeQuery(id+"F1.opExtrude","CAP_FACE",FACE,{"disambiguationData":[OSD([sQuery(id+"F0.wireOp",EDGE,"E0")])],"isStart":false});
            var sketch = newSketch(context, id + "F6", { "sketchPlane" : qUnion([Q0])});
            skPoint(sketch, "E28", {"position": v(0, 50) * mm});
            skArc(sketch, "E29", {"start": v(10, 48.99) * mm, "mid": v(0, 50) * mm, "end": v(-10, 48.99) * mm});
            skPoint(sketch, "E30", {"position": v(0, 48) * mm});
            skArc(sketch, "E31", {"start": v(10, 46.95) * mm, "mid": v(0, 48) * mm, "end": v(-10, 46.95) * mm});
            skLineSegment(sketch, "E32", {"start": v(-10, 48.99) * mm, "end": v(-10, 46.95) * mm});
            skLineSegment(sketch, "E33", {"start": v(10, 48.99) * mm, "end": v(10, 46.95) * mm});
            skSolve(sketch);
        }
        {
            var Q0;
            Q0 = qSketchRegion(id + "F6", true);
            extrude(context, id + "F7", {"entities" : qUnion([Q0]), "operationType" : NewBodyOperationType.ADD, "depth" : 100 * mm, "offsetDistance" : 25 * mm});
        }
        {
            var Q0;
            Q0=makeQuery(id+"F7.opExtrude","CAP_FACE",FACE,{"disambiguationData":[OSD([sQuery(id+"F6.wireOp",EDGE,"E29"),sQuery(id+"F6.wireOp",EDGE,"E31"),sQuery(id+"F6.wireOp",EDGE,"E32"),sQuery(id+"F6.wireOp",EDGE,"E33")])],"isStart":false});
            var sketch = newSketch(context, id + "F8", { "sketchPlane" : qUnion([Q0])});
            skLineSegment(sketch, "E34.bottom", {"start": v(-10, 48.99) * mm, "end": v(10, 48.99) * mm});
            skLineSegment(sketch, "E34.top", {"start": v(-10, 42.99) * mm, "end": v(10, 42.99) * mm});
            skLineSegment(sketch, "E34.left", {"start": v(-10, 48.99) * mm, "end": v(-10, 42.99) * mm});
            skLineSegment(sketch, "E34.right", {"start": v(10, 48.99) * mm, "end": v(10, 42.99) * mm});
            skSolve(sketch);
        }
        {
            var Q0;
            Q0 = qSketchRegion(id + "F8", true);
            extrude(context, id + "F9", {"entities" : qUnion([Q0]), "operationType" : NewBodyOperationType.ADD, "oppositeDirection" : true, "depth" : 2 * mm, "offsetDistance" : 25 * mm});
        }
        {
            var Q0;
            Q0=makeQuery(id+"F9.opExtrude","CAP_EDGE",EDGE,{"disambiguationData":[OSD([sQuery(id+"F8.wireOp",EDGE,"E34.top")])],"isStart":false});
            chamfer(context, id + "F10", {"entities" : qUnion([Q0]), "width" : 1 * mm, "tangentPropagation" : true});
        }
        {
            var Q0;
            Q0=makeQuery(id+"F9.opExtrude","SWEPT_EDGE",EDGE,{"disambiguationData":[OSD([sQuery(id+"F8.wireOp",EDGE,"E34.top"),sQuery(id+"F8.wireOp",EDGE,"E34.left")])]});
            var Q1;
            Q1=makeQuery(id+"F9.opExtrude","SWEPT_EDGE",EDGE,{"disambiguationData":[OSD([sQuery(id+"F8.wireOp",EDGE,"E34.top"),sQuery(id+"F8.wireOp",EDGE,"E34.right")])]});
            fillet(context, id + "F11", {"entities" : qUnion([Q0, Q1]), "radius" : 1 * mm, "tangentPropagation" : true, "allowEdgeOverflow" : false});
        }
    });
